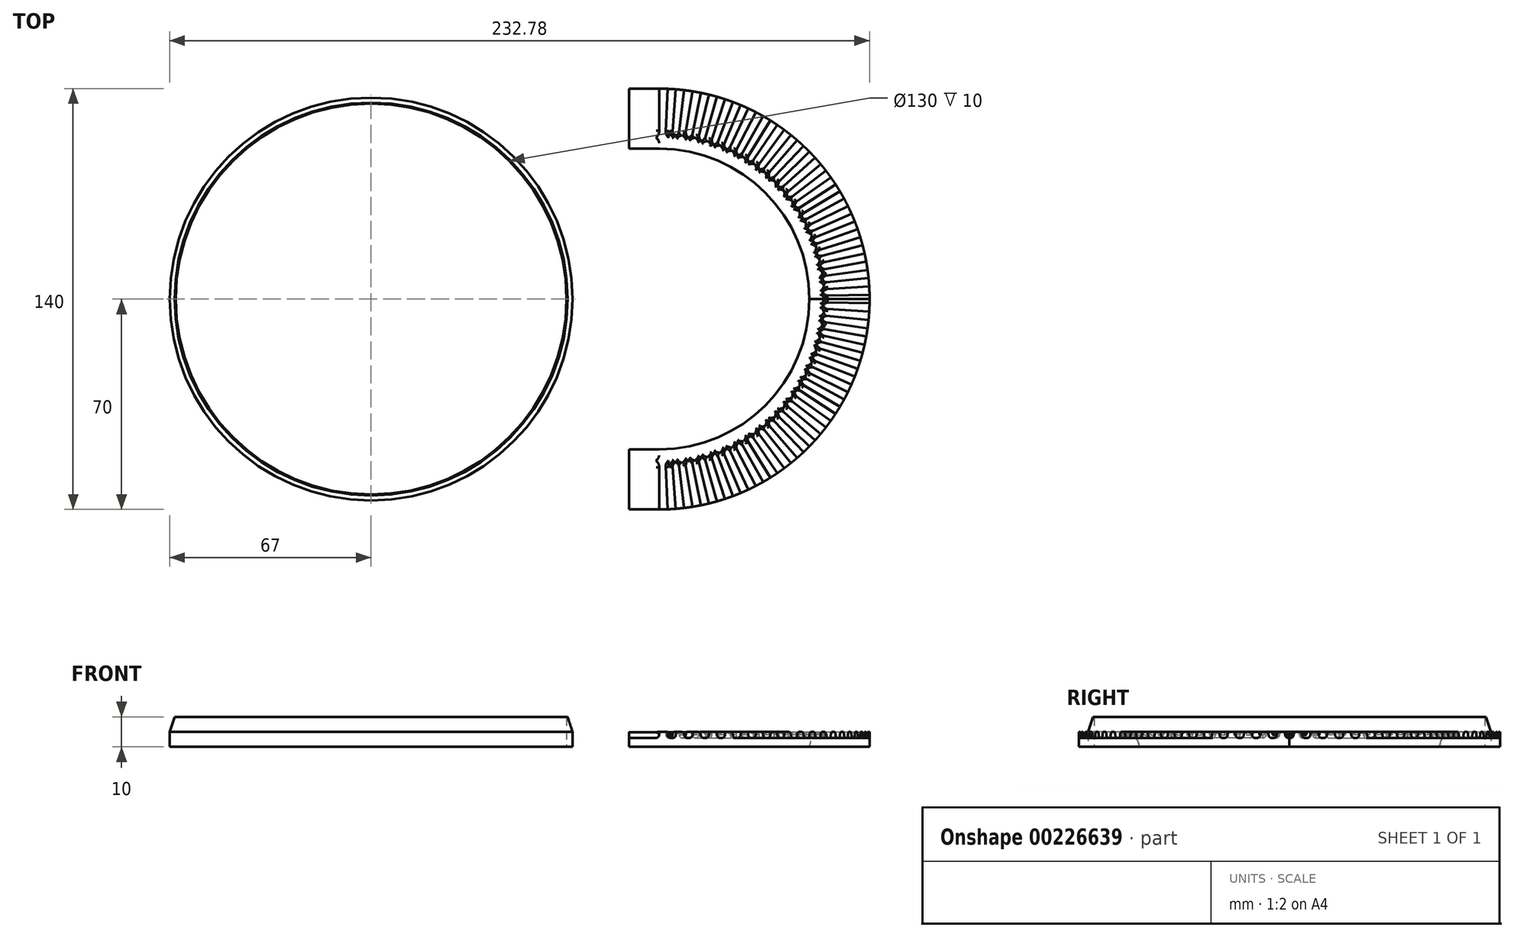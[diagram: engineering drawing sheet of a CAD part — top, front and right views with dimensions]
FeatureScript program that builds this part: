
annotation { "Feature Type Name" : "Feature", "Feature Type Description" : "" }
export const myFeature = defineFeature(function(context is Context, id is Id, definition is map)
    precondition{}
    {
        {
            var Q0;
            Q0=qCreatedBy(makeId("Top.planeOp"),FACE);
            var sketch = newSketch(context, id + "F0", { "sketchPlane" : qUnion([Q0])});
            skCircle(sketch, "E0", {"center": v(0, 0) * mm, "radius": 65 * mm});
            skCircle(sketch, "E1", {"center": v(0, 0) * mm, "radius": 67 * mm});
            skSolve(sketch);
        }
        {
            var Q0;
            Q0=makeQuery(id+"F0.imprint","IMPRINT",FACE,{"disambiguationData":[TD([[makeQuery(id+"F0.imprint","IMPRINT",EDGE,{"derivedFrom":sQuery(id+"F0.wireOp",EDGE,"E0")}),-1.0]])]});
            extrude(context, id + "F1", {"entities" : qUnion([Q0]), "depth" : 10 * mm});
        }
        {
            var Q0;
            Q0=makeQuery(id+"F1.opExtrude","CAP_EDGE",EDGE,{"disambiguationData":[OSD([sQuery(id+"F0.wireOp",EDGE,"E1")])],"isStart":false});
            chamfer(context, id + "F2", {"entities" : qUnion([Q0]), "chamferType" : ChamferType.TWO_OFFSETS, "width1" : 1.65 * mm, "oppositeDirection" : false, "width2" : 5 * mm, "tangentPropagation" : true});
        }
        {
            var Q0;
            Q0=qCreatedBy(makeId("Top.planeOp"),FACE);
            var sketch = newSketch(context, id + "F3", { "sketchPlane" : qUnion([Q0])});
            skLineSegment(sketch, "E2", {"start": v(95.78, 0) * mm, "end": v(95.78, 70) * mm, "construction": true});
            skArc(sketch, "E3", {"start": v(95.78, 70) * mm, "mid": v(165.78, 0) * mm, "end": v(95.78, -70) * mm});
            skArc(sketch, "E4", {"start": v(95.78, 50) * mm, "mid": v(145.78, 0) * mm, "end": v(95.78, -50) * mm});
            skLineSegment(sketch, "E5.bottom", {"start": v(95.78, 50) * mm, "end": v(85.78, 50) * mm});
            skLineSegment(sketch, "E5.top", {"start": v(95.78, 70) * mm, "end": v(85.78, 70) * mm});
            skLineSegment(sketch, "E5.left", {"start": v(95.78, 50) * mm, "end": v(95.78, 70) * mm});
            skLineSegment(sketch, "E5.right", {"start": v(85.78, 50) * mm, "end": v(85.78, 70) * mm});
            skLineSegment(sketch, "E6.bottom", {"start": v(95.78, -50) * mm, "end": v(85.78, -50) * mm});
            skLineSegment(sketch, "E6.top", {"start": v(95.78, -70) * mm, "end": v(85.78, -70) * mm});
            skLineSegment(sketch, "E6.left", {"start": v(95.78, -50) * mm, "end": v(95.78, -70) * mm});
            skLineSegment(sketch, "E6.right", {"start": v(85.78, -50) * mm, "end": v(85.78, -70) * mm});
            skSolve(sketch);
        }
        {
            var Q0;
            Q0 = qSketchRegion(id + "F3", true);
            extrude(context, id + "F4", {"entities" : qUnion([Q0]), "depth" : 5 * mm});
        }
        {
            var Q0;
            Q0=makeQuery(id+"F4.opExtrude","CAP_EDGE",EDGE,{"disambiguationData":[OSD([sQuery(id+"F3.wireOp",EDGE,"E4")])],"isStart":false});
            fillet(context, id + "F5", {"entities" : qUnion([Q0]), "radius" : 5 * mm, "tangentPropagation" : true, "allowEdgeOverflow" : false});
        }
        {
            var Q0;
            Q0=makeQuery(id+"F4.opExtrude","CAP_FACE",FACE,{"disambiguationData":[OSD([sQuery(id+"F3.wireOp",EDGE,"E3"),sQuery(id+"F3.wireOp",EDGE,"E4"),sQuery(id+"F3.wireOp",EDGE,"E5.bottom"),sQuery(id+"F3.wireOp",EDGE,"E5.top"),sQuery(id+"F3.wireOp",EDGE,"E5.right"),sQuery(id+"F3.wireOp",EDGE,"E6.bottom"),sQuery(id+"F3.wireOp",EDGE,"E6.top"),sQuery(id+"F3.wireOp",EDGE,"E6.right")])],"isStart":false});
            var sketch = newSketch(context, id + "F6", { "sketchPlane" : qUnion([Q0])});
            skLineSegment(sketch, "E7", {"start": v(95.78, 0) * mm, "end": v(95.78, 55) * mm, "construction": true});
            skLineSegment(sketch, "E8", {"start": v(95.78, 55) * mm, "end": v(95.78, 70) * mm});
            skLineSegment(sketch, "E9.1.0", {"start": v(97.97, 54.96) * mm, "end": v(98.57, 69.94) * mm});
            skLineSegment(sketch, "E9.2.0", {"start": v(100.15, 54.83) * mm, "end": v(101.34, 69.78) * mm});
            skLineSegment(sketch, "E9.3.0", {"start": v(102.33, 54.6) * mm, "end": v(104.11, 69.5) * mm});
            skLineSegment(sketch, "E9.4.0", {"start": v(104.5, 54.3) * mm, "end": v(106.87, 69.12) * mm});
            skLineSegment(sketch, "E9.5.0", {"start": v(106.65, 53.92) * mm, "end": v(109.61, 68.62) * mm});
            skLineSegment(sketch, "E9.6.0", {"start": v(108.78, 53.44) * mm, "end": v(112.33, 68.02) * mm});
            skLineSegment(sketch, "E9.7.0", {"start": v(110.9, 52.88) * mm, "end": v(115.02, 67.3) * mm});
            skLineSegment(sketch, "E9.8.0", {"start": v(112.99, 52.24) * mm, "end": v(117.68, 66.49) * mm});
            skLineSegment(sketch, "E9.9.0", {"start": v(115.05, 51.51) * mm, "end": v(120.3, 65.56) * mm});
            skLineSegment(sketch, "E9.10.0", {"start": v(117.08, 50.7) * mm, "end": v(122.9, 64.54) * mm});
            skLineSegment(sketch, "E9.11.0", {"start": v(119.08, 49.82) * mm, "end": v(125.44, 63.4) * mm});
            skLineSegment(sketch, "E9.12.0", {"start": v(121.04, 48.86) * mm, "end": v(127.93, 62.18) * mm});
            skLineSegment(sketch, "E9.13.0", {"start": v(122.97, 47.81) * mm, "end": v(130.38, 60.85) * mm});
            skLineSegment(sketch, "E9.14.0", {"start": v(124.85, 46.7) * mm, "end": v(132.77, 59.43) * mm});
            skLineSegment(sketch, "E9.15.0", {"start": v(126.68, 45.5) * mm, "end": v(135.1, 57.91) * mm});
            skLineSegment(sketch, "E9.16.0", {"start": v(128.46, 44.24) * mm, "end": v(137.38, 56.3) * mm});
            skLineSegment(sketch, "E9.17.0", {"start": v(130.2, 42.9) * mm, "end": v(139.58, 54.6) * mm});
            skLineSegment(sketch, "E9.18.0", {"start": v(131.88, 41.5) * mm, "end": v(141.72, 52.82) * mm});
            skLineSegment(sketch, "E9.19.0", {"start": v(133.5, 40.03) * mm, "end": v(143.78, 50.95) * mm});
            skLineSegment(sketch, "E9.20.0", {"start": v(135.06, 38.5) * mm, "end": v(145.77, 49) * mm});
            skLineSegment(sketch, "E9.21.0", {"start": v(136.56, 36.91) * mm, "end": v(147.68, 46.98) * mm});
            skLineSegment(sketch, "E9.22.0", {"start": v(138, 35.26) * mm, "end": v(149.5, 44.88) * mm});
            skLineSegment(sketch, "E9.23.0", {"start": v(139.36, 33.55) * mm, "end": v(151.25, 42.7) * mm});
            skLineSegment(sketch, "E9.24.0", {"start": v(140.66, 31.8) * mm, "end": v(152.9, 40.47) * mm});
            skLineSegment(sketch, "E9.25.0", {"start": v(141.9, 29.99) * mm, "end": v(154.47, 38.16) * mm});
            skLineSegment(sketch, "E9.26.0", {"start": v(143.05, 28.13) * mm, "end": v(155.94, 35.8) * mm});
            skLineSegment(sketch, "E9.27.0", {"start": v(144.13, 26.23) * mm, "end": v(157.31, 33.38) * mm});
            skLineSegment(sketch, "E9.28.0", {"start": v(145.13, 24.29) * mm, "end": v(158.6, 30.9) * mm});
            skLineSegment(sketch, "E9.29.0", {"start": v(146.06, 22.3) * mm, "end": v(159.77, 28.39) * mm});
            skLineSegment(sketch, "E9.30.0", {"start": v(146.9, 20.29) * mm, "end": v(160.85, 25.82) * mm});
            skLineSegment(sketch, "E9.31.0", {"start": v(147.67, 18.24) * mm, "end": v(161.82, 23.21) * mm});
            skLineSegment(sketch, "E9.32.0", {"start": v(148.36, 16.16) * mm, "end": v(162.7, 20.57) * mm});
            skLineSegment(sketch, "E9.33.0", {"start": v(148.96, 14.06) * mm, "end": v(163.46, 17.9) * mm});
            skLineSegment(sketch, "E9.34.0", {"start": v(149.47, 11.93) * mm, "end": v(164.12, 15.19) * mm});
            skLineSegment(sketch, "E9.35.0", {"start": v(149.9, 9.79) * mm, "end": v(164.67, 12.46) * mm});
            skLineSegment(sketch, "E9.36.0", {"start": v(150.25, 7.63) * mm, "end": v(165.1, 9.71) * mm});
            skLineSegment(sketch, "E9.37.0", {"start": v(150.51, 5.46) * mm, "end": v(165.44, 6.95) * mm});
            skLineSegment(sketch, "E9.38.0", {"start": v(150.69, 3.28) * mm, "end": v(165.66, 4.17) * mm});
            skLineSegment(sketch, "E9.39.0", {"start": v(150.77, 1.1) * mm, "end": v(165.77, 1.4) * mm});
            skLineSegment(sketch, "E9.40.0", {"start": v(150.77, -1.1) * mm, "end": v(165.77, -1.4) * mm});
            skLineSegment(sketch, "E9.41.0", {"start": v(150.69, -3.28) * mm, "end": v(165.66, -4.17) * mm});
            skLineSegment(sketch, "E9.42.0", {"start": v(150.51, -5.46) * mm, "end": v(165.44, -6.95) * mm});
            skLineSegment(sketch, "E9.43.0", {"start": v(150.25, -7.63) * mm, "end": v(165.1, -9.71) * mm});
            skLineSegment(sketch, "E9.44.0", {"start": v(149.9, -9.79) * mm, "end": v(164.67, -12.46) * mm});
            skLineSegment(sketch, "E9.45.0", {"start": v(149.47, -11.93) * mm, "end": v(164.12, -15.19) * mm});
            skLineSegment(sketch, "E9.46.0", {"start": v(148.96, -14.06) * mm, "end": v(163.46, -17.9) * mm});
            skLineSegment(sketch, "E9.47.0", {"start": v(148.36, -16.16) * mm, "end": v(162.7, -20.57) * mm});
            skLineSegment(sketch, "E9.48.0", {"start": v(147.67, -18.24) * mm, "end": v(161.82, -23.21) * mm});
            skLineSegment(sketch, "E9.49.0", {"start": v(146.9, -20.29) * mm, "end": v(160.85, -25.82) * mm});
            skLineSegment(sketch, "E9.50.0", {"start": v(146.06, -22.3) * mm, "end": v(159.77, -28.39) * mm});
            skLineSegment(sketch, "E9.51.0", {"start": v(145.13, -24.29) * mm, "end": v(158.6, -30.9) * mm});
            skLineSegment(sketch, "E9.52.0", {"start": v(144.13, -26.23) * mm, "end": v(157.31, -33.38) * mm});
            skLineSegment(sketch, "E9.53.0", {"start": v(143.05, -28.13) * mm, "end": v(155.94, -35.8) * mm});
            skLineSegment(sketch, "E9.54.0", {"start": v(141.9, -29.99) * mm, "end": v(154.47, -38.16) * mm});
            skLineSegment(sketch, "E9.55.0", {"start": v(140.66, -31.8) * mm, "end": v(152.9, -40.47) * mm});
            skLineSegment(sketch, "E9.56.0", {"start": v(139.36, -33.55) * mm, "end": v(151.25, -42.7) * mm});
            skLineSegment(sketch, "E9.57.0", {"start": v(138, -35.26) * mm, "end": v(149.5, -44.88) * mm});
            skLineSegment(sketch, "E9.58.0", {"start": v(136.56, -36.91) * mm, "end": v(147.68, -46.98) * mm});
            skLineSegment(sketch, "E9.59.0", {"start": v(135.06, -38.5) * mm, "end": v(145.77, -49) * mm});
            skLineSegment(sketch, "E9.60.0", {"start": v(133.5, -40.03) * mm, "end": v(143.78, -50.95) * mm});
            skLineSegment(sketch, "E9.61.0", {"start": v(131.88, -41.5) * mm, "end": v(141.72, -52.82) * mm});
            skLineSegment(sketch, "E9.62.0", {"start": v(130.2, -42.9) * mm, "end": v(139.58, -54.6) * mm});
            skLineSegment(sketch, "E9.63.0", {"start": v(128.46, -44.24) * mm, "end": v(137.38, -56.3) * mm});
            skLineSegment(sketch, "E9.64.0", {"start": v(126.68, -45.5) * mm, "end": v(135.1, -57.91) * mm});
            skLineSegment(sketch, "E9.65.0", {"start": v(124.85, -46.7) * mm, "end": v(132.77, -59.43) * mm});
            skLineSegment(sketch, "E9.66.0", {"start": v(122.97, -47.81) * mm, "end": v(130.38, -60.85) * mm});
            skLineSegment(sketch, "E9.67.0", {"start": v(121.04, -48.86) * mm, "end": v(127.93, -62.18) * mm});
            skLineSegment(sketch, "E9.68.0", {"start": v(119.08, -49.82) * mm, "end": v(125.44, -63.4) * mm});
            skLineSegment(sketch, "E9.69.0", {"start": v(117.08, -50.7) * mm, "end": v(122.9, -64.54) * mm});
            skLineSegment(sketch, "E9.70.0", {"start": v(115.05, -51.51) * mm, "end": v(120.3, -65.56) * mm});
            skLineSegment(sketch, "E9.71.0", {"start": v(112.99, -52.24) * mm, "end": v(117.68, -66.49) * mm});
            skLineSegment(sketch, "E9.72.0", {"start": v(110.9, -52.88) * mm, "end": v(115.02, -67.3) * mm});
            skLineSegment(sketch, "E9.73.0", {"start": v(108.78, -53.44) * mm, "end": v(112.33, -68.02) * mm});
            skLineSegment(sketch, "E9.74.0", {"start": v(106.65, -53.92) * mm, "end": v(109.61, -68.62) * mm});
            skLineSegment(sketch, "E9.75.0", {"start": v(104.5, -54.3) * mm, "end": v(106.87, -69.12) * mm});
            skLineSegment(sketch, "E9.76.0", {"start": v(102.33, -54.6) * mm, "end": v(104.11, -69.5) * mm});
            skLineSegment(sketch, "E9.77.0", {"start": v(100.15, -54.83) * mm, "end": v(101.34, -69.78) * mm});
            skLineSegment(sketch, "E9.78.0", {"start": v(97.97, -54.96) * mm, "end": v(98.57, -69.94) * mm});
            skLineSegment(sketch, "E9.79.0", {"start": v(95.78, -55) * mm, "end": v(95.78, -70) * mm});
            skPoint(sketch, "E9.center", {"position": v(95.78, 0) * mm});
            skLineSegment(sketch, "E9.anchor2", {"start": v(95.78, 0) * mm, "end": v(95.78, -55) * mm, "construction": true});
            skSolve(sketch);
        }
        {
            var Q0;
            Q0=makeQuery(id+"F6.imprint","IMPRINT",FACE,{"disambiguationData":[TD([[makeQuery(id+"F6.imprint","IMPRINT",EDGE,{"derivedFrom":sQuery(id+"F6.wireOp",EDGE,"E8")}),1.0]])]});
            var Q1;
            {var subQ0=sQuery(id+"F6.wireOp",EDGE,"E9.1.0");Q1=makeQuery(id+"F6.imprint","IMPRINT",FACE,{"disambiguationData":[TD([[makeQuery(id+"F6.imprint","IMPRINT",EDGE,{"derivedFrom":subQ0}),-1.0]])]});}
            var Q2;
            {var subQ0=sQuery(id+"F6.wireOp",EDGE,"E9.3.0");Q2=makeQuery(id+"F6.imprint","IMPRINT",FACE,{"disambiguationData":[TD([[makeQuery(id+"F6.imprint","IMPRINT",EDGE,{"derivedFrom":subQ0}),-1.0]])]});}
            var Q3;
            {var subQ0=sQuery(id+"F6.wireOp",EDGE,"E9.5.0");Q3=makeQuery(id+"F6.imprint","IMPRINT",FACE,{"disambiguationData":[TD([[makeQuery(id+"F6.imprint","IMPRINT",EDGE,{"derivedFrom":subQ0}),-1.0]])]});}
            var Q4;
            {var subQ0=sQuery(id+"F6.wireOp",EDGE,"E9.7.0");Q4=makeQuery(id+"F6.imprint","IMPRINT",FACE,{"disambiguationData":[TD([[makeQuery(id+"F6.imprint","IMPRINT",EDGE,{"derivedFrom":subQ0}),-1.0]])]});}
            var Q5;
            {var subQ0=sQuery(id+"F6.wireOp",EDGE,"E9.9.0");Q5=makeQuery(id+"F6.imprint","IMPRINT",FACE,{"disambiguationData":[TD([[makeQuery(id+"F6.imprint","IMPRINT",EDGE,{"derivedFrom":subQ0}),-1.0]])]});}
            var Q6;
            {var subQ0=sQuery(id+"F6.wireOp",EDGE,"E9.11.0");Q6=makeQuery(id+"F6.imprint","IMPRINT",FACE,{"disambiguationData":[TD([[makeQuery(id+"F6.imprint","IMPRINT",EDGE,{"derivedFrom":subQ0}),-1.0]])]});}
            var Q7;
            {var subQ0=sQuery(id+"F6.wireOp",EDGE,"E9.13.0");Q7=makeQuery(id+"F6.imprint","IMPRINT",FACE,{"disambiguationData":[TD([[makeQuery(id+"F6.imprint","IMPRINT",EDGE,{"derivedFrom":subQ0}),-1.0]])]});}
            var Q8;
            {var subQ0=sQuery(id+"F6.wireOp",EDGE,"E9.15.0");Q8=makeQuery(id+"F6.imprint","IMPRINT",FACE,{"disambiguationData":[TD([[makeQuery(id+"F6.imprint","IMPRINT",EDGE,{"derivedFrom":subQ0}),-1.0]])]});}
            var Q9;
            {var subQ0=sQuery(id+"F6.wireOp",EDGE,"E9.17.0");Q9=makeQuery(id+"F6.imprint","IMPRINT",FACE,{"disambiguationData":[TD([[makeQuery(id+"F6.imprint","IMPRINT",EDGE,{"derivedFrom":subQ0}),-1.0]])]});}
            var Q10;
            {var subQ0=sQuery(id+"F6.wireOp",EDGE,"E9.19.0");Q10=makeQuery(id+"F6.imprint","IMPRINT",FACE,{"disambiguationData":[TD([[makeQuery(id+"F6.imprint","IMPRINT",EDGE,{"derivedFrom":subQ0}),-1.0]])]});}
            var Q11;
            {var subQ0=sQuery(id+"F6.wireOp",EDGE,"E9.21.0");Q11=makeQuery(id+"F6.imprint","IMPRINT",FACE,{"disambiguationData":[TD([[makeQuery(id+"F6.imprint","IMPRINT",EDGE,{"derivedFrom":subQ0}),-1.0]])]});}
            var Q12;
            {var subQ0=sQuery(id+"F6.wireOp",EDGE,"E9.23.0");Q12=makeQuery(id+"F6.imprint","IMPRINT",FACE,{"disambiguationData":[TD([[makeQuery(id+"F6.imprint","IMPRINT",EDGE,{"derivedFrom":subQ0}),-1.0]])]});}
            var Q13;
            {var subQ0=sQuery(id+"F6.wireOp",EDGE,"E9.25.0");Q13=makeQuery(id+"F6.imprint","IMPRINT",FACE,{"disambiguationData":[TD([[makeQuery(id+"F6.imprint","IMPRINT",EDGE,{"derivedFrom":subQ0}),-1.0]])]});}
            var Q14;
            {var subQ0=sQuery(id+"F6.wireOp",EDGE,"E9.27.0");Q14=makeQuery(id+"F6.imprint","IMPRINT",FACE,{"disambiguationData":[TD([[makeQuery(id+"F6.imprint","IMPRINT",EDGE,{"derivedFrom":subQ0}),-1.0]])]});}
            var Q15;
            {var subQ0=sQuery(id+"F6.wireOp",EDGE,"E9.29.0");Q15=makeQuery(id+"F6.imprint","IMPRINT",FACE,{"disambiguationData":[TD([[makeQuery(id+"F6.imprint","IMPRINT",EDGE,{"derivedFrom":subQ0}),-1.0]])]});}
            var Q16;
            {var subQ0=sQuery(id+"F6.wireOp",EDGE,"E9.31.0");Q16=makeQuery(id+"F6.imprint","IMPRINT",FACE,{"disambiguationData":[TD([[makeQuery(id+"F6.imprint","IMPRINT",EDGE,{"derivedFrom":subQ0}),-1.0]])]});}
            var Q17;
            {var subQ0=sQuery(id+"F6.wireOp",EDGE,"E9.33.0");Q17=makeQuery(id+"F6.imprint","IMPRINT",FACE,{"disambiguationData":[TD([[makeQuery(id+"F6.imprint","IMPRINT",EDGE,{"derivedFrom":subQ0}),-1.0]])]});}
            var Q18;
            {var subQ0=sQuery(id+"F6.wireOp",EDGE,"E9.35.0");Q18=makeQuery(id+"F6.imprint","IMPRINT",FACE,{"disambiguationData":[TD([[makeQuery(id+"F6.imprint","IMPRINT",EDGE,{"derivedFrom":subQ0}),-1.0]])]});}
            var Q19;
            {var subQ0=sQuery(id+"F6.wireOp",EDGE,"E9.37.0");Q19=makeQuery(id+"F6.imprint","IMPRINT",FACE,{"disambiguationData":[TD([[makeQuery(id+"F6.imprint","IMPRINT",EDGE,{"derivedFrom":subQ0}),-1.0]])]});}
            var Q20;
            {var subQ0=sQuery(id+"F6.wireOp",EDGE,"E9.39.0");Q20=makeQuery(id+"F6.imprint","IMPRINT",FACE,{"disambiguationData":[TD([[makeQuery(id+"F6.imprint","IMPRINT",EDGE,{"derivedFrom":subQ0}),-1.0]])]});}
            var Q21;
            {var subQ0=sQuery(id+"F6.wireOp",EDGE,"E9.41.0");Q21=makeQuery(id+"F6.imprint","IMPRINT",FACE,{"disambiguationData":[TD([[makeQuery(id+"F6.imprint","IMPRINT",EDGE,{"derivedFrom":subQ0}),-1.0]])]});}
            var Q22;
            {var subQ0=sQuery(id+"F6.wireOp",EDGE,"E9.43.0");Q22=makeQuery(id+"F6.imprint","IMPRINT",FACE,{"disambiguationData":[TD([[makeQuery(id+"F6.imprint","IMPRINT",EDGE,{"derivedFrom":subQ0}),-1.0]])]});}
            var Q23;
            {var subQ0=sQuery(id+"F6.wireOp",EDGE,"E9.45.0");Q23=makeQuery(id+"F6.imprint","IMPRINT",FACE,{"disambiguationData":[TD([[makeQuery(id+"F6.imprint","IMPRINT",EDGE,{"derivedFrom":subQ0}),-1.0]])]});}
            var Q24;
            {var subQ0=sQuery(id+"F6.wireOp",EDGE,"E9.47.0");Q24=makeQuery(id+"F6.imprint","IMPRINT",FACE,{"disambiguationData":[TD([[makeQuery(id+"F6.imprint","IMPRINT",EDGE,{"derivedFrom":subQ0}),-1.0]])]});}
            var Q25;
            {var subQ0=sQuery(id+"F6.wireOp",EDGE,"E9.49.0");Q25=makeQuery(id+"F6.imprint","IMPRINT",FACE,{"disambiguationData":[TD([[makeQuery(id+"F6.imprint","IMPRINT",EDGE,{"derivedFrom":subQ0}),-1.0]])]});}
            var Q26;
            {var subQ0=sQuery(id+"F6.wireOp",EDGE,"E9.51.0");Q26=makeQuery(id+"F6.imprint","IMPRINT",FACE,{"disambiguationData":[TD([[makeQuery(id+"F6.imprint","IMPRINT",EDGE,{"derivedFrom":subQ0}),-1.0]])]});}
            var Q27;
            {var subQ0=sQuery(id+"F6.wireOp",EDGE,"E9.53.0");Q27=makeQuery(id+"F6.imprint","IMPRINT",FACE,{"disambiguationData":[TD([[makeQuery(id+"F6.imprint","IMPRINT",EDGE,{"derivedFrom":subQ0}),-1.0]])]});}
            var Q28;
            {var subQ0=sQuery(id+"F6.wireOp",EDGE,"E9.55.0");Q28=makeQuery(id+"F6.imprint","IMPRINT",FACE,{"disambiguationData":[TD([[makeQuery(id+"F6.imprint","IMPRINT",EDGE,{"derivedFrom":subQ0}),-1.0]])]});}
            var Q29;
            {var subQ0=sQuery(id+"F6.wireOp",EDGE,"E9.57.0");Q29=makeQuery(id+"F6.imprint","IMPRINT",FACE,{"disambiguationData":[TD([[makeQuery(id+"F6.imprint","IMPRINT",EDGE,{"derivedFrom":subQ0}),-1.0]])]});}
            var Q30;
            {var subQ0=sQuery(id+"F6.wireOp",EDGE,"E9.59.0");Q30=makeQuery(id+"F6.imprint","IMPRINT",FACE,{"disambiguationData":[TD([[makeQuery(id+"F6.imprint","IMPRINT",EDGE,{"derivedFrom":subQ0}),-1.0]])]});}
            var Q31;
            {var subQ0=sQuery(id+"F6.wireOp",EDGE,"E9.61.0");Q31=makeQuery(id+"F6.imprint","IMPRINT",FACE,{"disambiguationData":[TD([[makeQuery(id+"F6.imprint","IMPRINT",EDGE,{"derivedFrom":subQ0}),-1.0]])]});}
            var Q32;
            {var subQ0=sQuery(id+"F6.wireOp",EDGE,"E9.63.0");Q32=makeQuery(id+"F6.imprint","IMPRINT",FACE,{"disambiguationData":[TD([[makeQuery(id+"F6.imprint","IMPRINT",EDGE,{"derivedFrom":subQ0}),-1.0]])]});}
            var Q33;
            {var subQ0=sQuery(id+"F6.wireOp",EDGE,"E9.65.0");Q33=makeQuery(id+"F6.imprint","IMPRINT",FACE,{"disambiguationData":[TD([[makeQuery(id+"F6.imprint","IMPRINT",EDGE,{"derivedFrom":subQ0}),-1.0]])]});}
            var Q34;
            {var subQ0=sQuery(id+"F6.wireOp",EDGE,"E9.67.0");Q34=makeQuery(id+"F6.imprint","IMPRINT",FACE,{"disambiguationData":[TD([[makeQuery(id+"F6.imprint","IMPRINT",EDGE,{"derivedFrom":subQ0}),-1.0]])]});}
            var Q35;
            {var subQ0=sQuery(id+"F6.wireOp",EDGE,"E9.69.0");Q35=makeQuery(id+"F6.imprint","IMPRINT",FACE,{"disambiguationData":[TD([[makeQuery(id+"F6.imprint","IMPRINT",EDGE,{"derivedFrom":subQ0}),-1.0]])]});}
            var Q36;
            {var subQ0=sQuery(id+"F6.wireOp",EDGE,"E9.71.0");Q36=makeQuery(id+"F6.imprint","IMPRINT",FACE,{"disambiguationData":[TD([[makeQuery(id+"F6.imprint","IMPRINT",EDGE,{"derivedFrom":subQ0}),-1.0]])]});}
            var Q37;
            {var subQ0=sQuery(id+"F6.wireOp",EDGE,"E9.73.0");Q37=makeQuery(id+"F6.imprint","IMPRINT",FACE,{"disambiguationData":[TD([[makeQuery(id+"F6.imprint","IMPRINT",EDGE,{"derivedFrom":subQ0}),-1.0]])]});}
            var Q38;
            {var subQ0=sQuery(id+"F6.wireOp",EDGE,"E9.75.0");Q38=makeQuery(id+"F6.imprint","IMPRINT",FACE,{"disambiguationData":[TD([[makeQuery(id+"F6.imprint","IMPRINT",EDGE,{"derivedFrom":subQ0}),-1.0]])]});}
            var Q39;
            {var subQ0=sQuery(id+"F6.wireOp",EDGE,"E9.77.0");Q39=makeQuery(id+"F6.imprint","IMPRINT",FACE,{"disambiguationData":[TD([[makeQuery(id+"F6.imprint","IMPRINT",EDGE,{"derivedFrom":subQ0}),-1.0]])]});}
            var Q40;
            Q40=makeQuery(id+"F6.imprint","IMPRINT",FACE,{"disambiguationData":[TD([[makeQuery(id+"F6.imprint","IMPRINT",EDGE,{"derivedFrom":sQuery(id+"F6.wireOp",EDGE,"E9.79.0")}),-1.0]])]});
            extrude(context, id + "F7", {"entities" : qUnion([Q0, Q1, Q2, Q3, Q4, Q5, Q6, Q7, Q8, Q9, Q10, Q11, Q12, Q13, Q14, Q15, Q16, Q17, Q18, Q19, Q20, Q21, Q22, Q23, Q24, Q25, Q26, Q27, Q28, Q29, Q30, Q31, Q32, Q33, Q34, Q35, Q36, Q37, Q38, Q39, Q40]), "operationType" : NewBodyOperationType.REMOVE, "oppositeDirection" : true, "depth" : 2 * mm});
        }
        {
            var Q0;
            Q0=makeQuery(id+"F7.boolean.opBoolean","COPY",EDGE,{"derivedFrom":makeQuery(id+"F7.opExtrude","CAP_EDGE",EDGE,{"disambiguationData":[OSD([sQuery(id+"F6.wireOp",EDGE,"E8")])],"isStart":true})});
            var Q1;
            Q1=makeQuery(id+"F7.boolean.opBoolean","COPY",EDGE,{"derivedFrom":makeQuery(id+"F7.opExtrude","CAP_EDGE",EDGE,{"disambiguationData":[OSD([sQuery(id+"F6.wireOp",EDGE,"E9.1.0")])],"isStart":true})});
            var Q2;
            Q2=makeQuery(id+"F7.boolean.opBoolean","COPY",EDGE,{"derivedFrom":makeQuery(id+"F7.opExtrude","CAP_EDGE",EDGE,{"disambiguationData":[OSD([sQuery(id+"F6.wireOp",EDGE,"E9.2.0")])],"isStart":true})});
            var Q3;
            Q3=makeQuery(id+"F7.boolean.opBoolean","COPY",EDGE,{"derivedFrom":makeQuery(id+"F7.opExtrude","CAP_EDGE",EDGE,{"disambiguationData":[OSD([sQuery(id+"F6.wireOp",EDGE,"E9.3.0")])],"isStart":true})});
            var Q4;
            Q4=makeQuery(id+"F7.boolean.opBoolean","COPY",EDGE,{"derivedFrom":makeQuery(id+"F7.opExtrude","CAP_EDGE",EDGE,{"disambiguationData":[OSD([sQuery(id+"F6.wireOp",EDGE,"E9.4.0")])],"isStart":true})});
            var Q5;
            Q5=makeQuery(id+"F7.boolean.opBoolean","COPY",EDGE,{"derivedFrom":makeQuery(id+"F7.opExtrude","CAP_EDGE",EDGE,{"disambiguationData":[OSD([sQuery(id+"F6.wireOp",EDGE,"E9.5.0")])],"isStart":true})});
            var Q6;
            Q6=makeQuery(id+"F7.boolean.opBoolean","COPY",EDGE,{"derivedFrom":makeQuery(id+"F7.opExtrude","CAP_EDGE",EDGE,{"disambiguationData":[OSD([sQuery(id+"F6.wireOp",EDGE,"E9.6.0")])],"isStart":true})});
            var Q7;
            Q7=makeQuery(id+"F7.boolean.opBoolean","COPY",EDGE,{"derivedFrom":makeQuery(id+"F7.opExtrude","CAP_EDGE",EDGE,{"disambiguationData":[OSD([sQuery(id+"F6.wireOp",EDGE,"E9.7.0")])],"isStart":true})});
            var Q8;
            Q8=makeQuery(id+"F7.boolean.opBoolean","COPY",EDGE,{"derivedFrom":makeQuery(id+"F7.opExtrude","CAP_EDGE",EDGE,{"disambiguationData":[OSD([sQuery(id+"F6.wireOp",EDGE,"E9.8.0")])],"isStart":true})});
            var Q9;
            Q9=makeQuery(id+"F7.boolean.opBoolean","COPY",EDGE,{"derivedFrom":makeQuery(id+"F7.opExtrude","CAP_EDGE",EDGE,{"disambiguationData":[OSD([sQuery(id+"F6.wireOp",EDGE,"E9.9.0")])],"isStart":true})});
            var Q10;
            Q10=makeQuery(id+"F7.boolean.opBoolean","COPY",EDGE,{"derivedFrom":makeQuery(id+"F7.opExtrude","CAP_EDGE",EDGE,{"disambiguationData":[OSD([sQuery(id+"F6.wireOp",EDGE,"E9.10.0")])],"isStart":true})});
            var Q11;
            Q11=makeQuery(id+"F7.boolean.opBoolean","COPY",EDGE,{"derivedFrom":makeQuery(id+"F7.opExtrude","CAP_EDGE",EDGE,{"disambiguationData":[OSD([sQuery(id+"F6.wireOp",EDGE,"E9.11.0")])],"isStart":true})});
            var Q12;
            Q12=makeQuery(id+"F7.boolean.opBoolean","COPY",EDGE,{"derivedFrom":makeQuery(id+"F7.opExtrude","CAP_EDGE",EDGE,{"disambiguationData":[OSD([sQuery(id+"F6.wireOp",EDGE,"E9.12.0")])],"isStart":true})});
            var Q13;
            Q13=makeQuery(id+"F7.boolean.opBoolean","COPY",EDGE,{"derivedFrom":makeQuery(id+"F7.opExtrude","CAP_EDGE",EDGE,{"disambiguationData":[OSD([sQuery(id+"F6.wireOp",EDGE,"E9.13.0")])],"isStart":true})});
            var Q14;
            Q14=makeQuery(id+"F7.boolean.opBoolean","COPY",EDGE,{"derivedFrom":makeQuery(id+"F7.opExtrude","CAP_EDGE",EDGE,{"disambiguationData":[OSD([sQuery(id+"F6.wireOp",EDGE,"E9.14.0")])],"isStart":true})});
            var Q15;
            Q15=makeQuery(id+"F7.boolean.opBoolean","COPY",EDGE,{"derivedFrom":makeQuery(id+"F7.opExtrude","CAP_EDGE",EDGE,{"disambiguationData":[OSD([sQuery(id+"F6.wireOp",EDGE,"E9.15.0")])],"isStart":true})});
            var Q16;
            Q16=makeQuery(id+"F7.boolean.opBoolean","COPY",EDGE,{"derivedFrom":makeQuery(id+"F7.opExtrude","CAP_EDGE",EDGE,{"disambiguationData":[OSD([sQuery(id+"F6.wireOp",EDGE,"E9.16.0")])],"isStart":true})});
            var Q17;
            Q17=makeQuery(id+"F7.boolean.opBoolean","COPY",EDGE,{"derivedFrom":makeQuery(id+"F7.opExtrude","CAP_EDGE",EDGE,{"disambiguationData":[OSD([sQuery(id+"F6.wireOp",EDGE,"E9.17.0")])],"isStart":true})});
            var Q18;
            Q18=makeQuery(id+"F7.boolean.opBoolean","COPY",EDGE,{"derivedFrom":makeQuery(id+"F7.opExtrude","CAP_EDGE",EDGE,{"disambiguationData":[OSD([sQuery(id+"F6.wireOp",EDGE,"E9.18.0")])],"isStart":true})});
            var Q19;
            Q19=makeQuery(id+"F7.boolean.opBoolean","COPY",EDGE,{"derivedFrom":makeQuery(id+"F7.opExtrude","CAP_EDGE",EDGE,{"disambiguationData":[OSD([sQuery(id+"F6.wireOp",EDGE,"E9.19.0")])],"isStart":true})});
            var Q20;
            Q20=makeQuery(id+"F7.boolean.opBoolean","COPY",EDGE,{"derivedFrom":makeQuery(id+"F7.opExtrude","CAP_EDGE",EDGE,{"disambiguationData":[OSD([sQuery(id+"F6.wireOp",EDGE,"E9.20.0")])],"isStart":true})});
            var Q21;
            Q21=makeQuery(id+"F7.boolean.opBoolean","COPY",EDGE,{"derivedFrom":makeQuery(id+"F7.opExtrude","CAP_EDGE",EDGE,{"disambiguationData":[OSD([sQuery(id+"F6.wireOp",EDGE,"E9.21.0")])],"isStart":true})});
            var Q22;
            Q22=makeQuery(id+"F7.boolean.opBoolean","COPY",EDGE,{"derivedFrom":makeQuery(id+"F7.opExtrude","CAP_EDGE",EDGE,{"disambiguationData":[OSD([sQuery(id+"F6.wireOp",EDGE,"E9.22.0")])],"isStart":true})});
            var Q23;
            Q23=makeQuery(id+"F7.boolean.opBoolean","COPY",EDGE,{"derivedFrom":makeQuery(id+"F7.opExtrude","CAP_EDGE",EDGE,{"disambiguationData":[OSD([sQuery(id+"F6.wireOp",EDGE,"E9.23.0")])],"isStart":true})});
            var Q24;
            Q24=makeQuery(id+"F7.boolean.opBoolean","COPY",EDGE,{"derivedFrom":makeQuery(id+"F7.opExtrude","CAP_EDGE",EDGE,{"disambiguationData":[OSD([sQuery(id+"F6.wireOp",EDGE,"E9.24.0")])],"isStart":true})});
            var Q25;
            Q25=makeQuery(id+"F7.boolean.opBoolean","COPY",EDGE,{"derivedFrom":makeQuery(id+"F7.opExtrude","CAP_EDGE",EDGE,{"disambiguationData":[OSD([sQuery(id+"F6.wireOp",EDGE,"E9.25.0")])],"isStart":true})});
            var Q26;
            Q26=makeQuery(id+"F7.boolean.opBoolean","COPY",EDGE,{"derivedFrom":makeQuery(id+"F7.opExtrude","CAP_EDGE",EDGE,{"disambiguationData":[OSD([sQuery(id+"F6.wireOp",EDGE,"E9.26.0")])],"isStart":true})});
            var Q27;
            Q27=makeQuery(id+"F7.boolean.opBoolean","COPY",EDGE,{"derivedFrom":makeQuery(id+"F7.opExtrude","CAP_EDGE",EDGE,{"disambiguationData":[OSD([sQuery(id+"F6.wireOp",EDGE,"E9.27.0")])],"isStart":true})});
            var Q28;
            Q28=makeQuery(id+"F7.boolean.opBoolean","COPY",EDGE,{"derivedFrom":makeQuery(id+"F7.opExtrude","CAP_EDGE",EDGE,{"disambiguationData":[OSD([sQuery(id+"F6.wireOp",EDGE,"E9.28.0")])],"isStart":true})});
            var Q29;
            Q29=makeQuery(id+"F7.boolean.opBoolean","COPY",EDGE,{"derivedFrom":makeQuery(id+"F7.opExtrude","CAP_EDGE",EDGE,{"disambiguationData":[OSD([sQuery(id+"F6.wireOp",EDGE,"E9.29.0")])],"isStart":true})});
            var Q30;
            Q30=makeQuery(id+"F7.boolean.opBoolean","COPY",EDGE,{"derivedFrom":makeQuery(id+"F7.opExtrude","CAP_EDGE",EDGE,{"disambiguationData":[OSD([sQuery(id+"F6.wireOp",EDGE,"E9.30.0")])],"isStart":true})});
            var Q31;
            Q31=makeQuery(id+"F7.boolean.opBoolean","COPY",EDGE,{"derivedFrom":makeQuery(id+"F7.opExtrude","CAP_EDGE",EDGE,{"disambiguationData":[OSD([sQuery(id+"F6.wireOp",EDGE,"E9.31.0")])],"isStart":true})});
            var Q32;
            Q32=makeQuery(id+"F7.boolean.opBoolean","COPY",EDGE,{"derivedFrom":makeQuery(id+"F7.opExtrude","CAP_EDGE",EDGE,{"disambiguationData":[OSD([sQuery(id+"F6.wireOp",EDGE,"E9.32.0")])],"isStart":true})});
            var Q33;
            Q33=makeQuery(id+"F7.boolean.opBoolean","COPY",EDGE,{"derivedFrom":makeQuery(id+"F7.opExtrude","CAP_EDGE",EDGE,{"disambiguationData":[OSD([sQuery(id+"F6.wireOp",EDGE,"E9.34.0")])],"isStart":true})});
            var Q34;
            Q34=makeQuery(id+"F7.boolean.opBoolean","COPY",EDGE,{"derivedFrom":makeQuery(id+"F7.opExtrude","CAP_EDGE",EDGE,{"disambiguationData":[OSD([sQuery(id+"F6.wireOp",EDGE,"E9.35.0")])],"isStart":true})});
            var Q35;
            Q35=makeQuery(id+"F7.boolean.opBoolean","COPY",EDGE,{"derivedFrom":makeQuery(id+"F7.opExtrude","CAP_EDGE",EDGE,{"disambiguationData":[OSD([sQuery(id+"F6.wireOp",EDGE,"E9.33.0")])],"isStart":true})});
            var Q36;
            Q36=makeQuery(id+"F7.boolean.opBoolean","COPY",EDGE,{"derivedFrom":makeQuery(id+"F7.opExtrude","CAP_EDGE",EDGE,{"disambiguationData":[OSD([sQuery(id+"F6.wireOp",EDGE,"E9.36.0")])],"isStart":true})});
            var Q37;
            Q37=makeQuery(id+"F7.boolean.opBoolean","COPY",EDGE,{"derivedFrom":makeQuery(id+"F7.opExtrude","CAP_EDGE",EDGE,{"disambiguationData":[OSD([sQuery(id+"F6.wireOp",EDGE,"E9.37.0")])],"isStart":true})});
            var Q38;
            Q38=makeQuery(id+"F7.boolean.opBoolean","COPY",EDGE,{"derivedFrom":makeQuery(id+"F7.opExtrude","CAP_EDGE",EDGE,{"disambiguationData":[OSD([sQuery(id+"F6.wireOp",EDGE,"E9.38.0")])],"isStart":true})});
            var Q39;
            Q39=makeQuery(id+"F7.boolean.opBoolean","COPY",EDGE,{"derivedFrom":makeQuery(id+"F7.opExtrude","CAP_EDGE",EDGE,{"disambiguationData":[OSD([sQuery(id+"F6.wireOp",EDGE,"E9.39.0")])],"isStart":true})});
            var Q40;
            Q40=makeQuery(id+"F7.boolean.opBoolean","COPY",EDGE,{"derivedFrom":makeQuery(id+"F7.opExtrude","CAP_EDGE",EDGE,{"disambiguationData":[OSD([sQuery(id+"F6.wireOp",EDGE,"E9.40.0")])],"isStart":true})});
            var Q41;
            Q41=makeQuery(id+"F7.boolean.opBoolean","COPY",EDGE,{"derivedFrom":makeQuery(id+"F7.opExtrude","CAP_EDGE",EDGE,{"disambiguationData":[OSD([sQuery(id+"F6.wireOp",EDGE,"E9.41.0")])],"isStart":true})});
            var Q42;
            Q42=makeQuery(id+"F7.boolean.opBoolean","COPY",EDGE,{"derivedFrom":makeQuery(id+"F7.opExtrude","CAP_EDGE",EDGE,{"disambiguationData":[OSD([sQuery(id+"F6.wireOp",EDGE,"E9.42.0")])],"isStart":true})});
            var Q43;
            Q43=makeQuery(id+"F7.boolean.opBoolean","COPY",EDGE,{"derivedFrom":makeQuery(id+"F7.opExtrude","CAP_EDGE",EDGE,{"disambiguationData":[OSD([sQuery(id+"F6.wireOp",EDGE,"E9.43.0")])],"isStart":true})});
            var Q44;
            Q44=makeQuery(id+"F7.boolean.opBoolean","COPY",EDGE,{"derivedFrom":makeQuery(id+"F7.opExtrude","CAP_EDGE",EDGE,{"disambiguationData":[OSD([sQuery(id+"F6.wireOp",EDGE,"E9.44.0")])],"isStart":true})});
            var Q45;
            Q45=makeQuery(id+"F7.boolean.opBoolean","COPY",EDGE,{"derivedFrom":makeQuery(id+"F7.opExtrude","CAP_EDGE",EDGE,{"disambiguationData":[OSD([sQuery(id+"F6.wireOp",EDGE,"E9.45.0")])],"isStart":true})});
            var Q46;
            Q46=makeQuery(id+"F7.boolean.opBoolean","COPY",EDGE,{"derivedFrom":makeQuery(id+"F7.opExtrude","CAP_EDGE",EDGE,{"disambiguationData":[OSD([sQuery(id+"F6.wireOp",EDGE,"E9.46.0")])],"isStart":true})});
            var Q47;
            Q47=makeQuery(id+"F7.boolean.opBoolean","COPY",EDGE,{"derivedFrom":makeQuery(id+"F7.opExtrude","CAP_EDGE",EDGE,{"disambiguationData":[OSD([sQuery(id+"F6.wireOp",EDGE,"E9.47.0")])],"isStart":true})});
            var Q48;
            Q48=makeQuery(id+"F7.boolean.opBoolean","COPY",EDGE,{"derivedFrom":makeQuery(id+"F7.opExtrude","CAP_EDGE",EDGE,{"disambiguationData":[OSD([sQuery(id+"F6.wireOp",EDGE,"E9.48.0")])],"isStart":true})});
            var Q49;
            Q49=makeQuery(id+"F7.boolean.opBoolean","COPY",EDGE,{"derivedFrom":makeQuery(id+"F7.opExtrude","CAP_EDGE",EDGE,{"disambiguationData":[OSD([sQuery(id+"F6.wireOp",EDGE,"E9.49.0")])],"isStart":true})});
            var Q50;
            Q50=makeQuery(id+"F7.boolean.opBoolean","COPY",EDGE,{"derivedFrom":makeQuery(id+"F7.opExtrude","CAP_EDGE",EDGE,{"disambiguationData":[OSD([sQuery(id+"F6.wireOp",EDGE,"E9.50.0")])],"isStart":true})});
            var Q51;
            Q51=makeQuery(id+"F7.boolean.opBoolean","COPY",EDGE,{"derivedFrom":makeQuery(id+"F7.opExtrude","CAP_EDGE",EDGE,{"disambiguationData":[OSD([sQuery(id+"F6.wireOp",EDGE,"E9.51.0")])],"isStart":true})});
            var Q52;
            Q52=makeQuery(id+"F7.boolean.opBoolean","COPY",EDGE,{"derivedFrom":makeQuery(id+"F7.opExtrude","CAP_EDGE",EDGE,{"disambiguationData":[OSD([sQuery(id+"F6.wireOp",EDGE,"E9.52.0")])],"isStart":true})});
            var Q53;
            Q53=makeQuery(id+"F7.boolean.opBoolean","COPY",EDGE,{"derivedFrom":makeQuery(id+"F7.opExtrude","CAP_EDGE",EDGE,{"disambiguationData":[OSD([sQuery(id+"F6.wireOp",EDGE,"E9.53.0")])],"isStart":true})});
            var Q54;
            Q54=makeQuery(id+"F7.boolean.opBoolean","COPY",EDGE,{"derivedFrom":makeQuery(id+"F7.opExtrude","CAP_EDGE",EDGE,{"disambiguationData":[OSD([sQuery(id+"F6.wireOp",EDGE,"E9.54.0")])],"isStart":true})});
            var Q55;
            Q55=makeQuery(id+"F7.boolean.opBoolean","COPY",EDGE,{"derivedFrom":makeQuery(id+"F7.opExtrude","CAP_EDGE",EDGE,{"disambiguationData":[OSD([sQuery(id+"F6.wireOp",EDGE,"E9.55.0")])],"isStart":true})});
            var Q56;
            Q56=makeQuery(id+"F7.boolean.opBoolean","COPY",EDGE,{"derivedFrom":makeQuery(id+"F7.opExtrude","CAP_EDGE",EDGE,{"disambiguationData":[OSD([sQuery(id+"F6.wireOp",EDGE,"E9.56.0")])],"isStart":true})});
            var Q57;
            Q57=makeQuery(id+"F7.boolean.opBoolean","COPY",EDGE,{"derivedFrom":makeQuery(id+"F7.opExtrude","CAP_EDGE",EDGE,{"disambiguationData":[OSD([sQuery(id+"F6.wireOp",EDGE,"E9.57.0")])],"isStart":true})});
            var Q58;
            Q58=makeQuery(id+"F7.boolean.opBoolean","COPY",EDGE,{"derivedFrom":makeQuery(id+"F7.opExtrude","CAP_EDGE",EDGE,{"disambiguationData":[OSD([sQuery(id+"F6.wireOp",EDGE,"E9.58.0")])],"isStart":true})});
            var Q59;
            Q59=makeQuery(id+"F7.boolean.opBoolean","COPY",EDGE,{"derivedFrom":makeQuery(id+"F7.opExtrude","CAP_EDGE",EDGE,{"disambiguationData":[OSD([sQuery(id+"F6.wireOp",EDGE,"E9.59.0")])],"isStart":true})});
            var Q60;
            Q60=makeQuery(id+"F7.boolean.opBoolean","COPY",EDGE,{"derivedFrom":makeQuery(id+"F7.opExtrude","CAP_EDGE",EDGE,{"disambiguationData":[OSD([sQuery(id+"F6.wireOp",EDGE,"E9.60.0")])],"isStart":true})});
            var Q61;
            Q61=makeQuery(id+"F7.boolean.opBoolean","COPY",EDGE,{"derivedFrom":makeQuery(id+"F7.opExtrude","CAP_EDGE",EDGE,{"disambiguationData":[OSD([sQuery(id+"F6.wireOp",EDGE,"E9.61.0")])],"isStart":true})});
            var Q62;
            Q62=makeQuery(id+"F7.boolean.opBoolean","COPY",EDGE,{"derivedFrom":makeQuery(id+"F7.opExtrude","CAP_EDGE",EDGE,{"disambiguationData":[OSD([sQuery(id+"F6.wireOp",EDGE,"E9.62.0")])],"isStart":true})});
            var Q63;
            Q63=makeQuery(id+"F7.boolean.opBoolean","COPY",EDGE,{"derivedFrom":makeQuery(id+"F7.opExtrude","CAP_EDGE",EDGE,{"disambiguationData":[OSD([sQuery(id+"F6.wireOp",EDGE,"E9.63.0")])],"isStart":true})});
            var Q64;
            Q64=makeQuery(id+"F7.boolean.opBoolean","COPY",EDGE,{"derivedFrom":makeQuery(id+"F7.opExtrude","CAP_EDGE",EDGE,{"disambiguationData":[OSD([sQuery(id+"F6.wireOp",EDGE,"E9.64.0")])],"isStart":true})});
            var Q65;
            Q65=makeQuery(id+"F7.boolean.opBoolean","COPY",EDGE,{"derivedFrom":makeQuery(id+"F7.opExtrude","CAP_EDGE",EDGE,{"disambiguationData":[OSD([sQuery(id+"F6.wireOp",EDGE,"E9.65.0")])],"isStart":true})});
            var Q66;
            Q66=makeQuery(id+"F7.boolean.opBoolean","COPY",EDGE,{"derivedFrom":makeQuery(id+"F7.opExtrude","CAP_EDGE",EDGE,{"disambiguationData":[OSD([sQuery(id+"F6.wireOp",EDGE,"E9.66.0")])],"isStart":true})});
            var Q67;
            Q67=makeQuery(id+"F7.boolean.opBoolean","COPY",EDGE,{"derivedFrom":makeQuery(id+"F7.opExtrude","CAP_EDGE",EDGE,{"disambiguationData":[OSD([sQuery(id+"F6.wireOp",EDGE,"E9.67.0")])],"isStart":true})});
            var Q68;
            Q68=makeQuery(id+"F7.boolean.opBoolean","COPY",EDGE,{"derivedFrom":makeQuery(id+"F7.opExtrude","CAP_EDGE",EDGE,{"disambiguationData":[OSD([sQuery(id+"F6.wireOp",EDGE,"E9.68.0")])],"isStart":true})});
            var Q69;
            Q69=makeQuery(id+"F7.boolean.opBoolean","COPY",EDGE,{"derivedFrom":makeQuery(id+"F7.opExtrude","CAP_EDGE",EDGE,{"disambiguationData":[OSD([sQuery(id+"F6.wireOp",EDGE,"E9.69.0")])],"isStart":true})});
            var Q70;
            Q70=makeQuery(id+"F7.boolean.opBoolean","COPY",EDGE,{"derivedFrom":makeQuery(id+"F7.opExtrude","CAP_EDGE",EDGE,{"disambiguationData":[OSD([sQuery(id+"F6.wireOp",EDGE,"E9.70.0")])],"isStart":true})});
            var Q71;
            Q71=makeQuery(id+"F7.boolean.opBoolean","COPY",EDGE,{"derivedFrom":makeQuery(id+"F7.opExtrude","CAP_EDGE",EDGE,{"disambiguationData":[OSD([sQuery(id+"F6.wireOp",EDGE,"E9.71.0")])],"isStart":true})});
            var Q72;
            Q72=makeQuery(id+"F7.boolean.opBoolean","COPY",EDGE,{"derivedFrom":makeQuery(id+"F7.opExtrude","CAP_EDGE",EDGE,{"disambiguationData":[OSD([sQuery(id+"F6.wireOp",EDGE,"E9.72.0")])],"isStart":true})});
            var Q73;
            Q73=makeQuery(id+"F7.boolean.opBoolean","COPY",EDGE,{"derivedFrom":makeQuery(id+"F7.opExtrude","CAP_EDGE",EDGE,{"disambiguationData":[OSD([sQuery(id+"F6.wireOp",EDGE,"E9.73.0")])],"isStart":true})});
            var Q74;
            Q74=makeQuery(id+"F7.boolean.opBoolean","COPY",EDGE,{"derivedFrom":makeQuery(id+"F7.opExtrude","CAP_EDGE",EDGE,{"disambiguationData":[OSD([sQuery(id+"F6.wireOp",EDGE,"E9.74.0")])],"isStart":true})});
            var Q75;
            Q75=makeQuery(id+"F7.boolean.opBoolean","COPY",EDGE,{"derivedFrom":makeQuery(id+"F7.opExtrude","CAP_EDGE",EDGE,{"disambiguationData":[OSD([sQuery(id+"F6.wireOp",EDGE,"E9.75.0")])],"isStart":true})});
            var Q76;
            Q76=makeQuery(id+"F7.boolean.opBoolean","COPY",EDGE,{"derivedFrom":makeQuery(id+"F7.opExtrude","CAP_EDGE",EDGE,{"disambiguationData":[OSD([sQuery(id+"F6.wireOp",EDGE,"E9.76.0")])],"isStart":true})});
            var Q77;
            Q77=makeQuery(id+"F7.boolean.opBoolean","COPY",EDGE,{"derivedFrom":makeQuery(id+"F7.opExtrude","CAP_EDGE",EDGE,{"disambiguationData":[OSD([sQuery(id+"F6.wireOp",EDGE,"E9.77.0")])],"isStart":true})});
            var Q78;
            Q78=makeQuery(id+"F7.boolean.opBoolean","COPY",EDGE,{"derivedFrom":makeQuery(id+"F7.opExtrude","CAP_EDGE",EDGE,{"disambiguationData":[OSD([sQuery(id+"F6.wireOp",EDGE,"E9.78.0")])],"isStart":true})});
            var Q79;
            Q79=makeQuery(id+"F7.boolean.opBoolean","COPY",EDGE,{"derivedFrom":makeQuery(id+"F7.opExtrude","CAP_EDGE",EDGE,{"disambiguationData":[OSD([sQuery(id+"F6.wireOp",EDGE,"E9.79.0")])],"isStart":true})});
            fillet(context, id + "F8", {"entities" : qUnion([Q0, Q1, Q2, Q3, Q4, Q5, Q6, Q7, Q8, Q9, Q10, Q11, Q12, Q13, Q14, Q15, Q16, Q17, Q18, Q19, Q20, Q21, Q22, Q23, Q24, Q25, Q26, Q27, Q28, Q29, Q30, Q31, Q32, Q33, Q34, Q35, Q36, Q37, Q38, Q39, Q40, Q41, Q42, Q43, Q44, Q45, Q46, Q47, Q48, Q49, Q50, Q51, Q52, Q53, Q54, Q55, Q56, Q57, Q58, Q59, Q60, Q61, Q62, Q63, Q64, Q65, Q66, Q67, Q68, Q69, Q70, Q71, Q72, Q73, Q74, Q75, Q76, Q77, Q78, Q79]), "radius" : 1 * mm, "tangentPropagation" : true, "allowEdgeOverflow" : false});
        }
        {
            var Q0;
            Q0=makeQuery(id+"F7.boolean.opBoolean","COPY",EDGE,{"derivedFrom":makeQuery(id+"F7.opExtrude","CAP_EDGE",EDGE,{"disambiguationData":[OSD([sQuery(id+"F6.wireOp",EDGE,"E9.77.0")])],"isStart":false})});
            var Q1;
            Q1=makeQuery(id+"F7.boolean.opBoolean","COPY",EDGE,{"derivedFrom":makeQuery(id+"F7.opExtrude","CAP_EDGE",EDGE,{"disambiguationData":[OSD([sQuery(id+"F6.wireOp",EDGE,"E9.78.0")])],"isStart":false})});
            var Q2;
            Q2=makeQuery(id+"F7.boolean.opBoolean","COPY",EDGE,{"derivedFrom":makeQuery(id+"F7.opExtrude","CAP_EDGE",EDGE,{"disambiguationData":[OSD([sQuery(id+"F6.wireOp",EDGE,"E9.76.0")])],"isStart":false})});
            var Q3;
            Q3=makeQuery(id+"F7.boolean.opBoolean","COPY",EDGE,{"derivedFrom":makeQuery(id+"F7.opExtrude","CAP_EDGE",EDGE,{"disambiguationData":[OSD([sQuery(id+"F6.wireOp",EDGE,"E9.75.0")])],"isStart":false})});
            var Q4;
            Q4=makeQuery(id+"F7.boolean.opBoolean","COPY",EDGE,{"derivedFrom":makeQuery(id+"F7.opExtrude","CAP_EDGE",EDGE,{"disambiguationData":[OSD([sQuery(id+"F6.wireOp",EDGE,"E9.73.0")])],"isStart":false})});
            var Q5;
            Q5=makeQuery(id+"F7.boolean.opBoolean","COPY",EDGE,{"derivedFrom":makeQuery(id+"F7.opExtrude","CAP_EDGE",EDGE,{"disambiguationData":[OSD([sQuery(id+"F6.wireOp",EDGE,"E9.71.0")])],"isStart":false})});
            var Q6;
            Q6=makeQuery(id+"F7.boolean.opBoolean","COPY",EDGE,{"derivedFrom":makeQuery(id+"F7.opExtrude","CAP_EDGE",EDGE,{"disambiguationData":[OSD([sQuery(id+"F6.wireOp",EDGE,"E9.69.0")])],"isStart":false})});
            var Q7;
            Q7=makeQuery(id+"F7.boolean.opBoolean","COPY",EDGE,{"derivedFrom":makeQuery(id+"F7.opExtrude","CAP_EDGE",EDGE,{"disambiguationData":[OSD([sQuery(id+"F6.wireOp",EDGE,"E9.67.0")])],"isStart":false})});
            var Q8;
            Q8=makeQuery(id+"F7.boolean.opBoolean","COPY",EDGE,{"derivedFrom":makeQuery(id+"F7.opExtrude","CAP_EDGE",EDGE,{"disambiguationData":[OSD([sQuery(id+"F6.wireOp",EDGE,"E9.65.0")])],"isStart":false})});
            var Q9;
            Q9=makeQuery(id+"F7.boolean.opBoolean","COPY",EDGE,{"derivedFrom":makeQuery(id+"F7.opExtrude","CAP_EDGE",EDGE,{"disambiguationData":[OSD([sQuery(id+"F6.wireOp",EDGE,"E9.63.0")])],"isStart":false})});
            var Q10;
            Q10=makeQuery(id+"F7.boolean.opBoolean","COPY",EDGE,{"derivedFrom":makeQuery(id+"F7.opExtrude","CAP_EDGE",EDGE,{"disambiguationData":[OSD([sQuery(id+"F6.wireOp",EDGE,"E9.61.0")])],"isStart":false})});
            var Q11;
            Q11=makeQuery(id+"F7.boolean.opBoolean","COPY",EDGE,{"derivedFrom":makeQuery(id+"F7.opExtrude","CAP_EDGE",EDGE,{"disambiguationData":[OSD([sQuery(id+"F6.wireOp",EDGE,"E9.59.0")])],"isStart":false})});
            var Q12;
            Q12=makeQuery(id+"F7.boolean.opBoolean","COPY",EDGE,{"derivedFrom":makeQuery(id+"F7.opExtrude","CAP_EDGE",EDGE,{"disambiguationData":[OSD([sQuery(id+"F6.wireOp",EDGE,"E9.57.0")])],"isStart":false})});
            var Q13;
            Q13=makeQuery(id+"F7.boolean.opBoolean","COPY",EDGE,{"derivedFrom":makeQuery(id+"F7.opExtrude","CAP_EDGE",EDGE,{"disambiguationData":[OSD([sQuery(id+"F6.wireOp",EDGE,"E9.55.0")])],"isStart":false})});
            var Q14;
            Q14=makeQuery(id+"F7.boolean.opBoolean","COPY",EDGE,{"derivedFrom":makeQuery(id+"F7.opExtrude","CAP_EDGE",EDGE,{"disambiguationData":[OSD([sQuery(id+"F6.wireOp",EDGE,"E9.53.0")])],"isStart":false})});
            var Q15;
            Q15=makeQuery(id+"F7.boolean.opBoolean","COPY",EDGE,{"derivedFrom":makeQuery(id+"F7.opExtrude","CAP_EDGE",EDGE,{"disambiguationData":[OSD([sQuery(id+"F6.wireOp",EDGE,"E9.51.0")])],"isStart":false})});
            var Q16;
            Q16=makeQuery(id+"F7.boolean.opBoolean","COPY",EDGE,{"derivedFrom":makeQuery(id+"F7.opExtrude","CAP_EDGE",EDGE,{"disambiguationData":[OSD([sQuery(id+"F6.wireOp",EDGE,"E9.49.0")])],"isStart":false})});
            var Q17;
            Q17=makeQuery(id+"F7.boolean.opBoolean","COPY",EDGE,{"derivedFrom":makeQuery(id+"F7.opExtrude","CAP_EDGE",EDGE,{"disambiguationData":[OSD([sQuery(id+"F6.wireOp",EDGE,"E9.47.0")])],"isStart":false})});
            var Q18;
            Q18=makeQuery(id+"F7.boolean.opBoolean","COPY",EDGE,{"derivedFrom":makeQuery(id+"F7.opExtrude","CAP_EDGE",EDGE,{"disambiguationData":[OSD([sQuery(id+"F6.wireOp",EDGE,"E9.45.0")])],"isStart":false})});
            var Q19;
            Q19=makeQuery(id+"F7.boolean.opBoolean","COPY",EDGE,{"derivedFrom":makeQuery(id+"F7.opExtrude","CAP_EDGE",EDGE,{"disambiguationData":[OSD([sQuery(id+"F6.wireOp",EDGE,"E9.43.0")])],"isStart":false})});
            var Q20;
            Q20=makeQuery(id+"F7.boolean.opBoolean","COPY",EDGE,{"derivedFrom":makeQuery(id+"F7.opExtrude","CAP_EDGE",EDGE,{"disambiguationData":[OSD([sQuery(id+"F6.wireOp",EDGE,"E9.41.0")])],"isStart":false})});
            var Q21;
            Q21=makeQuery(id+"F7.boolean.opBoolean","COPY",EDGE,{"derivedFrom":makeQuery(id+"F7.opExtrude","CAP_EDGE",EDGE,{"disambiguationData":[OSD([sQuery(id+"F6.wireOp",EDGE,"E9.39.0")])],"isStart":false})});
            var Q22;
            Q22=makeQuery(id+"F7.boolean.opBoolean","COPY",EDGE,{"derivedFrom":makeQuery(id+"F7.opExtrude","CAP_EDGE",EDGE,{"disambiguationData":[OSD([sQuery(id+"F6.wireOp",EDGE,"E9.37.0")])],"isStart":false})});
            var Q23;
            Q23=makeQuery(id+"F7.boolean.opBoolean","COPY",EDGE,{"derivedFrom":makeQuery(id+"F7.opExtrude","CAP_EDGE",EDGE,{"disambiguationData":[OSD([sQuery(id+"F6.wireOp",EDGE,"E9.35.0")])],"isStart":false})});
            var Q24;
            Q24=makeQuery(id+"F7.boolean.opBoolean","COPY",EDGE,{"derivedFrom":makeQuery(id+"F7.opExtrude","CAP_EDGE",EDGE,{"disambiguationData":[OSD([sQuery(id+"F6.wireOp",EDGE,"E9.33.0")])],"isStart":false})});
            var Q25;
            Q25=makeQuery(id+"F7.boolean.opBoolean","COPY",EDGE,{"derivedFrom":makeQuery(id+"F7.opExtrude","CAP_EDGE",EDGE,{"disambiguationData":[OSD([sQuery(id+"F6.wireOp",EDGE,"E9.31.0")])],"isStart":false})});
            var Q26;
            Q26=makeQuery(id+"F7.boolean.opBoolean","COPY",EDGE,{"derivedFrom":makeQuery(id+"F7.opExtrude","CAP_EDGE",EDGE,{"disambiguationData":[OSD([sQuery(id+"F6.wireOp",EDGE,"E9.29.0")])],"isStart":false})});
            var Q27;
            Q27=makeQuery(id+"F7.boolean.opBoolean","COPY",EDGE,{"derivedFrom":makeQuery(id+"F7.opExtrude","CAP_EDGE",EDGE,{"disambiguationData":[OSD([sQuery(id+"F6.wireOp",EDGE,"E9.27.0")])],"isStart":false})});
            var Q28;
            Q28=makeQuery(id+"F7.boolean.opBoolean","COPY",EDGE,{"derivedFrom":makeQuery(id+"F7.opExtrude","CAP_EDGE",EDGE,{"disambiguationData":[OSD([sQuery(id+"F6.wireOp",EDGE,"E9.25.0")])],"isStart":false})});
            var Q29;
            Q29=makeQuery(id+"F7.boolean.opBoolean","COPY",EDGE,{"derivedFrom":makeQuery(id+"F7.opExtrude","CAP_EDGE",EDGE,{"disambiguationData":[OSD([sQuery(id+"F6.wireOp",EDGE,"E9.23.0")])],"isStart":false})});
            var Q30;
            Q30=makeQuery(id+"F7.boolean.opBoolean","COPY",EDGE,{"derivedFrom":makeQuery(id+"F7.opExtrude","CAP_EDGE",EDGE,{"disambiguationData":[OSD([sQuery(id+"F6.wireOp",EDGE,"E9.21.0")])],"isStart":false})});
            var Q31;
            Q31=makeQuery(id+"F7.boolean.opBoolean","COPY",EDGE,{"derivedFrom":makeQuery(id+"F7.opExtrude","CAP_EDGE",EDGE,{"disambiguationData":[OSD([sQuery(id+"F6.wireOp",EDGE,"E9.19.0")])],"isStart":false})});
            var Q32;
            Q32=makeQuery(id+"F7.boolean.opBoolean","COPY",EDGE,{"derivedFrom":makeQuery(id+"F7.opExtrude","CAP_EDGE",EDGE,{"disambiguationData":[OSD([sQuery(id+"F6.wireOp",EDGE,"E9.17.0")])],"isStart":false})});
            var Q33;
            Q33=makeQuery(id+"F7.boolean.opBoolean","COPY",EDGE,{"derivedFrom":makeQuery(id+"F7.opExtrude","CAP_EDGE",EDGE,{"disambiguationData":[OSD([sQuery(id+"F6.wireOp",EDGE,"E9.15.0")])],"isStart":false})});
            var Q34;
            Q34=makeQuery(id+"F7.boolean.opBoolean","COPY",EDGE,{"derivedFrom":makeQuery(id+"F7.opExtrude","CAP_EDGE",EDGE,{"disambiguationData":[OSD([sQuery(id+"F6.wireOp",EDGE,"E9.13.0")])],"isStart":false})});
            var Q35;
            Q35=makeQuery(id+"F7.boolean.opBoolean","COPY",EDGE,{"derivedFrom":makeQuery(id+"F7.opExtrude","CAP_EDGE",EDGE,{"disambiguationData":[OSD([sQuery(id+"F6.wireOp",EDGE,"E9.11.0")])],"isStart":false})});
            var Q36;
            Q36=makeQuery(id+"F7.boolean.opBoolean","COPY",EDGE,{"derivedFrom":makeQuery(id+"F7.opExtrude","CAP_EDGE",EDGE,{"disambiguationData":[OSD([sQuery(id+"F6.wireOp",EDGE,"E9.9.0")])],"isStart":false})});
            var Q37;
            Q37=makeQuery(id+"F7.boolean.opBoolean","COPY",EDGE,{"derivedFrom":makeQuery(id+"F7.opExtrude","CAP_EDGE",EDGE,{"disambiguationData":[OSD([sQuery(id+"F6.wireOp",EDGE,"E9.7.0")])],"isStart":false})});
            var Q38;
            Q38=makeQuery(id+"F7.boolean.opBoolean","COPY",EDGE,{"derivedFrom":makeQuery(id+"F7.opExtrude","CAP_EDGE",EDGE,{"disambiguationData":[OSD([sQuery(id+"F6.wireOp",EDGE,"E9.5.0")])],"isStart":false})});
            var Q39;
            Q39=makeQuery(id+"F7.boolean.opBoolean","COPY",EDGE,{"derivedFrom":makeQuery(id+"F7.opExtrude","CAP_EDGE",EDGE,{"disambiguationData":[OSD([sQuery(id+"F6.wireOp",EDGE,"E9.3.0")])],"isStart":false})});
            var Q40;
            Q40=makeQuery(id+"F7.boolean.opBoolean","COPY",EDGE,{"derivedFrom":makeQuery(id+"F7.opExtrude","CAP_EDGE",EDGE,{"disambiguationData":[OSD([sQuery(id+"F6.wireOp",EDGE,"E9.1.0")])],"isStart":false})});
            var Q41;
            Q41=makeQuery(id+"F7.boolean.opBoolean","COPY",EDGE,{"derivedFrom":makeQuery(id+"F7.opExtrude","CAP_EDGE",EDGE,{"disambiguationData":[OSD([sQuery(id+"F6.wireOp",EDGE,"E8")])],"isStart":false})});
            var Q42;
            Q42=makeQuery(id+"F7.boolean.opBoolean","COPY",EDGE,{"derivedFrom":makeQuery(id+"F7.opExtrude","CAP_EDGE",EDGE,{"disambiguationData":[OSD([sQuery(id+"F6.wireOp",EDGE,"E9.2.0")])],"isStart":false})});
            var Q43;
            Q43=makeQuery(id+"F7.boolean.opBoolean","COPY",EDGE,{"derivedFrom":makeQuery(id+"F7.opExtrude","CAP_EDGE",EDGE,{"disambiguationData":[OSD([sQuery(id+"F6.wireOp",EDGE,"E9.4.0")])],"isStart":false})});
            var Q44;
            Q44=makeQuery(id+"F7.boolean.opBoolean","COPY",EDGE,{"derivedFrom":makeQuery(id+"F7.opExtrude","CAP_EDGE",EDGE,{"disambiguationData":[OSD([sQuery(id+"F6.wireOp",EDGE,"E9.6.0")])],"isStart":false})});
            var Q45;
            Q45=makeQuery(id+"F7.boolean.opBoolean","COPY",EDGE,{"derivedFrom":makeQuery(id+"F7.opExtrude","CAP_EDGE",EDGE,{"disambiguationData":[OSD([sQuery(id+"F6.wireOp",EDGE,"E9.8.0")])],"isStart":false})});
            var Q46;
            Q46=makeQuery(id+"F7.boolean.opBoolean","COPY",EDGE,{"derivedFrom":makeQuery(id+"F7.opExtrude","CAP_EDGE",EDGE,{"disambiguationData":[OSD([sQuery(id+"F6.wireOp",EDGE,"E9.10.0")])],"isStart":false})});
            var Q47;
            Q47=makeQuery(id+"F7.boolean.opBoolean","COPY",EDGE,{"derivedFrom":makeQuery(id+"F7.opExtrude","CAP_EDGE",EDGE,{"disambiguationData":[OSD([sQuery(id+"F6.wireOp",EDGE,"E9.12.0")])],"isStart":false})});
            var Q48;
            Q48=makeQuery(id+"F7.boolean.opBoolean","COPY",EDGE,{"derivedFrom":makeQuery(id+"F7.opExtrude","CAP_EDGE",EDGE,{"disambiguationData":[OSD([sQuery(id+"F6.wireOp",EDGE,"E9.14.0")])],"isStart":false})});
            var Q49;
            Q49=makeQuery(id+"F7.boolean.opBoolean","COPY",EDGE,{"derivedFrom":makeQuery(id+"F7.opExtrude","CAP_EDGE",EDGE,{"disambiguationData":[OSD([sQuery(id+"F6.wireOp",EDGE,"E9.16.0")])],"isStart":false})});
            var Q50;
            Q50=makeQuery(id+"F7.boolean.opBoolean","COPY",EDGE,{"derivedFrom":makeQuery(id+"F7.opExtrude","CAP_EDGE",EDGE,{"disambiguationData":[OSD([sQuery(id+"F6.wireOp",EDGE,"E9.18.0")])],"isStart":false})});
            var Q51;
            Q51=makeQuery(id+"F7.boolean.opBoolean","COPY",EDGE,{"derivedFrom":makeQuery(id+"F7.opExtrude","CAP_EDGE",EDGE,{"disambiguationData":[OSD([sQuery(id+"F6.wireOp",EDGE,"E9.20.0")])],"isStart":false})});
            var Q52;
            Q52=makeQuery(id+"F7.boolean.opBoolean","COPY",EDGE,{"derivedFrom":makeQuery(id+"F7.opExtrude","CAP_EDGE",EDGE,{"disambiguationData":[OSD([sQuery(id+"F6.wireOp",EDGE,"E9.22.0")])],"isStart":false})});
            var Q53;
            Q53=makeQuery(id+"F7.boolean.opBoolean","COPY",EDGE,{"derivedFrom":makeQuery(id+"F7.opExtrude","CAP_EDGE",EDGE,{"disambiguationData":[OSD([sQuery(id+"F6.wireOp",EDGE,"E9.24.0")])],"isStart":false})});
            var Q54;
            Q54=makeQuery(id+"F7.boolean.opBoolean","COPY",EDGE,{"derivedFrom":makeQuery(id+"F7.opExtrude","CAP_EDGE",EDGE,{"disambiguationData":[OSD([sQuery(id+"F6.wireOp",EDGE,"E9.26.0")])],"isStart":false})});
            var Q55;
            Q55=makeQuery(id+"F7.boolean.opBoolean","COPY",EDGE,{"derivedFrom":makeQuery(id+"F7.opExtrude","CAP_EDGE",EDGE,{"disambiguationData":[OSD([sQuery(id+"F6.wireOp",EDGE,"E9.28.0")])],"isStart":false})});
            var Q56;
            Q56=makeQuery(id+"F7.boolean.opBoolean","COPY",EDGE,{"derivedFrom":makeQuery(id+"F7.opExtrude","CAP_EDGE",EDGE,{"disambiguationData":[OSD([sQuery(id+"F6.wireOp",EDGE,"E9.30.0")])],"isStart":false})});
            var Q57;
            Q57=makeQuery(id+"F7.boolean.opBoolean","COPY",EDGE,{"derivedFrom":makeQuery(id+"F7.opExtrude","CAP_EDGE",EDGE,{"disambiguationData":[OSD([sQuery(id+"F6.wireOp",EDGE,"E9.32.0")])],"isStart":false})});
            var Q58;
            Q58=makeQuery(id+"F7.boolean.opBoolean","COPY",EDGE,{"derivedFrom":makeQuery(id+"F7.opExtrude","CAP_EDGE",EDGE,{"disambiguationData":[OSD([sQuery(id+"F6.wireOp",EDGE,"E9.34.0")])],"isStart":false})});
            var Q59;
            Q59=makeQuery(id+"F7.boolean.opBoolean","COPY",EDGE,{"derivedFrom":makeQuery(id+"F7.opExtrude","CAP_EDGE",EDGE,{"disambiguationData":[OSD([sQuery(id+"F6.wireOp",EDGE,"E9.36.0")])],"isStart":false})});
            var Q60;
            Q60=makeQuery(id+"F7.boolean.opBoolean","COPY",EDGE,{"derivedFrom":makeQuery(id+"F7.opExtrude","CAP_EDGE",EDGE,{"disambiguationData":[OSD([sQuery(id+"F6.wireOp",EDGE,"E9.38.0")])],"isStart":false})});
            var Q61;
            Q61=makeQuery(id+"F7.boolean.opBoolean","COPY",EDGE,{"derivedFrom":makeQuery(id+"F7.opExtrude","CAP_EDGE",EDGE,{"disambiguationData":[OSD([sQuery(id+"F6.wireOp",EDGE,"E9.40.0")])],"isStart":false})});
            var Q62;
            Q62=makeQuery(id+"F7.boolean.opBoolean","COPY",EDGE,{"derivedFrom":makeQuery(id+"F7.opExtrude","CAP_EDGE",EDGE,{"disambiguationData":[OSD([sQuery(id+"F6.wireOp",EDGE,"E9.42.0")])],"isStart":false})});
            var Q63;
            Q63=makeQuery(id+"F7.boolean.opBoolean","COPY",EDGE,{"derivedFrom":makeQuery(id+"F7.opExtrude","CAP_EDGE",EDGE,{"disambiguationData":[OSD([sQuery(id+"F6.wireOp",EDGE,"E9.44.0")])],"isStart":false})});
            var Q64;
            Q64=makeQuery(id+"F7.boolean.opBoolean","COPY",EDGE,{"derivedFrom":makeQuery(id+"F7.opExtrude","CAP_EDGE",EDGE,{"disambiguationData":[OSD([sQuery(id+"F6.wireOp",EDGE,"E9.46.0")])],"isStart":false})});
            var Q65;
            Q65=makeQuery(id+"F7.boolean.opBoolean","COPY",EDGE,{"derivedFrom":makeQuery(id+"F7.opExtrude","CAP_EDGE",EDGE,{"disambiguationData":[OSD([sQuery(id+"F6.wireOp",EDGE,"E9.48.0")])],"isStart":false})});
            var Q66;
            Q66=makeQuery(id+"F7.boolean.opBoolean","COPY",EDGE,{"derivedFrom":makeQuery(id+"F7.opExtrude","CAP_EDGE",EDGE,{"disambiguationData":[OSD([sQuery(id+"F6.wireOp",EDGE,"E9.50.0")])],"isStart":false})});
            var Q67;
            Q67=makeQuery(id+"F7.boolean.opBoolean","COPY",EDGE,{"derivedFrom":makeQuery(id+"F7.opExtrude","CAP_EDGE",EDGE,{"disambiguationData":[OSD([sQuery(id+"F6.wireOp",EDGE,"E9.52.0")])],"isStart":false})});
            var Q68;
            Q68=makeQuery(id+"F7.boolean.opBoolean","COPY",EDGE,{"derivedFrom":makeQuery(id+"F7.opExtrude","CAP_EDGE",EDGE,{"disambiguationData":[OSD([sQuery(id+"F6.wireOp",EDGE,"E9.54.0")])],"isStart":false})});
            var Q69;
            Q69=makeQuery(id+"F7.boolean.opBoolean","COPY",EDGE,{"derivedFrom":makeQuery(id+"F7.opExtrude","CAP_EDGE",EDGE,{"disambiguationData":[OSD([sQuery(id+"F6.wireOp",EDGE,"E9.56.0")])],"isStart":false})});
            var Q70;
            Q70=makeQuery(id+"F7.boolean.opBoolean","COPY",EDGE,{"derivedFrom":makeQuery(id+"F7.opExtrude","CAP_EDGE",EDGE,{"disambiguationData":[OSD([sQuery(id+"F6.wireOp",EDGE,"E9.58.0")])],"isStart":false})});
            var Q71;
            Q71=makeQuery(id+"F7.boolean.opBoolean","COPY",EDGE,{"derivedFrom":makeQuery(id+"F7.opExtrude","CAP_EDGE",EDGE,{"disambiguationData":[OSD([sQuery(id+"F6.wireOp",EDGE,"E9.60.0")])],"isStart":false})});
            var Q72;
            Q72=makeQuery(id+"F7.boolean.opBoolean","COPY",EDGE,{"derivedFrom":makeQuery(id+"F7.opExtrude","CAP_EDGE",EDGE,{"disambiguationData":[OSD([sQuery(id+"F6.wireOp",EDGE,"E9.62.0")])],"isStart":false})});
            var Q73;
            Q73=makeQuery(id+"F7.boolean.opBoolean","COPY",EDGE,{"derivedFrom":makeQuery(id+"F7.opExtrude","CAP_EDGE",EDGE,{"disambiguationData":[OSD([sQuery(id+"F6.wireOp",EDGE,"E9.64.0")])],"isStart":false})});
            var Q74;
            Q74=makeQuery(id+"F7.boolean.opBoolean","COPY",EDGE,{"derivedFrom":makeQuery(id+"F7.opExtrude","CAP_EDGE",EDGE,{"disambiguationData":[OSD([sQuery(id+"F6.wireOp",EDGE,"E9.66.0")])],"isStart":false})});
            var Q75;
            Q75=makeQuery(id+"F7.boolean.opBoolean","COPY",EDGE,{"derivedFrom":makeQuery(id+"F7.opExtrude","CAP_EDGE",EDGE,{"disambiguationData":[OSD([sQuery(id+"F6.wireOp",EDGE,"E9.68.0")])],"isStart":false})});
            var Q76;
            Q76=makeQuery(id+"F7.boolean.opBoolean","COPY",EDGE,{"derivedFrom":makeQuery(id+"F7.opExtrude","CAP_EDGE",EDGE,{"disambiguationData":[OSD([sQuery(id+"F6.wireOp",EDGE,"E9.70.0")])],"isStart":false})});
            var Q77;
            Q77=makeQuery(id+"F7.boolean.opBoolean","COPY",EDGE,{"derivedFrom":makeQuery(id+"F7.opExtrude","CAP_EDGE",EDGE,{"disambiguationData":[OSD([sQuery(id+"F6.wireOp",EDGE,"E9.72.0")])],"isStart":false})});
            var Q78;
            Q78=makeQuery(id+"F7.boolean.opBoolean","COPY",EDGE,{"derivedFrom":makeQuery(id+"F7.opExtrude","CAP_EDGE",EDGE,{"disambiguationData":[OSD([sQuery(id+"F6.wireOp",EDGE,"E9.74.0")])],"isStart":false})});
            var Q79;
            Q79=makeQuery(id+"F7.boolean.opBoolean","COPY",EDGE,{"derivedFrom":makeQuery(id+"F7.opExtrude","CAP_EDGE",EDGE,{"disambiguationData":[OSD([sQuery(id+"F6.wireOp",EDGE,"E9.79.0")])],"isStart":false})});
            fillet(context, id + "F9", {"entities" : qUnion([Q0, Q1, Q2, Q3, Q4, Q5, Q6, Q7, Q8, Q9, Q10, Q11, Q12, Q13, Q14, Q15, Q16, Q17, Q18, Q19, Q20, Q21, Q22, Q23, Q24, Q25, Q26, Q27, Q28, Q29, Q30, Q31, Q32, Q33, Q34, Q35, Q36, Q37, Q38, Q39, Q40, Q41, Q42, Q43, Q44, Q45, Q46, Q47, Q48, Q49, Q50, Q51, Q52, Q53, Q54, Q55, Q56, Q57, Q58, Q59, Q60, Q61, Q62, Q63, Q64, Q65, Q66, Q67, Q68, Q69, Q70, Q71, Q72, Q73, Q74, Q75, Q76, Q77, Q78, Q79]), "radius" : 1 * mm, "tangentPropagation" : true, "allowEdgeOverflow" : false});
        }
        {
            var Q0;
            {var subQ0=sQuery(id+"F3.wireOp",EDGE,"E6.right");var subQ1=sQuery(id+"F3.wireOp",EDGE,"E6.top");var subQ2=sQuery(id+"F3.wireOp",EDGE,"E6.bottom");var subQ3=sQuery(id+"F3.wireOp",EDGE,"E5.right");var subQ4=sQuery(id+"F3.wireOp",EDGE,"E5.top");var subQ5=sQuery(id+"F3.wireOp",EDGE,"E5.bottom");var subQ6=sQuery(id+"F3.wireOp",EDGE,"E4");var subQ7=sQuery(id+"F3.wireOp",EDGE,"E3");var subQ8=makeQuery(id+"F5.opFillet","BLEND_EDGE",EDGE,{"blendedFrom":[makeQuery(id+"F4.opExtrude","CAP_EDGE",EDGE,{"disambiguationData":[OSD([subQ5])],"isStart":false}),makeQuery(id+"F4.opExtrude","CAP_FACE",FACE,{"disambiguationData":[OSD([subQ7,subQ6,subQ5,subQ4,subQ3,subQ2,subQ1,subQ0])],"isStart":false})],"blendedInto":[makeQuery(id+"F4.opExtrude","CAP_FACE",FACE,{"disambiguationData":[OSD([subQ7,subQ6,subQ5,subQ4,subQ3,subQ2,subQ1,subQ0])],"isStart":false})]});Q0=makeQuery(id+"F7.boolean.opBoolean","MERGE",EDGE,{"derivedFrom":[subQ8,makeQuery(id+"F7.opExtrude","CAP_EDGE",EDGE,{"disambiguationData":[OSD([subQ7,subQ6,subQ5,subQ4,subQ3,subQ2,subQ1,subQ0]),TDD([makeQuery(id+"F6.imprint","IMPRINT",EDGE,{"derivedFrom":subQ8})])],"isStart":true})]});}
            var Q1;
            {var subQ0=sQuery(id+"F3.wireOp",EDGE,"E6.right");var subQ1=sQuery(id+"F3.wireOp",EDGE,"E6.top");var subQ2=sQuery(id+"F3.wireOp",EDGE,"E6.bottom");var subQ3=sQuery(id+"F3.wireOp",EDGE,"E5.right");var subQ4=sQuery(id+"F3.wireOp",EDGE,"E5.top");var subQ5=sQuery(id+"F3.wireOp",EDGE,"E5.bottom");var subQ6=sQuery(id+"F3.wireOp",EDGE,"E4");var subQ7=sQuery(id+"F3.wireOp",EDGE,"E3");var subQ8=makeQuery(id+"F5.opFillet","BLEND_EDGE",EDGE,{"blendedFrom":[makeQuery(id+"F4.opExtrude","CAP_EDGE",EDGE,{"disambiguationData":[OSD([subQ6])],"isStart":false}),makeQuery(id+"F4.opExtrude","CAP_FACE",FACE,{"disambiguationData":[OSD([subQ7,subQ6,subQ5,subQ4,subQ3,subQ2,subQ1,subQ0])],"isStart":false})],"blendedInto":[makeQuery(id+"F4.opExtrude","CAP_FACE",FACE,{"disambiguationData":[OSD([subQ7,subQ6,subQ5,subQ4,subQ3,subQ2,subQ1,subQ0])],"isStart":false})]});Q1=makeQuery(id+"F7.boolean.opBoolean","MERGE",EDGE,{"derivedFrom":[subQ8,makeQuery(id+"F7.opExtrude","CAP_EDGE",EDGE,{"disambiguationData":[OSD([subQ7,subQ6,subQ5,subQ4,subQ3,subQ2,subQ1,subQ0]),TDD([makeQuery(id+"F6.imprint","IMPRINT",EDGE,{"disambiguationData":[TD([[makeQuery(id+"F6.imprint","INTERSECT",VERTEX,{"derivedFrom":[subQ8,sQuery(id+"F6.wireOp",EDGE,"E9.1.0")]}),-1.0]])],"derivedFrom":subQ8})])],"isStart":true})]});}
            var Q2;
            {var subQ0=sQuery(id+"F3.wireOp",EDGE,"E6.right");var subQ1=sQuery(id+"F3.wireOp",EDGE,"E6.top");var subQ2=sQuery(id+"F3.wireOp",EDGE,"E6.bottom");var subQ3=sQuery(id+"F3.wireOp",EDGE,"E5.right");var subQ4=sQuery(id+"F3.wireOp",EDGE,"E5.top");var subQ5=sQuery(id+"F3.wireOp",EDGE,"E5.bottom");var subQ6=sQuery(id+"F3.wireOp",EDGE,"E4");var subQ7=sQuery(id+"F3.wireOp",EDGE,"E3");var subQ8=makeQuery(id+"F5.opFillet","BLEND_EDGE",EDGE,{"blendedFrom":[makeQuery(id+"F4.opExtrude","CAP_EDGE",EDGE,{"disambiguationData":[OSD([subQ6])],"isStart":false}),makeQuery(id+"F4.opExtrude","CAP_FACE",FACE,{"disambiguationData":[OSD([subQ7,subQ6,subQ5,subQ4,subQ3,subQ2,subQ1,subQ0])],"isStart":false})],"blendedInto":[makeQuery(id+"F4.opExtrude","CAP_FACE",FACE,{"disambiguationData":[OSD([subQ7,subQ6,subQ5,subQ4,subQ3,subQ2,subQ1,subQ0])],"isStart":false})]});Q2=makeQuery(id+"F7.boolean.opBoolean","MERGE",EDGE,{"derivedFrom":[subQ8,makeQuery(id+"F7.opExtrude","CAP_EDGE",EDGE,{"disambiguationData":[OSD([subQ7,subQ6,subQ5,subQ4,subQ3,subQ2,subQ1,subQ0]),TDD([makeQuery(id+"F6.imprint","IMPRINT",EDGE,{"disambiguationData":[TD([[makeQuery(id+"F6.imprint","INTERSECT",VERTEX,{"derivedFrom":[subQ8,sQuery(id+"F6.wireOp",EDGE,"E9.3.0")]}),-1.0]])],"derivedFrom":subQ8})])],"isStart":true})]});}
            var Q3;
            {var subQ0=sQuery(id+"F3.wireOp",EDGE,"E6.right");var subQ1=sQuery(id+"F3.wireOp",EDGE,"E6.top");var subQ2=sQuery(id+"F3.wireOp",EDGE,"E6.bottom");var subQ3=sQuery(id+"F3.wireOp",EDGE,"E5.right");var subQ4=sQuery(id+"F3.wireOp",EDGE,"E5.top");var subQ5=sQuery(id+"F3.wireOp",EDGE,"E5.bottom");var subQ6=sQuery(id+"F3.wireOp",EDGE,"E4");var subQ7=sQuery(id+"F3.wireOp",EDGE,"E3");var subQ8=makeQuery(id+"F5.opFillet","BLEND_EDGE",EDGE,{"blendedFrom":[makeQuery(id+"F4.opExtrude","CAP_EDGE",EDGE,{"disambiguationData":[OSD([subQ6])],"isStart":false}),makeQuery(id+"F4.opExtrude","CAP_FACE",FACE,{"disambiguationData":[OSD([subQ7,subQ6,subQ5,subQ4,subQ3,subQ2,subQ1,subQ0])],"isStart":false})],"blendedInto":[makeQuery(id+"F4.opExtrude","CAP_FACE",FACE,{"disambiguationData":[OSD([subQ7,subQ6,subQ5,subQ4,subQ3,subQ2,subQ1,subQ0])],"isStart":false})]});Q3=makeQuery(id+"F7.boolean.opBoolean","MERGE",EDGE,{"derivedFrom":[subQ8,makeQuery(id+"F7.opExtrude","CAP_EDGE",EDGE,{"disambiguationData":[OSD([subQ7,subQ6,subQ5,subQ4,subQ3,subQ2,subQ1,subQ0]),TDD([makeQuery(id+"F6.imprint","IMPRINT",EDGE,{"disambiguationData":[TD([[makeQuery(id+"F6.imprint","INTERSECT",VERTEX,{"derivedFrom":[subQ8,sQuery(id+"F6.wireOp",EDGE,"E9.5.0")]}),-1.0]])],"derivedFrom":subQ8})])],"isStart":true})]});}
            var Q4;
            {var subQ0=sQuery(id+"F3.wireOp",EDGE,"E6.right");var subQ1=sQuery(id+"F3.wireOp",EDGE,"E6.top");var subQ2=sQuery(id+"F3.wireOp",EDGE,"E6.bottom");var subQ3=sQuery(id+"F3.wireOp",EDGE,"E5.right");var subQ4=sQuery(id+"F3.wireOp",EDGE,"E5.top");var subQ5=sQuery(id+"F3.wireOp",EDGE,"E5.bottom");var subQ6=sQuery(id+"F3.wireOp",EDGE,"E4");var subQ7=sQuery(id+"F3.wireOp",EDGE,"E3");var subQ8=makeQuery(id+"F5.opFillet","BLEND_EDGE",EDGE,{"blendedFrom":[makeQuery(id+"F4.opExtrude","CAP_EDGE",EDGE,{"disambiguationData":[OSD([subQ6])],"isStart":false}),makeQuery(id+"F4.opExtrude","CAP_FACE",FACE,{"disambiguationData":[OSD([subQ7,subQ6,subQ5,subQ4,subQ3,subQ2,subQ1,subQ0])],"isStart":false})],"blendedInto":[makeQuery(id+"F4.opExtrude","CAP_FACE",FACE,{"disambiguationData":[OSD([subQ7,subQ6,subQ5,subQ4,subQ3,subQ2,subQ1,subQ0])],"isStart":false})]});Q4=makeQuery(id+"F7.boolean.opBoolean","MERGE",EDGE,{"derivedFrom":[subQ8,makeQuery(id+"F7.opExtrude","CAP_EDGE",EDGE,{"disambiguationData":[OSD([subQ7,subQ6,subQ5,subQ4,subQ3,subQ2,subQ1,subQ0]),TDD([makeQuery(id+"F6.imprint","IMPRINT",EDGE,{"disambiguationData":[TD([[makeQuery(id+"F6.imprint","INTERSECT",VERTEX,{"derivedFrom":[subQ8,sQuery(id+"F6.wireOp",EDGE,"E9.7.0")]}),-1.0]])],"derivedFrom":subQ8})])],"isStart":true})]});}
            var Q5;
            {var subQ0=sQuery(id+"F3.wireOp",EDGE,"E6.right");var subQ1=sQuery(id+"F3.wireOp",EDGE,"E6.top");var subQ2=sQuery(id+"F3.wireOp",EDGE,"E6.bottom");var subQ3=sQuery(id+"F3.wireOp",EDGE,"E5.right");var subQ4=sQuery(id+"F3.wireOp",EDGE,"E5.top");var subQ5=sQuery(id+"F3.wireOp",EDGE,"E5.bottom");var subQ6=sQuery(id+"F3.wireOp",EDGE,"E4");var subQ7=sQuery(id+"F3.wireOp",EDGE,"E3");var subQ8=makeQuery(id+"F5.opFillet","BLEND_EDGE",EDGE,{"blendedFrom":[makeQuery(id+"F4.opExtrude","CAP_EDGE",EDGE,{"disambiguationData":[OSD([subQ6])],"isStart":false}),makeQuery(id+"F4.opExtrude","CAP_FACE",FACE,{"disambiguationData":[OSD([subQ7,subQ6,subQ5,subQ4,subQ3,subQ2,subQ1,subQ0])],"isStart":false})],"blendedInto":[makeQuery(id+"F4.opExtrude","CAP_FACE",FACE,{"disambiguationData":[OSD([subQ7,subQ6,subQ5,subQ4,subQ3,subQ2,subQ1,subQ0])],"isStart":false})]});Q5=makeQuery(id+"F7.boolean.opBoolean","MERGE",EDGE,{"derivedFrom":[subQ8,makeQuery(id+"F7.opExtrude","CAP_EDGE",EDGE,{"disambiguationData":[OSD([subQ7,subQ6,subQ5,subQ4,subQ3,subQ2,subQ1,subQ0]),TDD([makeQuery(id+"F6.imprint","IMPRINT",EDGE,{"disambiguationData":[TD([[makeQuery(id+"F6.imprint","INTERSECT",VERTEX,{"derivedFrom":[subQ8,sQuery(id+"F6.wireOp",EDGE,"E9.9.0")]}),-1.0]])],"derivedFrom":subQ8})])],"isStart":true})]});}
            var Q6;
            {var subQ0=sQuery(id+"F3.wireOp",EDGE,"E6.right");var subQ1=sQuery(id+"F3.wireOp",EDGE,"E6.top");var subQ2=sQuery(id+"F3.wireOp",EDGE,"E6.bottom");var subQ3=sQuery(id+"F3.wireOp",EDGE,"E5.right");var subQ4=sQuery(id+"F3.wireOp",EDGE,"E5.top");var subQ5=sQuery(id+"F3.wireOp",EDGE,"E5.bottom");var subQ6=sQuery(id+"F3.wireOp",EDGE,"E4");var subQ7=sQuery(id+"F3.wireOp",EDGE,"E3");var subQ8=makeQuery(id+"F5.opFillet","BLEND_EDGE",EDGE,{"blendedFrom":[makeQuery(id+"F4.opExtrude","CAP_EDGE",EDGE,{"disambiguationData":[OSD([subQ6])],"isStart":false}),makeQuery(id+"F4.opExtrude","CAP_FACE",FACE,{"disambiguationData":[OSD([subQ7,subQ6,subQ5,subQ4,subQ3,subQ2,subQ1,subQ0])],"isStart":false})],"blendedInto":[makeQuery(id+"F4.opExtrude","CAP_FACE",FACE,{"disambiguationData":[OSD([subQ7,subQ6,subQ5,subQ4,subQ3,subQ2,subQ1,subQ0])],"isStart":false})]});Q6=makeQuery(id+"F7.boolean.opBoolean","MERGE",EDGE,{"derivedFrom":[subQ8,makeQuery(id+"F7.opExtrude","CAP_EDGE",EDGE,{"disambiguationData":[OSD([subQ7,subQ6,subQ5,subQ4,subQ3,subQ2,subQ1,subQ0]),TDD([makeQuery(id+"F6.imprint","IMPRINT",EDGE,{"disambiguationData":[TD([[makeQuery(id+"F6.imprint","INTERSECT",VERTEX,{"derivedFrom":[subQ8,sQuery(id+"F6.wireOp",EDGE,"E9.11.0")]}),-1.0]])],"derivedFrom":subQ8})])],"isStart":true})]});}
            var Q7;
            {var subQ0=sQuery(id+"F3.wireOp",EDGE,"E6.right");var subQ1=sQuery(id+"F3.wireOp",EDGE,"E6.top");var subQ2=sQuery(id+"F3.wireOp",EDGE,"E6.bottom");var subQ3=sQuery(id+"F3.wireOp",EDGE,"E5.right");var subQ4=sQuery(id+"F3.wireOp",EDGE,"E5.top");var subQ5=sQuery(id+"F3.wireOp",EDGE,"E5.bottom");var subQ6=sQuery(id+"F3.wireOp",EDGE,"E4");var subQ7=sQuery(id+"F3.wireOp",EDGE,"E3");var subQ8=makeQuery(id+"F5.opFillet","BLEND_EDGE",EDGE,{"blendedFrom":[makeQuery(id+"F4.opExtrude","CAP_EDGE",EDGE,{"disambiguationData":[OSD([subQ6])],"isStart":false}),makeQuery(id+"F4.opExtrude","CAP_FACE",FACE,{"disambiguationData":[OSD([subQ7,subQ6,subQ5,subQ4,subQ3,subQ2,subQ1,subQ0])],"isStart":false})],"blendedInto":[makeQuery(id+"F4.opExtrude","CAP_FACE",FACE,{"disambiguationData":[OSD([subQ7,subQ6,subQ5,subQ4,subQ3,subQ2,subQ1,subQ0])],"isStart":false})]});Q7=makeQuery(id+"F7.boolean.opBoolean","MERGE",EDGE,{"derivedFrom":[subQ8,makeQuery(id+"F7.opExtrude","CAP_EDGE",EDGE,{"disambiguationData":[OSD([subQ7,subQ6,subQ5,subQ4,subQ3,subQ2,subQ1,subQ0]),TDD([makeQuery(id+"F6.imprint","IMPRINT",EDGE,{"disambiguationData":[TD([[makeQuery(id+"F6.imprint","INTERSECT",VERTEX,{"derivedFrom":[subQ8,sQuery(id+"F6.wireOp",EDGE,"E9.13.0")]}),-1.0]])],"derivedFrom":subQ8})])],"isStart":true})]});}
            var Q8;
            {var subQ0=sQuery(id+"F3.wireOp",EDGE,"E6.right");var subQ1=sQuery(id+"F3.wireOp",EDGE,"E6.top");var subQ2=sQuery(id+"F3.wireOp",EDGE,"E6.bottom");var subQ3=sQuery(id+"F3.wireOp",EDGE,"E5.right");var subQ4=sQuery(id+"F3.wireOp",EDGE,"E5.top");var subQ5=sQuery(id+"F3.wireOp",EDGE,"E5.bottom");var subQ6=sQuery(id+"F3.wireOp",EDGE,"E4");var subQ7=sQuery(id+"F3.wireOp",EDGE,"E3");var subQ8=makeQuery(id+"F5.opFillet","BLEND_EDGE",EDGE,{"blendedFrom":[makeQuery(id+"F4.opExtrude","CAP_EDGE",EDGE,{"disambiguationData":[OSD([subQ6])],"isStart":false}),makeQuery(id+"F4.opExtrude","CAP_FACE",FACE,{"disambiguationData":[OSD([subQ7,subQ6,subQ5,subQ4,subQ3,subQ2,subQ1,subQ0])],"isStart":false})],"blendedInto":[makeQuery(id+"F4.opExtrude","CAP_FACE",FACE,{"disambiguationData":[OSD([subQ7,subQ6,subQ5,subQ4,subQ3,subQ2,subQ1,subQ0])],"isStart":false})]});Q8=makeQuery(id+"F7.boolean.opBoolean","MERGE",EDGE,{"derivedFrom":[subQ8,makeQuery(id+"F7.opExtrude","CAP_EDGE",EDGE,{"disambiguationData":[OSD([subQ7,subQ6,subQ5,subQ4,subQ3,subQ2,subQ1,subQ0]),TDD([makeQuery(id+"F6.imprint","IMPRINT",EDGE,{"disambiguationData":[TD([[makeQuery(id+"F6.imprint","INTERSECT",VERTEX,{"derivedFrom":[subQ8,sQuery(id+"F6.wireOp",EDGE,"E9.15.0")]}),-1.0]])],"derivedFrom":subQ8})])],"isStart":true})]});}
            var Q9;
            {var subQ0=sQuery(id+"F3.wireOp",EDGE,"E6.right");var subQ1=sQuery(id+"F3.wireOp",EDGE,"E6.top");var subQ2=sQuery(id+"F3.wireOp",EDGE,"E6.bottom");var subQ3=sQuery(id+"F3.wireOp",EDGE,"E5.right");var subQ4=sQuery(id+"F3.wireOp",EDGE,"E5.top");var subQ5=sQuery(id+"F3.wireOp",EDGE,"E5.bottom");var subQ6=sQuery(id+"F3.wireOp",EDGE,"E4");var subQ7=sQuery(id+"F3.wireOp",EDGE,"E3");var subQ8=makeQuery(id+"F5.opFillet","BLEND_EDGE",EDGE,{"blendedFrom":[makeQuery(id+"F4.opExtrude","CAP_EDGE",EDGE,{"disambiguationData":[OSD([subQ6])],"isStart":false}),makeQuery(id+"F4.opExtrude","CAP_FACE",FACE,{"disambiguationData":[OSD([subQ7,subQ6,subQ5,subQ4,subQ3,subQ2,subQ1,subQ0])],"isStart":false})],"blendedInto":[makeQuery(id+"F4.opExtrude","CAP_FACE",FACE,{"disambiguationData":[OSD([subQ7,subQ6,subQ5,subQ4,subQ3,subQ2,subQ1,subQ0])],"isStart":false})]});Q9=makeQuery(id+"F7.boolean.opBoolean","MERGE",EDGE,{"derivedFrom":[subQ8,makeQuery(id+"F7.opExtrude","CAP_EDGE",EDGE,{"disambiguationData":[OSD([subQ7,subQ6,subQ5,subQ4,subQ3,subQ2,subQ1,subQ0]),TDD([makeQuery(id+"F6.imprint","IMPRINT",EDGE,{"disambiguationData":[TD([[makeQuery(id+"F6.imprint","INTERSECT",VERTEX,{"derivedFrom":[subQ8,sQuery(id+"F6.wireOp",EDGE,"E9.17.0")]}),-1.0]])],"derivedFrom":subQ8})])],"isStart":true})]});}
            var Q10;
            {var subQ0=sQuery(id+"F3.wireOp",EDGE,"E6.right");var subQ1=sQuery(id+"F3.wireOp",EDGE,"E6.top");var subQ2=sQuery(id+"F3.wireOp",EDGE,"E6.bottom");var subQ3=sQuery(id+"F3.wireOp",EDGE,"E5.right");var subQ4=sQuery(id+"F3.wireOp",EDGE,"E5.top");var subQ5=sQuery(id+"F3.wireOp",EDGE,"E5.bottom");var subQ6=sQuery(id+"F3.wireOp",EDGE,"E4");var subQ7=sQuery(id+"F3.wireOp",EDGE,"E3");var subQ8=makeQuery(id+"F5.opFillet","BLEND_EDGE",EDGE,{"blendedFrom":[makeQuery(id+"F4.opExtrude","CAP_EDGE",EDGE,{"disambiguationData":[OSD([subQ6])],"isStart":false}),makeQuery(id+"F4.opExtrude","CAP_FACE",FACE,{"disambiguationData":[OSD([subQ7,subQ6,subQ5,subQ4,subQ3,subQ2,subQ1,subQ0])],"isStart":false})],"blendedInto":[makeQuery(id+"F4.opExtrude","CAP_FACE",FACE,{"disambiguationData":[OSD([subQ7,subQ6,subQ5,subQ4,subQ3,subQ2,subQ1,subQ0])],"isStart":false})]});Q10=makeQuery(id+"F7.boolean.opBoolean","MERGE",EDGE,{"derivedFrom":[subQ8,makeQuery(id+"F7.opExtrude","CAP_EDGE",EDGE,{"disambiguationData":[OSD([subQ7,subQ6,subQ5,subQ4,subQ3,subQ2,subQ1,subQ0]),TDD([makeQuery(id+"F6.imprint","IMPRINT",EDGE,{"disambiguationData":[TD([[makeQuery(id+"F6.imprint","INTERSECT",VERTEX,{"derivedFrom":[subQ8,sQuery(id+"F6.wireOp",EDGE,"E9.19.0")]}),-1.0]])],"derivedFrom":subQ8})])],"isStart":true})]});}
            var Q11;
            {var subQ0=sQuery(id+"F3.wireOp",EDGE,"E6.right");var subQ1=sQuery(id+"F3.wireOp",EDGE,"E6.top");var subQ2=sQuery(id+"F3.wireOp",EDGE,"E6.bottom");var subQ3=sQuery(id+"F3.wireOp",EDGE,"E5.right");var subQ4=sQuery(id+"F3.wireOp",EDGE,"E5.top");var subQ5=sQuery(id+"F3.wireOp",EDGE,"E5.bottom");var subQ6=sQuery(id+"F3.wireOp",EDGE,"E4");var subQ7=sQuery(id+"F3.wireOp",EDGE,"E3");var subQ8=makeQuery(id+"F5.opFillet","BLEND_EDGE",EDGE,{"blendedFrom":[makeQuery(id+"F4.opExtrude","CAP_EDGE",EDGE,{"disambiguationData":[OSD([subQ6])],"isStart":false}),makeQuery(id+"F4.opExtrude","CAP_FACE",FACE,{"disambiguationData":[OSD([subQ7,subQ6,subQ5,subQ4,subQ3,subQ2,subQ1,subQ0])],"isStart":false})],"blendedInto":[makeQuery(id+"F4.opExtrude","CAP_FACE",FACE,{"disambiguationData":[OSD([subQ7,subQ6,subQ5,subQ4,subQ3,subQ2,subQ1,subQ0])],"isStart":false})]});Q11=makeQuery(id+"F7.boolean.opBoolean","MERGE",EDGE,{"derivedFrom":[subQ8,makeQuery(id+"F7.opExtrude","CAP_EDGE",EDGE,{"disambiguationData":[OSD([subQ7,subQ6,subQ5,subQ4,subQ3,subQ2,subQ1,subQ0]),TDD([makeQuery(id+"F6.imprint","IMPRINT",EDGE,{"disambiguationData":[TD([[makeQuery(id+"F6.imprint","INTERSECT",VERTEX,{"derivedFrom":[subQ8,sQuery(id+"F6.wireOp",EDGE,"E9.21.0")]}),-1.0]])],"derivedFrom":subQ8})])],"isStart":true})]});}
            var Q12;
            {var subQ0=sQuery(id+"F3.wireOp",EDGE,"E6.right");var subQ1=sQuery(id+"F3.wireOp",EDGE,"E6.top");var subQ2=sQuery(id+"F3.wireOp",EDGE,"E6.bottom");var subQ3=sQuery(id+"F3.wireOp",EDGE,"E5.right");var subQ4=sQuery(id+"F3.wireOp",EDGE,"E5.top");var subQ5=sQuery(id+"F3.wireOp",EDGE,"E5.bottom");var subQ6=sQuery(id+"F3.wireOp",EDGE,"E4");var subQ7=sQuery(id+"F3.wireOp",EDGE,"E3");var subQ8=makeQuery(id+"F5.opFillet","BLEND_EDGE",EDGE,{"blendedFrom":[makeQuery(id+"F4.opExtrude","CAP_EDGE",EDGE,{"disambiguationData":[OSD([subQ6])],"isStart":false}),makeQuery(id+"F4.opExtrude","CAP_FACE",FACE,{"disambiguationData":[OSD([subQ7,subQ6,subQ5,subQ4,subQ3,subQ2,subQ1,subQ0])],"isStart":false})],"blendedInto":[makeQuery(id+"F4.opExtrude","CAP_FACE",FACE,{"disambiguationData":[OSD([subQ7,subQ6,subQ5,subQ4,subQ3,subQ2,subQ1,subQ0])],"isStart":false})]});Q12=makeQuery(id+"F7.boolean.opBoolean","MERGE",EDGE,{"derivedFrom":[subQ8,makeQuery(id+"F7.opExtrude","CAP_EDGE",EDGE,{"disambiguationData":[OSD([subQ7,subQ6,subQ5,subQ4,subQ3,subQ2,subQ1,subQ0]),TDD([makeQuery(id+"F6.imprint","IMPRINT",EDGE,{"disambiguationData":[TD([[makeQuery(id+"F6.imprint","INTERSECT",VERTEX,{"derivedFrom":[subQ8,sQuery(id+"F6.wireOp",EDGE,"E9.23.0")]}),-1.0]])],"derivedFrom":subQ8})])],"isStart":true})]});}
            var Q13;
            {var subQ0=sQuery(id+"F3.wireOp",EDGE,"E6.right");var subQ1=sQuery(id+"F3.wireOp",EDGE,"E6.top");var subQ2=sQuery(id+"F3.wireOp",EDGE,"E6.bottom");var subQ3=sQuery(id+"F3.wireOp",EDGE,"E5.right");var subQ4=sQuery(id+"F3.wireOp",EDGE,"E5.top");var subQ5=sQuery(id+"F3.wireOp",EDGE,"E5.bottom");var subQ6=sQuery(id+"F3.wireOp",EDGE,"E4");var subQ7=sQuery(id+"F3.wireOp",EDGE,"E3");var subQ8=makeQuery(id+"F5.opFillet","BLEND_EDGE",EDGE,{"blendedFrom":[makeQuery(id+"F4.opExtrude","CAP_EDGE",EDGE,{"disambiguationData":[OSD([subQ6])],"isStart":false}),makeQuery(id+"F4.opExtrude","CAP_FACE",FACE,{"disambiguationData":[OSD([subQ7,subQ6,subQ5,subQ4,subQ3,subQ2,subQ1,subQ0])],"isStart":false})],"blendedInto":[makeQuery(id+"F4.opExtrude","CAP_FACE",FACE,{"disambiguationData":[OSD([subQ7,subQ6,subQ5,subQ4,subQ3,subQ2,subQ1,subQ0])],"isStart":false})]});Q13=makeQuery(id+"F7.boolean.opBoolean","MERGE",EDGE,{"derivedFrom":[subQ8,makeQuery(id+"F7.opExtrude","CAP_EDGE",EDGE,{"disambiguationData":[OSD([subQ7,subQ6,subQ5,subQ4,subQ3,subQ2,subQ1,subQ0]),TDD([makeQuery(id+"F6.imprint","IMPRINT",EDGE,{"disambiguationData":[TD([[makeQuery(id+"F6.imprint","INTERSECT",VERTEX,{"derivedFrom":[subQ8,sQuery(id+"F6.wireOp",EDGE,"E9.25.0")]}),-1.0]])],"derivedFrom":subQ8})])],"isStart":true})]});}
            var Q14;
            {var subQ0=sQuery(id+"F3.wireOp",EDGE,"E6.right");var subQ1=sQuery(id+"F3.wireOp",EDGE,"E6.top");var subQ2=sQuery(id+"F3.wireOp",EDGE,"E6.bottom");var subQ3=sQuery(id+"F3.wireOp",EDGE,"E5.right");var subQ4=sQuery(id+"F3.wireOp",EDGE,"E5.top");var subQ5=sQuery(id+"F3.wireOp",EDGE,"E5.bottom");var subQ6=sQuery(id+"F3.wireOp",EDGE,"E4");var subQ7=sQuery(id+"F3.wireOp",EDGE,"E3");var subQ8=makeQuery(id+"F5.opFillet","BLEND_EDGE",EDGE,{"blendedFrom":[makeQuery(id+"F4.opExtrude","CAP_EDGE",EDGE,{"disambiguationData":[OSD([subQ6])],"isStart":false}),makeQuery(id+"F4.opExtrude","CAP_FACE",FACE,{"disambiguationData":[OSD([subQ7,subQ6,subQ5,subQ4,subQ3,subQ2,subQ1,subQ0])],"isStart":false})],"blendedInto":[makeQuery(id+"F4.opExtrude","CAP_FACE",FACE,{"disambiguationData":[OSD([subQ7,subQ6,subQ5,subQ4,subQ3,subQ2,subQ1,subQ0])],"isStart":false})]});Q14=makeQuery(id+"F7.boolean.opBoolean","MERGE",EDGE,{"derivedFrom":[subQ8,makeQuery(id+"F7.opExtrude","CAP_EDGE",EDGE,{"disambiguationData":[OSD([subQ7,subQ6,subQ5,subQ4,subQ3,subQ2,subQ1,subQ0]),TDD([makeQuery(id+"F6.imprint","IMPRINT",EDGE,{"disambiguationData":[TD([[makeQuery(id+"F6.imprint","INTERSECT",VERTEX,{"derivedFrom":[subQ8,sQuery(id+"F6.wireOp",EDGE,"E9.27.0")]}),-1.0]])],"derivedFrom":subQ8})])],"isStart":true})]});}
            var Q15;
            {var subQ0=sQuery(id+"F3.wireOp",EDGE,"E6.right");var subQ1=sQuery(id+"F3.wireOp",EDGE,"E6.top");var subQ2=sQuery(id+"F3.wireOp",EDGE,"E6.bottom");var subQ3=sQuery(id+"F3.wireOp",EDGE,"E5.right");var subQ4=sQuery(id+"F3.wireOp",EDGE,"E5.top");var subQ5=sQuery(id+"F3.wireOp",EDGE,"E5.bottom");var subQ6=sQuery(id+"F3.wireOp",EDGE,"E4");var subQ7=sQuery(id+"F3.wireOp",EDGE,"E3");var subQ8=makeQuery(id+"F5.opFillet","BLEND_EDGE",EDGE,{"blendedFrom":[makeQuery(id+"F4.opExtrude","CAP_EDGE",EDGE,{"disambiguationData":[OSD([subQ6])],"isStart":false}),makeQuery(id+"F4.opExtrude","CAP_FACE",FACE,{"disambiguationData":[OSD([subQ7,subQ6,subQ5,subQ4,subQ3,subQ2,subQ1,subQ0])],"isStart":false})],"blendedInto":[makeQuery(id+"F4.opExtrude","CAP_FACE",FACE,{"disambiguationData":[OSD([subQ7,subQ6,subQ5,subQ4,subQ3,subQ2,subQ1,subQ0])],"isStart":false})]});Q15=makeQuery(id+"F7.boolean.opBoolean","MERGE",EDGE,{"derivedFrom":[subQ8,makeQuery(id+"F7.opExtrude","CAP_EDGE",EDGE,{"disambiguationData":[OSD([subQ7,subQ6,subQ5,subQ4,subQ3,subQ2,subQ1,subQ0]),TDD([makeQuery(id+"F6.imprint","IMPRINT",EDGE,{"disambiguationData":[TD([[makeQuery(id+"F6.imprint","INTERSECT",VERTEX,{"derivedFrom":[subQ8,sQuery(id+"F6.wireOp",EDGE,"E9.29.0")]}),-1.0]])],"derivedFrom":subQ8})])],"isStart":true})]});}
            var Q16;
            {var subQ0=sQuery(id+"F3.wireOp",EDGE,"E6.right");var subQ1=sQuery(id+"F3.wireOp",EDGE,"E6.top");var subQ2=sQuery(id+"F3.wireOp",EDGE,"E6.bottom");var subQ3=sQuery(id+"F3.wireOp",EDGE,"E5.right");var subQ4=sQuery(id+"F3.wireOp",EDGE,"E5.top");var subQ5=sQuery(id+"F3.wireOp",EDGE,"E5.bottom");var subQ6=sQuery(id+"F3.wireOp",EDGE,"E4");var subQ7=sQuery(id+"F3.wireOp",EDGE,"E3");var subQ8=makeQuery(id+"F5.opFillet","BLEND_EDGE",EDGE,{"blendedFrom":[makeQuery(id+"F4.opExtrude","CAP_EDGE",EDGE,{"disambiguationData":[OSD([subQ6])],"isStart":false}),makeQuery(id+"F4.opExtrude","CAP_FACE",FACE,{"disambiguationData":[OSD([subQ7,subQ6,subQ5,subQ4,subQ3,subQ2,subQ1,subQ0])],"isStart":false})],"blendedInto":[makeQuery(id+"F4.opExtrude","CAP_FACE",FACE,{"disambiguationData":[OSD([subQ7,subQ6,subQ5,subQ4,subQ3,subQ2,subQ1,subQ0])],"isStart":false})]});Q16=makeQuery(id+"F7.boolean.opBoolean","MERGE",EDGE,{"derivedFrom":[subQ8,makeQuery(id+"F7.opExtrude","CAP_EDGE",EDGE,{"disambiguationData":[OSD([subQ7,subQ6,subQ5,subQ4,subQ3,subQ2,subQ1,subQ0]),TDD([makeQuery(id+"F6.imprint","IMPRINT",EDGE,{"disambiguationData":[TD([[makeQuery(id+"F6.imprint","INTERSECT",VERTEX,{"derivedFrom":[subQ8,sQuery(id+"F6.wireOp",EDGE,"E9.31.0")]}),-1.0]])],"derivedFrom":subQ8})])],"isStart":true})]});}
            var Q17;
            {var subQ0=sQuery(id+"F3.wireOp",EDGE,"E6.right");var subQ1=sQuery(id+"F3.wireOp",EDGE,"E6.top");var subQ2=sQuery(id+"F3.wireOp",EDGE,"E6.bottom");var subQ3=sQuery(id+"F3.wireOp",EDGE,"E5.right");var subQ4=sQuery(id+"F3.wireOp",EDGE,"E5.top");var subQ5=sQuery(id+"F3.wireOp",EDGE,"E5.bottom");var subQ6=sQuery(id+"F3.wireOp",EDGE,"E4");var subQ7=sQuery(id+"F3.wireOp",EDGE,"E3");var subQ8=makeQuery(id+"F5.opFillet","BLEND_EDGE",EDGE,{"blendedFrom":[makeQuery(id+"F4.opExtrude","CAP_EDGE",EDGE,{"disambiguationData":[OSD([subQ6])],"isStart":false}),makeQuery(id+"F4.opExtrude","CAP_FACE",FACE,{"disambiguationData":[OSD([subQ7,subQ6,subQ5,subQ4,subQ3,subQ2,subQ1,subQ0])],"isStart":false})],"blendedInto":[makeQuery(id+"F4.opExtrude","CAP_FACE",FACE,{"disambiguationData":[OSD([subQ7,subQ6,subQ5,subQ4,subQ3,subQ2,subQ1,subQ0])],"isStart":false})]});Q17=makeQuery(id+"F7.boolean.opBoolean","MERGE",EDGE,{"derivedFrom":[subQ8,makeQuery(id+"F7.opExtrude","CAP_EDGE",EDGE,{"disambiguationData":[OSD([subQ7,subQ6,subQ5,subQ4,subQ3,subQ2,subQ1,subQ0]),TDD([makeQuery(id+"F6.imprint","IMPRINT",EDGE,{"disambiguationData":[TD([[makeQuery(id+"F6.imprint","INTERSECT",VERTEX,{"derivedFrom":[subQ8,sQuery(id+"F6.wireOp",EDGE,"E9.33.0")]}),-1.0]])],"derivedFrom":subQ8})])],"isStart":true})]});}
            var Q18;
            {var subQ0=sQuery(id+"F3.wireOp",EDGE,"E6.right");var subQ1=sQuery(id+"F3.wireOp",EDGE,"E6.top");var subQ2=sQuery(id+"F3.wireOp",EDGE,"E6.bottom");var subQ3=sQuery(id+"F3.wireOp",EDGE,"E5.right");var subQ4=sQuery(id+"F3.wireOp",EDGE,"E5.top");var subQ5=sQuery(id+"F3.wireOp",EDGE,"E5.bottom");var subQ6=sQuery(id+"F3.wireOp",EDGE,"E4");var subQ7=sQuery(id+"F3.wireOp",EDGE,"E3");var subQ8=makeQuery(id+"F5.opFillet","BLEND_EDGE",EDGE,{"blendedFrom":[makeQuery(id+"F4.opExtrude","CAP_EDGE",EDGE,{"disambiguationData":[OSD([subQ6])],"isStart":false}),makeQuery(id+"F4.opExtrude","CAP_FACE",FACE,{"disambiguationData":[OSD([subQ7,subQ6,subQ5,subQ4,subQ3,subQ2,subQ1,subQ0])],"isStart":false})],"blendedInto":[makeQuery(id+"F4.opExtrude","CAP_FACE",FACE,{"disambiguationData":[OSD([subQ7,subQ6,subQ5,subQ4,subQ3,subQ2,subQ1,subQ0])],"isStart":false})]});Q18=makeQuery(id+"F7.boolean.opBoolean","MERGE",EDGE,{"derivedFrom":[subQ8,makeQuery(id+"F7.opExtrude","CAP_EDGE",EDGE,{"disambiguationData":[OSD([subQ7,subQ6,subQ5,subQ4,subQ3,subQ2,subQ1,subQ0]),TDD([makeQuery(id+"F6.imprint","IMPRINT",EDGE,{"disambiguationData":[TD([[makeQuery(id+"F6.imprint","INTERSECT",VERTEX,{"derivedFrom":[subQ8,sQuery(id+"F6.wireOp",EDGE,"E9.35.0")]}),-1.0]])],"derivedFrom":subQ8})])],"isStart":true})]});}
            var Q19;
            {var subQ0=sQuery(id+"F3.wireOp",EDGE,"E6.right");var subQ1=sQuery(id+"F3.wireOp",EDGE,"E6.top");var subQ2=sQuery(id+"F3.wireOp",EDGE,"E6.bottom");var subQ3=sQuery(id+"F3.wireOp",EDGE,"E5.right");var subQ4=sQuery(id+"F3.wireOp",EDGE,"E5.top");var subQ5=sQuery(id+"F3.wireOp",EDGE,"E5.bottom");var subQ6=sQuery(id+"F3.wireOp",EDGE,"E4");var subQ7=sQuery(id+"F3.wireOp",EDGE,"E3");var subQ8=makeQuery(id+"F5.opFillet","BLEND_EDGE",EDGE,{"blendedFrom":[makeQuery(id+"F4.opExtrude","CAP_EDGE",EDGE,{"disambiguationData":[OSD([subQ6])],"isStart":false}),makeQuery(id+"F4.opExtrude","CAP_FACE",FACE,{"disambiguationData":[OSD([subQ7,subQ6,subQ5,subQ4,subQ3,subQ2,subQ1,subQ0])],"isStart":false})],"blendedInto":[makeQuery(id+"F4.opExtrude","CAP_FACE",FACE,{"disambiguationData":[OSD([subQ7,subQ6,subQ5,subQ4,subQ3,subQ2,subQ1,subQ0])],"isStart":false})]});Q19=makeQuery(id+"F7.boolean.opBoolean","MERGE",EDGE,{"derivedFrom":[subQ8,makeQuery(id+"F7.opExtrude","CAP_EDGE",EDGE,{"disambiguationData":[OSD([subQ7,subQ6,subQ5,subQ4,subQ3,subQ2,subQ1,subQ0]),TDD([makeQuery(id+"F6.imprint","IMPRINT",EDGE,{"disambiguationData":[TD([[makeQuery(id+"F6.imprint","INTERSECT",VERTEX,{"derivedFrom":[subQ8,sQuery(id+"F6.wireOp",EDGE,"E9.37.0")]}),-1.0]])],"derivedFrom":subQ8})])],"isStart":true})]});}
            var Q20;
            {var subQ0=sQuery(id+"F3.wireOp",EDGE,"E6.right");var subQ1=sQuery(id+"F3.wireOp",EDGE,"E6.top");var subQ2=sQuery(id+"F3.wireOp",EDGE,"E6.bottom");var subQ3=sQuery(id+"F3.wireOp",EDGE,"E5.right");var subQ4=sQuery(id+"F3.wireOp",EDGE,"E5.top");var subQ5=sQuery(id+"F3.wireOp",EDGE,"E5.bottom");var subQ6=sQuery(id+"F3.wireOp",EDGE,"E4");var subQ7=sQuery(id+"F3.wireOp",EDGE,"E3");var subQ8=makeQuery(id+"F5.opFillet","BLEND_EDGE",EDGE,{"blendedFrom":[makeQuery(id+"F4.opExtrude","CAP_EDGE",EDGE,{"disambiguationData":[OSD([subQ6])],"isStart":false}),makeQuery(id+"F4.opExtrude","CAP_FACE",FACE,{"disambiguationData":[OSD([subQ7,subQ6,subQ5,subQ4,subQ3,subQ2,subQ1,subQ0])],"isStart":false})],"blendedInto":[makeQuery(id+"F4.opExtrude","CAP_FACE",FACE,{"disambiguationData":[OSD([subQ7,subQ6,subQ5,subQ4,subQ3,subQ2,subQ1,subQ0])],"isStart":false})]});Q20=makeQuery(id+"F7.boolean.opBoolean","MERGE",EDGE,{"derivedFrom":[subQ8,makeQuery(id+"F7.opExtrude","CAP_EDGE",EDGE,{"disambiguationData":[OSD([subQ7,subQ6,subQ5,subQ4,subQ3,subQ2,subQ1,subQ0]),TDD([makeQuery(id+"F6.imprint","IMPRINT",EDGE,{"disambiguationData":[TD([[makeQuery(id+"F6.imprint","INTERSECT",VERTEX,{"derivedFrom":[subQ8,sQuery(id+"F6.wireOp",EDGE,"E9.39.0")]}),-1.0]])],"derivedFrom":subQ8})])],"isStart":true})]});}
            var Q21;
            {var subQ0=sQuery(id+"F3.wireOp",EDGE,"E6.right");var subQ1=sQuery(id+"F3.wireOp",EDGE,"E6.top");var subQ2=sQuery(id+"F3.wireOp",EDGE,"E6.bottom");var subQ3=sQuery(id+"F3.wireOp",EDGE,"E5.right");var subQ4=sQuery(id+"F3.wireOp",EDGE,"E5.top");var subQ5=sQuery(id+"F3.wireOp",EDGE,"E5.bottom");var subQ6=sQuery(id+"F3.wireOp",EDGE,"E4");var subQ7=sQuery(id+"F3.wireOp",EDGE,"E3");var subQ8=makeQuery(id+"F5.opFillet","BLEND_EDGE",EDGE,{"blendedFrom":[makeQuery(id+"F4.opExtrude","CAP_EDGE",EDGE,{"disambiguationData":[OSD([subQ6])],"isStart":false}),makeQuery(id+"F4.opExtrude","CAP_FACE",FACE,{"disambiguationData":[OSD([subQ7,subQ6,subQ5,subQ4,subQ3,subQ2,subQ1,subQ0])],"isStart":false})],"blendedInto":[makeQuery(id+"F4.opExtrude","CAP_FACE",FACE,{"disambiguationData":[OSD([subQ7,subQ6,subQ5,subQ4,subQ3,subQ2,subQ1,subQ0])],"isStart":false})]});Q21=makeQuery(id+"F7.boolean.opBoolean","MERGE",EDGE,{"derivedFrom":[subQ8,makeQuery(id+"F7.opExtrude","CAP_EDGE",EDGE,{"disambiguationData":[OSD([subQ7,subQ6,subQ5,subQ4,subQ3,subQ2,subQ1,subQ0]),TDD([makeQuery(id+"F6.imprint","IMPRINT",EDGE,{"disambiguationData":[TD([[makeQuery(id+"F6.imprint","INTERSECT",VERTEX,{"derivedFrom":[subQ8,sQuery(id+"F6.wireOp",EDGE,"E9.41.0")]}),-1.0]])],"derivedFrom":subQ8})])],"isStart":true})]});}
            var Q22;
            {var subQ0=sQuery(id+"F3.wireOp",EDGE,"E6.right");var subQ1=sQuery(id+"F3.wireOp",EDGE,"E6.top");var subQ2=sQuery(id+"F3.wireOp",EDGE,"E6.bottom");var subQ3=sQuery(id+"F3.wireOp",EDGE,"E5.right");var subQ4=sQuery(id+"F3.wireOp",EDGE,"E5.top");var subQ5=sQuery(id+"F3.wireOp",EDGE,"E5.bottom");var subQ6=sQuery(id+"F3.wireOp",EDGE,"E4");var subQ7=sQuery(id+"F3.wireOp",EDGE,"E3");var subQ8=makeQuery(id+"F5.opFillet","BLEND_EDGE",EDGE,{"blendedFrom":[makeQuery(id+"F4.opExtrude","CAP_EDGE",EDGE,{"disambiguationData":[OSD([subQ6])],"isStart":false}),makeQuery(id+"F4.opExtrude","CAP_FACE",FACE,{"disambiguationData":[OSD([subQ7,subQ6,subQ5,subQ4,subQ3,subQ2,subQ1,subQ0])],"isStart":false})],"blendedInto":[makeQuery(id+"F4.opExtrude","CAP_FACE",FACE,{"disambiguationData":[OSD([subQ7,subQ6,subQ5,subQ4,subQ3,subQ2,subQ1,subQ0])],"isStart":false})]});Q22=makeQuery(id+"F7.boolean.opBoolean","MERGE",EDGE,{"derivedFrom":[subQ8,makeQuery(id+"F7.opExtrude","CAP_EDGE",EDGE,{"disambiguationData":[OSD([subQ7,subQ6,subQ5,subQ4,subQ3,subQ2,subQ1,subQ0]),TDD([makeQuery(id+"F6.imprint","IMPRINT",EDGE,{"disambiguationData":[TD([[makeQuery(id+"F6.imprint","INTERSECT",VERTEX,{"derivedFrom":[subQ8,sQuery(id+"F6.wireOp",EDGE,"E9.43.0")]}),-1.0]])],"derivedFrom":subQ8})])],"isStart":true})]});}
            var Q23;
            {var subQ0=sQuery(id+"F3.wireOp",EDGE,"E6.right");var subQ1=sQuery(id+"F3.wireOp",EDGE,"E6.top");var subQ2=sQuery(id+"F3.wireOp",EDGE,"E6.bottom");var subQ3=sQuery(id+"F3.wireOp",EDGE,"E5.right");var subQ4=sQuery(id+"F3.wireOp",EDGE,"E5.top");var subQ5=sQuery(id+"F3.wireOp",EDGE,"E5.bottom");var subQ6=sQuery(id+"F3.wireOp",EDGE,"E4");var subQ7=sQuery(id+"F3.wireOp",EDGE,"E3");var subQ8=makeQuery(id+"F5.opFillet","BLEND_EDGE",EDGE,{"blendedFrom":[makeQuery(id+"F4.opExtrude","CAP_EDGE",EDGE,{"disambiguationData":[OSD([subQ6])],"isStart":false}),makeQuery(id+"F4.opExtrude","CAP_FACE",FACE,{"disambiguationData":[OSD([subQ7,subQ6,subQ5,subQ4,subQ3,subQ2,subQ1,subQ0])],"isStart":false})],"blendedInto":[makeQuery(id+"F4.opExtrude","CAP_FACE",FACE,{"disambiguationData":[OSD([subQ7,subQ6,subQ5,subQ4,subQ3,subQ2,subQ1,subQ0])],"isStart":false})]});Q23=makeQuery(id+"F7.boolean.opBoolean","MERGE",EDGE,{"derivedFrom":[subQ8,makeQuery(id+"F7.opExtrude","CAP_EDGE",EDGE,{"disambiguationData":[OSD([subQ7,subQ6,subQ5,subQ4,subQ3,subQ2,subQ1,subQ0]),TDD([makeQuery(id+"F6.imprint","IMPRINT",EDGE,{"disambiguationData":[TD([[makeQuery(id+"F6.imprint","INTERSECT",VERTEX,{"derivedFrom":[subQ8,sQuery(id+"F6.wireOp",EDGE,"E9.45.0")]}),-1.0]])],"derivedFrom":subQ8})])],"isStart":true})]});}
            var Q24;
            {var subQ0=sQuery(id+"F3.wireOp",EDGE,"E6.right");var subQ1=sQuery(id+"F3.wireOp",EDGE,"E6.top");var subQ2=sQuery(id+"F3.wireOp",EDGE,"E6.bottom");var subQ3=sQuery(id+"F3.wireOp",EDGE,"E5.right");var subQ4=sQuery(id+"F3.wireOp",EDGE,"E5.top");var subQ5=sQuery(id+"F3.wireOp",EDGE,"E5.bottom");var subQ6=sQuery(id+"F3.wireOp",EDGE,"E4");var subQ7=sQuery(id+"F3.wireOp",EDGE,"E3");var subQ8=makeQuery(id+"F5.opFillet","BLEND_EDGE",EDGE,{"blendedFrom":[makeQuery(id+"F4.opExtrude","CAP_EDGE",EDGE,{"disambiguationData":[OSD([subQ6])],"isStart":false}),makeQuery(id+"F4.opExtrude","CAP_FACE",FACE,{"disambiguationData":[OSD([subQ7,subQ6,subQ5,subQ4,subQ3,subQ2,subQ1,subQ0])],"isStart":false})],"blendedInto":[makeQuery(id+"F4.opExtrude","CAP_FACE",FACE,{"disambiguationData":[OSD([subQ7,subQ6,subQ5,subQ4,subQ3,subQ2,subQ1,subQ0])],"isStart":false})]});Q24=makeQuery(id+"F7.boolean.opBoolean","MERGE",EDGE,{"derivedFrom":[subQ8,makeQuery(id+"F7.opExtrude","CAP_EDGE",EDGE,{"disambiguationData":[OSD([subQ7,subQ6,subQ5,subQ4,subQ3,subQ2,subQ1,subQ0]),TDD([makeQuery(id+"F6.imprint","IMPRINT",EDGE,{"disambiguationData":[TD([[makeQuery(id+"F6.imprint","INTERSECT",VERTEX,{"derivedFrom":[subQ8,sQuery(id+"F6.wireOp",EDGE,"E9.47.0")]}),-1.0]])],"derivedFrom":subQ8})])],"isStart":true})]});}
            var Q25;
            {var subQ0=sQuery(id+"F3.wireOp",EDGE,"E6.right");var subQ1=sQuery(id+"F3.wireOp",EDGE,"E6.top");var subQ2=sQuery(id+"F3.wireOp",EDGE,"E6.bottom");var subQ3=sQuery(id+"F3.wireOp",EDGE,"E5.right");var subQ4=sQuery(id+"F3.wireOp",EDGE,"E5.top");var subQ5=sQuery(id+"F3.wireOp",EDGE,"E5.bottom");var subQ6=sQuery(id+"F3.wireOp",EDGE,"E4");var subQ7=sQuery(id+"F3.wireOp",EDGE,"E3");var subQ8=makeQuery(id+"F5.opFillet","BLEND_EDGE",EDGE,{"blendedFrom":[makeQuery(id+"F4.opExtrude","CAP_EDGE",EDGE,{"disambiguationData":[OSD([subQ6])],"isStart":false}),makeQuery(id+"F4.opExtrude","CAP_FACE",FACE,{"disambiguationData":[OSD([subQ7,subQ6,subQ5,subQ4,subQ3,subQ2,subQ1,subQ0])],"isStart":false})],"blendedInto":[makeQuery(id+"F4.opExtrude","CAP_FACE",FACE,{"disambiguationData":[OSD([subQ7,subQ6,subQ5,subQ4,subQ3,subQ2,subQ1,subQ0])],"isStart":false})]});Q25=makeQuery(id+"F7.boolean.opBoolean","MERGE",EDGE,{"derivedFrom":[subQ8,makeQuery(id+"F7.opExtrude","CAP_EDGE",EDGE,{"disambiguationData":[OSD([subQ7,subQ6,subQ5,subQ4,subQ3,subQ2,subQ1,subQ0]),TDD([makeQuery(id+"F6.imprint","IMPRINT",EDGE,{"disambiguationData":[TD([[makeQuery(id+"F6.imprint","INTERSECT",VERTEX,{"derivedFrom":[subQ8,sQuery(id+"F6.wireOp",EDGE,"E9.49.0")]}),-1.0]])],"derivedFrom":subQ8})])],"isStart":true})]});}
            var Q26;
            {var subQ0=sQuery(id+"F3.wireOp",EDGE,"E6.right");var subQ1=sQuery(id+"F3.wireOp",EDGE,"E6.top");var subQ2=sQuery(id+"F3.wireOp",EDGE,"E6.bottom");var subQ3=sQuery(id+"F3.wireOp",EDGE,"E5.right");var subQ4=sQuery(id+"F3.wireOp",EDGE,"E5.top");var subQ5=sQuery(id+"F3.wireOp",EDGE,"E5.bottom");var subQ6=sQuery(id+"F3.wireOp",EDGE,"E4");var subQ7=sQuery(id+"F3.wireOp",EDGE,"E3");var subQ8=makeQuery(id+"F5.opFillet","BLEND_EDGE",EDGE,{"blendedFrom":[makeQuery(id+"F4.opExtrude","CAP_EDGE",EDGE,{"disambiguationData":[OSD([subQ6])],"isStart":false}),makeQuery(id+"F4.opExtrude","CAP_FACE",FACE,{"disambiguationData":[OSD([subQ7,subQ6,subQ5,subQ4,subQ3,subQ2,subQ1,subQ0])],"isStart":false})],"blendedInto":[makeQuery(id+"F4.opExtrude","CAP_FACE",FACE,{"disambiguationData":[OSD([subQ7,subQ6,subQ5,subQ4,subQ3,subQ2,subQ1,subQ0])],"isStart":false})]});Q26=makeQuery(id+"F7.boolean.opBoolean","MERGE",EDGE,{"derivedFrom":[subQ8,makeQuery(id+"F7.opExtrude","CAP_EDGE",EDGE,{"disambiguationData":[OSD([subQ7,subQ6,subQ5,subQ4,subQ3,subQ2,subQ1,subQ0]),TDD([makeQuery(id+"F6.imprint","IMPRINT",EDGE,{"disambiguationData":[TD([[makeQuery(id+"F6.imprint","INTERSECT",VERTEX,{"derivedFrom":[subQ8,sQuery(id+"F6.wireOp",EDGE,"E9.51.0")]}),-1.0]])],"derivedFrom":subQ8})])],"isStart":true})]});}
            var Q27;
            {var subQ0=sQuery(id+"F3.wireOp",EDGE,"E6.right");var subQ1=sQuery(id+"F3.wireOp",EDGE,"E6.top");var subQ2=sQuery(id+"F3.wireOp",EDGE,"E6.bottom");var subQ3=sQuery(id+"F3.wireOp",EDGE,"E5.right");var subQ4=sQuery(id+"F3.wireOp",EDGE,"E5.top");var subQ5=sQuery(id+"F3.wireOp",EDGE,"E5.bottom");var subQ6=sQuery(id+"F3.wireOp",EDGE,"E4");var subQ7=sQuery(id+"F3.wireOp",EDGE,"E3");var subQ8=makeQuery(id+"F5.opFillet","BLEND_EDGE",EDGE,{"blendedFrom":[makeQuery(id+"F4.opExtrude","CAP_EDGE",EDGE,{"disambiguationData":[OSD([subQ6])],"isStart":false}),makeQuery(id+"F4.opExtrude","CAP_FACE",FACE,{"disambiguationData":[OSD([subQ7,subQ6,subQ5,subQ4,subQ3,subQ2,subQ1,subQ0])],"isStart":false})],"blendedInto":[makeQuery(id+"F4.opExtrude","CAP_FACE",FACE,{"disambiguationData":[OSD([subQ7,subQ6,subQ5,subQ4,subQ3,subQ2,subQ1,subQ0])],"isStart":false})]});Q27=makeQuery(id+"F7.boolean.opBoolean","MERGE",EDGE,{"derivedFrom":[subQ8,makeQuery(id+"F7.opExtrude","CAP_EDGE",EDGE,{"disambiguationData":[OSD([subQ7,subQ6,subQ5,subQ4,subQ3,subQ2,subQ1,subQ0]),TDD([makeQuery(id+"F6.imprint","IMPRINT",EDGE,{"disambiguationData":[TD([[makeQuery(id+"F6.imprint","INTERSECT",VERTEX,{"derivedFrom":[subQ8,sQuery(id+"F6.wireOp",EDGE,"E9.53.0")]}),-1.0]])],"derivedFrom":subQ8})])],"isStart":true})]});}
            var Q28;
            {var subQ0=sQuery(id+"F3.wireOp",EDGE,"E6.right");var subQ1=sQuery(id+"F3.wireOp",EDGE,"E6.top");var subQ2=sQuery(id+"F3.wireOp",EDGE,"E6.bottom");var subQ3=sQuery(id+"F3.wireOp",EDGE,"E5.right");var subQ4=sQuery(id+"F3.wireOp",EDGE,"E5.top");var subQ5=sQuery(id+"F3.wireOp",EDGE,"E5.bottom");var subQ6=sQuery(id+"F3.wireOp",EDGE,"E4");var subQ7=sQuery(id+"F3.wireOp",EDGE,"E3");var subQ8=makeQuery(id+"F5.opFillet","BLEND_EDGE",EDGE,{"blendedFrom":[makeQuery(id+"F4.opExtrude","CAP_EDGE",EDGE,{"disambiguationData":[OSD([subQ6])],"isStart":false}),makeQuery(id+"F4.opExtrude","CAP_FACE",FACE,{"disambiguationData":[OSD([subQ7,subQ6,subQ5,subQ4,subQ3,subQ2,subQ1,subQ0])],"isStart":false})],"blendedInto":[makeQuery(id+"F4.opExtrude","CAP_FACE",FACE,{"disambiguationData":[OSD([subQ7,subQ6,subQ5,subQ4,subQ3,subQ2,subQ1,subQ0])],"isStart":false})]});Q28=makeQuery(id+"F7.boolean.opBoolean","MERGE",EDGE,{"derivedFrom":[subQ8,makeQuery(id+"F7.opExtrude","CAP_EDGE",EDGE,{"disambiguationData":[OSD([subQ7,subQ6,subQ5,subQ4,subQ3,subQ2,subQ1,subQ0]),TDD([makeQuery(id+"F6.imprint","IMPRINT",EDGE,{"disambiguationData":[TD([[makeQuery(id+"F6.imprint","INTERSECT",VERTEX,{"derivedFrom":[subQ8,sQuery(id+"F6.wireOp",EDGE,"E9.55.0")]}),-1.0]])],"derivedFrom":subQ8})])],"isStart":true})]});}
            var Q29;
            {var subQ0=sQuery(id+"F3.wireOp",EDGE,"E6.right");var subQ1=sQuery(id+"F3.wireOp",EDGE,"E6.top");var subQ2=sQuery(id+"F3.wireOp",EDGE,"E6.bottom");var subQ3=sQuery(id+"F3.wireOp",EDGE,"E5.right");var subQ4=sQuery(id+"F3.wireOp",EDGE,"E5.top");var subQ5=sQuery(id+"F3.wireOp",EDGE,"E5.bottom");var subQ6=sQuery(id+"F3.wireOp",EDGE,"E4");var subQ7=sQuery(id+"F3.wireOp",EDGE,"E3");var subQ8=makeQuery(id+"F5.opFillet","BLEND_EDGE",EDGE,{"blendedFrom":[makeQuery(id+"F4.opExtrude","CAP_EDGE",EDGE,{"disambiguationData":[OSD([subQ6])],"isStart":false}),makeQuery(id+"F4.opExtrude","CAP_FACE",FACE,{"disambiguationData":[OSD([subQ7,subQ6,subQ5,subQ4,subQ3,subQ2,subQ1,subQ0])],"isStart":false})],"blendedInto":[makeQuery(id+"F4.opExtrude","CAP_FACE",FACE,{"disambiguationData":[OSD([subQ7,subQ6,subQ5,subQ4,subQ3,subQ2,subQ1,subQ0])],"isStart":false})]});Q29=makeQuery(id+"F7.boolean.opBoolean","MERGE",EDGE,{"derivedFrom":[subQ8,makeQuery(id+"F7.opExtrude","CAP_EDGE",EDGE,{"disambiguationData":[OSD([subQ7,subQ6,subQ5,subQ4,subQ3,subQ2,subQ1,subQ0]),TDD([makeQuery(id+"F6.imprint","IMPRINT",EDGE,{"disambiguationData":[TD([[makeQuery(id+"F6.imprint","INTERSECT",VERTEX,{"derivedFrom":[subQ8,sQuery(id+"F6.wireOp",EDGE,"E9.57.0")]}),-1.0]])],"derivedFrom":subQ8})])],"isStart":true})]});}
            var Q30;
            {var subQ0=sQuery(id+"F3.wireOp",EDGE,"E6.right");var subQ1=sQuery(id+"F3.wireOp",EDGE,"E6.top");var subQ2=sQuery(id+"F3.wireOp",EDGE,"E6.bottom");var subQ3=sQuery(id+"F3.wireOp",EDGE,"E5.right");var subQ4=sQuery(id+"F3.wireOp",EDGE,"E5.top");var subQ5=sQuery(id+"F3.wireOp",EDGE,"E5.bottom");var subQ6=sQuery(id+"F3.wireOp",EDGE,"E4");var subQ7=sQuery(id+"F3.wireOp",EDGE,"E3");var subQ8=makeQuery(id+"F5.opFillet","BLEND_EDGE",EDGE,{"blendedFrom":[makeQuery(id+"F4.opExtrude","CAP_EDGE",EDGE,{"disambiguationData":[OSD([subQ6])],"isStart":false}),makeQuery(id+"F4.opExtrude","CAP_FACE",FACE,{"disambiguationData":[OSD([subQ7,subQ6,subQ5,subQ4,subQ3,subQ2,subQ1,subQ0])],"isStart":false})],"blendedInto":[makeQuery(id+"F4.opExtrude","CAP_FACE",FACE,{"disambiguationData":[OSD([subQ7,subQ6,subQ5,subQ4,subQ3,subQ2,subQ1,subQ0])],"isStart":false})]});Q30=makeQuery(id+"F7.boolean.opBoolean","MERGE",EDGE,{"derivedFrom":[subQ8,makeQuery(id+"F7.opExtrude","CAP_EDGE",EDGE,{"disambiguationData":[OSD([subQ7,subQ6,subQ5,subQ4,subQ3,subQ2,subQ1,subQ0]),TDD([makeQuery(id+"F6.imprint","IMPRINT",EDGE,{"disambiguationData":[TD([[makeQuery(id+"F6.imprint","INTERSECT",VERTEX,{"derivedFrom":[subQ8,sQuery(id+"F6.wireOp",EDGE,"E9.61.0")]}),-1.0]])],"derivedFrom":subQ8})])],"isStart":true})]});}
            var Q31;
            {var subQ0=sQuery(id+"F3.wireOp",EDGE,"E6.right");var subQ1=sQuery(id+"F3.wireOp",EDGE,"E6.top");var subQ2=sQuery(id+"F3.wireOp",EDGE,"E6.bottom");var subQ3=sQuery(id+"F3.wireOp",EDGE,"E5.right");var subQ4=sQuery(id+"F3.wireOp",EDGE,"E5.top");var subQ5=sQuery(id+"F3.wireOp",EDGE,"E5.bottom");var subQ6=sQuery(id+"F3.wireOp",EDGE,"E4");var subQ7=sQuery(id+"F3.wireOp",EDGE,"E3");var subQ8=makeQuery(id+"F5.opFillet","BLEND_EDGE",EDGE,{"blendedFrom":[makeQuery(id+"F4.opExtrude","CAP_EDGE",EDGE,{"disambiguationData":[OSD([subQ6])],"isStart":false}),makeQuery(id+"F4.opExtrude","CAP_FACE",FACE,{"disambiguationData":[OSD([subQ7,subQ6,subQ5,subQ4,subQ3,subQ2,subQ1,subQ0])],"isStart":false})],"blendedInto":[makeQuery(id+"F4.opExtrude","CAP_FACE",FACE,{"disambiguationData":[OSD([subQ7,subQ6,subQ5,subQ4,subQ3,subQ2,subQ1,subQ0])],"isStart":false})]});Q31=makeQuery(id+"F7.boolean.opBoolean","MERGE",EDGE,{"derivedFrom":[subQ8,makeQuery(id+"F7.opExtrude","CAP_EDGE",EDGE,{"disambiguationData":[OSD([subQ7,subQ6,subQ5,subQ4,subQ3,subQ2,subQ1,subQ0]),TDD([makeQuery(id+"F6.imprint","IMPRINT",EDGE,{"disambiguationData":[TD([[makeQuery(id+"F6.imprint","INTERSECT",VERTEX,{"derivedFrom":[subQ8,sQuery(id+"F6.wireOp",EDGE,"E9.63.0")]}),-1.0]])],"derivedFrom":subQ8})])],"isStart":true})]});}
            var Q32;
            {var subQ0=sQuery(id+"F3.wireOp",EDGE,"E6.right");var subQ1=sQuery(id+"F3.wireOp",EDGE,"E6.top");var subQ2=sQuery(id+"F3.wireOp",EDGE,"E6.bottom");var subQ3=sQuery(id+"F3.wireOp",EDGE,"E5.right");var subQ4=sQuery(id+"F3.wireOp",EDGE,"E5.top");var subQ5=sQuery(id+"F3.wireOp",EDGE,"E5.bottom");var subQ6=sQuery(id+"F3.wireOp",EDGE,"E4");var subQ7=sQuery(id+"F3.wireOp",EDGE,"E3");var subQ8=makeQuery(id+"F5.opFillet","BLEND_EDGE",EDGE,{"blendedFrom":[makeQuery(id+"F4.opExtrude","CAP_EDGE",EDGE,{"disambiguationData":[OSD([subQ6])],"isStart":false}),makeQuery(id+"F4.opExtrude","CAP_FACE",FACE,{"disambiguationData":[OSD([subQ7,subQ6,subQ5,subQ4,subQ3,subQ2,subQ1,subQ0])],"isStart":false})],"blendedInto":[makeQuery(id+"F4.opExtrude","CAP_FACE",FACE,{"disambiguationData":[OSD([subQ7,subQ6,subQ5,subQ4,subQ3,subQ2,subQ1,subQ0])],"isStart":false})]});Q32=makeQuery(id+"F7.boolean.opBoolean","MERGE",EDGE,{"derivedFrom":[subQ8,makeQuery(id+"F7.opExtrude","CAP_EDGE",EDGE,{"disambiguationData":[OSD([subQ7,subQ6,subQ5,subQ4,subQ3,subQ2,subQ1,subQ0]),TDD([makeQuery(id+"F6.imprint","IMPRINT",EDGE,{"disambiguationData":[TD([[makeQuery(id+"F6.imprint","INTERSECT",VERTEX,{"derivedFrom":[subQ8,sQuery(id+"F6.wireOp",EDGE,"E9.65.0")]}),-1.0]])],"derivedFrom":subQ8})])],"isStart":true})]});}
            var Q33;
            {var subQ0=sQuery(id+"F3.wireOp",EDGE,"E6.right");var subQ1=sQuery(id+"F3.wireOp",EDGE,"E6.top");var subQ2=sQuery(id+"F3.wireOp",EDGE,"E6.bottom");var subQ3=sQuery(id+"F3.wireOp",EDGE,"E5.right");var subQ4=sQuery(id+"F3.wireOp",EDGE,"E5.top");var subQ5=sQuery(id+"F3.wireOp",EDGE,"E5.bottom");var subQ6=sQuery(id+"F3.wireOp",EDGE,"E4");var subQ7=sQuery(id+"F3.wireOp",EDGE,"E3");var subQ8=makeQuery(id+"F5.opFillet","BLEND_EDGE",EDGE,{"blendedFrom":[makeQuery(id+"F4.opExtrude","CAP_EDGE",EDGE,{"disambiguationData":[OSD([subQ6])],"isStart":false}),makeQuery(id+"F4.opExtrude","CAP_FACE",FACE,{"disambiguationData":[OSD([subQ7,subQ6,subQ5,subQ4,subQ3,subQ2,subQ1,subQ0])],"isStart":false})],"blendedInto":[makeQuery(id+"F4.opExtrude","CAP_FACE",FACE,{"disambiguationData":[OSD([subQ7,subQ6,subQ5,subQ4,subQ3,subQ2,subQ1,subQ0])],"isStart":false})]});Q33=makeQuery(id+"F7.boolean.opBoolean","MERGE",EDGE,{"derivedFrom":[subQ8,makeQuery(id+"F7.opExtrude","CAP_EDGE",EDGE,{"disambiguationData":[OSD([subQ7,subQ6,subQ5,subQ4,subQ3,subQ2,subQ1,subQ0]),TDD([makeQuery(id+"F6.imprint","IMPRINT",EDGE,{"disambiguationData":[TD([[makeQuery(id+"F6.imprint","INTERSECT",VERTEX,{"derivedFrom":[subQ8,sQuery(id+"F6.wireOp",EDGE,"E9.67.0")]}),-1.0]])],"derivedFrom":subQ8})])],"isStart":true})]});}
            var Q34;
            {var subQ0=sQuery(id+"F3.wireOp",EDGE,"E6.right");var subQ1=sQuery(id+"F3.wireOp",EDGE,"E6.top");var subQ2=sQuery(id+"F3.wireOp",EDGE,"E6.bottom");var subQ3=sQuery(id+"F3.wireOp",EDGE,"E5.right");var subQ4=sQuery(id+"F3.wireOp",EDGE,"E5.top");var subQ5=sQuery(id+"F3.wireOp",EDGE,"E5.bottom");var subQ6=sQuery(id+"F3.wireOp",EDGE,"E4");var subQ7=sQuery(id+"F3.wireOp",EDGE,"E3");var subQ8=makeQuery(id+"F5.opFillet","BLEND_EDGE",EDGE,{"blendedFrom":[makeQuery(id+"F4.opExtrude","CAP_EDGE",EDGE,{"disambiguationData":[OSD([subQ6])],"isStart":false}),makeQuery(id+"F4.opExtrude","CAP_FACE",FACE,{"disambiguationData":[OSD([subQ7,subQ6,subQ5,subQ4,subQ3,subQ2,subQ1,subQ0])],"isStart":false})],"blendedInto":[makeQuery(id+"F4.opExtrude","CAP_FACE",FACE,{"disambiguationData":[OSD([subQ7,subQ6,subQ5,subQ4,subQ3,subQ2,subQ1,subQ0])],"isStart":false})]});Q34=makeQuery(id+"F7.boolean.opBoolean","MERGE",EDGE,{"derivedFrom":[subQ8,makeQuery(id+"F7.opExtrude","CAP_EDGE",EDGE,{"disambiguationData":[OSD([subQ7,subQ6,subQ5,subQ4,subQ3,subQ2,subQ1,subQ0]),TDD([makeQuery(id+"F6.imprint","IMPRINT",EDGE,{"disambiguationData":[TD([[makeQuery(id+"F6.imprint","INTERSECT",VERTEX,{"derivedFrom":[subQ8,sQuery(id+"F6.wireOp",EDGE,"E9.69.0")]}),-1.0]])],"derivedFrom":subQ8})])],"isStart":true})]});}
            var Q35;
            {var subQ0=sQuery(id+"F3.wireOp",EDGE,"E6.right");var subQ1=sQuery(id+"F3.wireOp",EDGE,"E6.top");var subQ2=sQuery(id+"F3.wireOp",EDGE,"E6.bottom");var subQ3=sQuery(id+"F3.wireOp",EDGE,"E5.right");var subQ4=sQuery(id+"F3.wireOp",EDGE,"E5.top");var subQ5=sQuery(id+"F3.wireOp",EDGE,"E5.bottom");var subQ6=sQuery(id+"F3.wireOp",EDGE,"E4");var subQ7=sQuery(id+"F3.wireOp",EDGE,"E3");var subQ8=makeQuery(id+"F5.opFillet","BLEND_EDGE",EDGE,{"blendedFrom":[makeQuery(id+"F4.opExtrude","CAP_EDGE",EDGE,{"disambiguationData":[OSD([subQ6])],"isStart":false}),makeQuery(id+"F4.opExtrude","CAP_FACE",FACE,{"disambiguationData":[OSD([subQ7,subQ6,subQ5,subQ4,subQ3,subQ2,subQ1,subQ0])],"isStart":false})],"blendedInto":[makeQuery(id+"F4.opExtrude","CAP_FACE",FACE,{"disambiguationData":[OSD([subQ7,subQ6,subQ5,subQ4,subQ3,subQ2,subQ1,subQ0])],"isStart":false})]});Q35=makeQuery(id+"F7.boolean.opBoolean","MERGE",EDGE,{"derivedFrom":[subQ8,makeQuery(id+"F7.opExtrude","CAP_EDGE",EDGE,{"disambiguationData":[OSD([subQ7,subQ6,subQ5,subQ4,subQ3,subQ2,subQ1,subQ0]),TDD([makeQuery(id+"F6.imprint","IMPRINT",EDGE,{"disambiguationData":[TD([[makeQuery(id+"F6.imprint","INTERSECT",VERTEX,{"derivedFrom":[subQ8,sQuery(id+"F6.wireOp",EDGE,"E9.71.0")]}),-1.0]])],"derivedFrom":subQ8})])],"isStart":true})]});}
            var Q36;
            {var subQ0=sQuery(id+"F3.wireOp",EDGE,"E6.right");var subQ1=sQuery(id+"F3.wireOp",EDGE,"E6.top");var subQ2=sQuery(id+"F3.wireOp",EDGE,"E6.bottom");var subQ3=sQuery(id+"F3.wireOp",EDGE,"E5.right");var subQ4=sQuery(id+"F3.wireOp",EDGE,"E5.top");var subQ5=sQuery(id+"F3.wireOp",EDGE,"E5.bottom");var subQ6=sQuery(id+"F3.wireOp",EDGE,"E4");var subQ7=sQuery(id+"F3.wireOp",EDGE,"E3");var subQ8=makeQuery(id+"F5.opFillet","BLEND_EDGE",EDGE,{"blendedFrom":[makeQuery(id+"F4.opExtrude","CAP_EDGE",EDGE,{"disambiguationData":[OSD([subQ6])],"isStart":false}),makeQuery(id+"F4.opExtrude","CAP_FACE",FACE,{"disambiguationData":[OSD([subQ7,subQ6,subQ5,subQ4,subQ3,subQ2,subQ1,subQ0])],"isStart":false})],"blendedInto":[makeQuery(id+"F4.opExtrude","CAP_FACE",FACE,{"disambiguationData":[OSD([subQ7,subQ6,subQ5,subQ4,subQ3,subQ2,subQ1,subQ0])],"isStart":false})]});Q36=makeQuery(id+"F7.boolean.opBoolean","MERGE",EDGE,{"derivedFrom":[subQ8,makeQuery(id+"F7.opExtrude","CAP_EDGE",EDGE,{"disambiguationData":[OSD([subQ7,subQ6,subQ5,subQ4,subQ3,subQ2,subQ1,subQ0]),TDD([makeQuery(id+"F6.imprint","IMPRINT",EDGE,{"disambiguationData":[TD([[makeQuery(id+"F6.imprint","INTERSECT",VERTEX,{"derivedFrom":[subQ8,sQuery(id+"F6.wireOp",EDGE,"E9.73.0")]}),-1.0]])],"derivedFrom":subQ8})])],"isStart":true})]});}
            var Q37;
            {var subQ0=sQuery(id+"F3.wireOp",EDGE,"E6.right");var subQ1=sQuery(id+"F3.wireOp",EDGE,"E6.top");var subQ2=sQuery(id+"F3.wireOp",EDGE,"E6.bottom");var subQ3=sQuery(id+"F3.wireOp",EDGE,"E5.right");var subQ4=sQuery(id+"F3.wireOp",EDGE,"E5.top");var subQ5=sQuery(id+"F3.wireOp",EDGE,"E5.bottom");var subQ6=sQuery(id+"F3.wireOp",EDGE,"E4");var subQ7=sQuery(id+"F3.wireOp",EDGE,"E3");var subQ8=makeQuery(id+"F5.opFillet","BLEND_EDGE",EDGE,{"blendedFrom":[makeQuery(id+"F4.opExtrude","CAP_EDGE",EDGE,{"disambiguationData":[OSD([subQ6])],"isStart":false}),makeQuery(id+"F4.opExtrude","CAP_FACE",FACE,{"disambiguationData":[OSD([subQ7,subQ6,subQ5,subQ4,subQ3,subQ2,subQ1,subQ0])],"isStart":false})],"blendedInto":[makeQuery(id+"F4.opExtrude","CAP_FACE",FACE,{"disambiguationData":[OSD([subQ7,subQ6,subQ5,subQ4,subQ3,subQ2,subQ1,subQ0])],"isStart":false})]});Q37=makeQuery(id+"F7.boolean.opBoolean","MERGE",EDGE,{"derivedFrom":[subQ8,makeQuery(id+"F7.opExtrude","CAP_EDGE",EDGE,{"disambiguationData":[OSD([subQ7,subQ6,subQ5,subQ4,subQ3,subQ2,subQ1,subQ0]),TDD([makeQuery(id+"F6.imprint","IMPRINT",EDGE,{"disambiguationData":[TD([[makeQuery(id+"F6.imprint","INTERSECT",VERTEX,{"derivedFrom":[subQ8,sQuery(id+"F6.wireOp",EDGE,"E9.75.0")]}),-1.0]])],"derivedFrom":subQ8})])],"isStart":true})]});}
            var Q38;
            {var subQ0=sQuery(id+"F3.wireOp",EDGE,"E6.right");var subQ1=sQuery(id+"F3.wireOp",EDGE,"E6.top");var subQ2=sQuery(id+"F3.wireOp",EDGE,"E6.bottom");var subQ3=sQuery(id+"F3.wireOp",EDGE,"E5.right");var subQ4=sQuery(id+"F3.wireOp",EDGE,"E5.top");var subQ5=sQuery(id+"F3.wireOp",EDGE,"E5.bottom");var subQ6=sQuery(id+"F3.wireOp",EDGE,"E4");var subQ7=sQuery(id+"F3.wireOp",EDGE,"E3");var subQ8=makeQuery(id+"F5.opFillet","BLEND_EDGE",EDGE,{"blendedFrom":[makeQuery(id+"F4.opExtrude","CAP_EDGE",EDGE,{"disambiguationData":[OSD([subQ6])],"isStart":false}),makeQuery(id+"F4.opExtrude","CAP_FACE",FACE,{"disambiguationData":[OSD([subQ7,subQ6,subQ5,subQ4,subQ3,subQ2,subQ1,subQ0])],"isStart":false})],"blendedInto":[makeQuery(id+"F4.opExtrude","CAP_FACE",FACE,{"disambiguationData":[OSD([subQ7,subQ6,subQ5,subQ4,subQ3,subQ2,subQ1,subQ0])],"isStart":false})]});Q38=makeQuery(id+"F7.boolean.opBoolean","MERGE",EDGE,{"derivedFrom":[subQ8,makeQuery(id+"F7.opExtrude","CAP_EDGE",EDGE,{"disambiguationData":[OSD([subQ7,subQ6,subQ5,subQ4,subQ3,subQ2,subQ1,subQ0]),TDD([makeQuery(id+"F6.imprint","IMPRINT",EDGE,{"disambiguationData":[TD([[makeQuery(id+"F6.imprint","INTERSECT",VERTEX,{"derivedFrom":[subQ8,sQuery(id+"F6.wireOp",EDGE,"E9.77.0")]}),-1.0]])],"derivedFrom":subQ8})])],"isStart":true})]});}
            var Q39;
            {var subQ0=sQuery(id+"F3.wireOp",EDGE,"E6.right");var subQ1=sQuery(id+"F3.wireOp",EDGE,"E6.top");var subQ2=sQuery(id+"F3.wireOp",EDGE,"E6.bottom");var subQ3=sQuery(id+"F3.wireOp",EDGE,"E5.right");var subQ4=sQuery(id+"F3.wireOp",EDGE,"E5.top");var subQ5=sQuery(id+"F3.wireOp",EDGE,"E5.bottom");var subQ6=sQuery(id+"F3.wireOp",EDGE,"E4");var subQ7=sQuery(id+"F3.wireOp",EDGE,"E3");var subQ8=makeQuery(id+"F5.opFillet","BLEND_EDGE",EDGE,{"blendedFrom":[makeQuery(id+"F4.opExtrude","CAP_EDGE",EDGE,{"disambiguationData":[OSD([subQ2])],"isStart":false}),makeQuery(id+"F4.opExtrude","CAP_FACE",FACE,{"disambiguationData":[OSD([subQ7,subQ6,subQ5,subQ4,subQ3,subQ2,subQ1,subQ0])],"isStart":false})],"blendedInto":[makeQuery(id+"F4.opExtrude","CAP_FACE",FACE,{"disambiguationData":[OSD([subQ7,subQ6,subQ5,subQ4,subQ3,subQ2,subQ1,subQ0])],"isStart":false})]});Q39=makeQuery(id+"F7.boolean.opBoolean","MERGE",EDGE,{"derivedFrom":[subQ8,makeQuery(id+"F7.opExtrude","CAP_EDGE",EDGE,{"disambiguationData":[OSD([subQ7,subQ6,subQ5,subQ4,subQ3,subQ2,subQ1,subQ0]),TDD([makeQuery(id+"F6.imprint","IMPRINT",EDGE,{"derivedFrom":subQ8})])],"isStart":true})]});}
            fillet(context, id + "F10", {"entities" : qUnion([Q0, Q1, Q2, Q3, Q4, Q5, Q6, Q7, Q8, Q9, Q10, Q11, Q12, Q13, Q14, Q15, Q16, Q17, Q18, Q19, Q20, Q21, Q22, Q23, Q24, Q25, Q26, Q27, Q28, Q29, Q30, Q31, Q32, Q33, Q34, Q35, Q36, Q37, Q38, Q39]), "radius" : 1 * mm, "tangentPropagation" : true, "allowEdgeOverflow" : false});
        }
        {
            var Q0;
            {var subQ0=sQuery(id+"F3.wireOp",EDGE,"E6.right");var subQ1=sQuery(id+"F3.wireOp",EDGE,"E6.top");var subQ2=sQuery(id+"F3.wireOp",EDGE,"E6.bottom");var subQ3=sQuery(id+"F3.wireOp",EDGE,"E5.right");var subQ4=sQuery(id+"F3.wireOp",EDGE,"E5.top");var subQ5=sQuery(id+"F3.wireOp",EDGE,"E5.bottom");var subQ6=sQuery(id+"F3.wireOp",EDGE,"E4");var subQ7=sQuery(id+"F3.wireOp",EDGE,"E3");Q0=makeQuery(id+"F7.boolean.opBoolean","COPY",EDGE,{"derivedFrom":makeQuery(id+"F7.opExtrude","CAP_EDGE",EDGE,{"disambiguationData":[OSD([subQ7,subQ6,subQ5,subQ4,subQ3,subQ2,subQ1,subQ0]),TDD([makeQuery(id+"F6.imprint","IMPRINT",EDGE,{"derivedFrom":makeQuery(id+"F5.opFillet","BLEND_EDGE",EDGE,{"blendedFrom":[makeQuery(id+"F4.opExtrude","CAP_EDGE",EDGE,{"disambiguationData":[OSD([subQ5])],"isStart":false}),makeQuery(id+"F4.opExtrude","CAP_FACE",FACE,{"disambiguationData":[OSD([subQ7,subQ6,subQ5,subQ4,subQ3,subQ2,subQ1,subQ0])],"isStart":false})],"blendedInto":[makeQuery(id+"F4.opExtrude","CAP_FACE",FACE,{"disambiguationData":[OSD([subQ7,subQ6,subQ5,subQ4,subQ3,subQ2,subQ1,subQ0])],"isStart":false})]})})])],"isStart":false})});}
            var Q1;
            {var subQ0=sQuery(id+"F3.wireOp",EDGE,"E6.right");var subQ1=sQuery(id+"F3.wireOp",EDGE,"E6.top");var subQ2=sQuery(id+"F3.wireOp",EDGE,"E6.bottom");var subQ3=sQuery(id+"F3.wireOp",EDGE,"E5.right");var subQ4=sQuery(id+"F3.wireOp",EDGE,"E5.top");var subQ5=sQuery(id+"F3.wireOp",EDGE,"E5.bottom");var subQ6=sQuery(id+"F3.wireOp",EDGE,"E4");var subQ7=sQuery(id+"F3.wireOp",EDGE,"E3");var subQ8=makeQuery(id+"F5.opFillet","BLEND_EDGE",EDGE,{"blendedFrom":[makeQuery(id+"F4.opExtrude","CAP_EDGE",EDGE,{"disambiguationData":[OSD([subQ6])],"isStart":false}),makeQuery(id+"F4.opExtrude","CAP_FACE",FACE,{"disambiguationData":[OSD([subQ7,subQ6,subQ5,subQ4,subQ3,subQ2,subQ1,subQ0])],"isStart":false})],"blendedInto":[makeQuery(id+"F4.opExtrude","CAP_FACE",FACE,{"disambiguationData":[OSD([subQ7,subQ6,subQ5,subQ4,subQ3,subQ2,subQ1,subQ0])],"isStart":false})]});var subQ9=sQuery(id+"F6.wireOp",EDGE,"E9.2.0");Q1=makeQuery(id+"F9.opFillet","BLEND_EDGE",EDGE,{"blendedFrom":[makeQuery(id+"F7.boolean.opBoolean","COPY",EDGE,{"derivedFrom":makeQuery(id+"F7.opExtrude","CAP_EDGE",EDGE,{"disambiguationData":[OSD([subQ9])],"isStart":false})}),makeQuery(id+"F7.boolean.opBoolean","COPY",FACE,{"derivedFrom":makeQuery(id+"F7.opExtrude","SWEPT_FACE",FACE,{"disambiguationData":[OSD([subQ7,subQ6,subQ5,subQ4,subQ3,subQ2,subQ1,subQ0]),TDD([makeQuery(id+"F6.imprint","IMPRINT",EDGE,{"disambiguationData":[TD([[makeQuery(id+"F6.imprint","INTERSECT",VERTEX,{"derivedFrom":[subQ8,sQuery(id+"F6.wireOp",EDGE,"E9.1.0")]}),-1.0]])],"derivedFrom":subQ8})])]})})],"blendedInto":[makeQuery(id+"F7.boolean.opBoolean","COPY",FACE,{"derivedFrom":makeQuery(id+"F7.opExtrude","SWEPT_FACE",FACE,{"disambiguationData":[OSD([subQ7,subQ6,subQ5,subQ4,subQ3,subQ2,subQ1,subQ0]),TDD([makeQuery(id+"F6.imprint","IMPRINT",EDGE,{"disambiguationData":[TD([[makeQuery(id+"F6.imprint","INTERSECT",VERTEX,{"derivedFrom":[subQ8,sQuery(id+"F6.wireOp",EDGE,"E9.1.0")]}),-1.0]])],"derivedFrom":subQ8})])]})})]});}
            var Q2;
            {var subQ0=sQuery(id+"F3.wireOp",EDGE,"E6.right");var subQ1=sQuery(id+"F3.wireOp",EDGE,"E6.top");var subQ2=sQuery(id+"F3.wireOp",EDGE,"E6.bottom");var subQ3=sQuery(id+"F3.wireOp",EDGE,"E5.right");var subQ4=sQuery(id+"F3.wireOp",EDGE,"E5.top");var subQ5=sQuery(id+"F3.wireOp",EDGE,"E5.bottom");var subQ6=sQuery(id+"F3.wireOp",EDGE,"E4");var subQ7=sQuery(id+"F3.wireOp",EDGE,"E3");var subQ8=makeQuery(id+"F5.opFillet","BLEND_EDGE",EDGE,{"blendedFrom":[makeQuery(id+"F4.opExtrude","CAP_EDGE",EDGE,{"disambiguationData":[OSD([subQ6])],"isStart":false}),makeQuery(id+"F4.opExtrude","CAP_FACE",FACE,{"disambiguationData":[OSD([subQ7,subQ6,subQ5,subQ4,subQ3,subQ2,subQ1,subQ0])],"isStart":false})],"blendedInto":[makeQuery(id+"F4.opExtrude","CAP_FACE",FACE,{"disambiguationData":[OSD([subQ7,subQ6,subQ5,subQ4,subQ3,subQ2,subQ1,subQ0])],"isStart":false})]});var subQ9=sQuery(id+"F6.wireOp",EDGE,"E9.4.0");Q2=makeQuery(id+"F9.opFillet","BLEND_EDGE",EDGE,{"blendedFrom":[makeQuery(id+"F7.boolean.opBoolean","COPY",EDGE,{"derivedFrom":makeQuery(id+"F7.opExtrude","CAP_EDGE",EDGE,{"disambiguationData":[OSD([subQ9])],"isStart":false})}),makeQuery(id+"F7.boolean.opBoolean","COPY",FACE,{"derivedFrom":makeQuery(id+"F7.opExtrude","SWEPT_FACE",FACE,{"disambiguationData":[OSD([subQ7,subQ6,subQ5,subQ4,subQ3,subQ2,subQ1,subQ0]),TDD([makeQuery(id+"F6.imprint","IMPRINT",EDGE,{"disambiguationData":[TD([[makeQuery(id+"F6.imprint","INTERSECT",VERTEX,{"derivedFrom":[subQ8,sQuery(id+"F6.wireOp",EDGE,"E9.3.0")]}),-1.0]])],"derivedFrom":subQ8})])]})})],"blendedInto":[makeQuery(id+"F7.boolean.opBoolean","COPY",FACE,{"derivedFrom":makeQuery(id+"F7.opExtrude","SWEPT_FACE",FACE,{"disambiguationData":[OSD([subQ7,subQ6,subQ5,subQ4,subQ3,subQ2,subQ1,subQ0]),TDD([makeQuery(id+"F6.imprint","IMPRINT",EDGE,{"disambiguationData":[TD([[makeQuery(id+"F6.imprint","INTERSECT",VERTEX,{"derivedFrom":[subQ8,sQuery(id+"F6.wireOp",EDGE,"E9.3.0")]}),-1.0]])],"derivedFrom":subQ8})])]})})]});}
            var Q3;
            {var subQ0=sQuery(id+"F3.wireOp",EDGE,"E6.right");var subQ1=sQuery(id+"F3.wireOp",EDGE,"E6.top");var subQ2=sQuery(id+"F3.wireOp",EDGE,"E6.bottom");var subQ3=sQuery(id+"F3.wireOp",EDGE,"E5.right");var subQ4=sQuery(id+"F3.wireOp",EDGE,"E5.top");var subQ5=sQuery(id+"F3.wireOp",EDGE,"E5.bottom");var subQ6=sQuery(id+"F3.wireOp",EDGE,"E4");var subQ7=sQuery(id+"F3.wireOp",EDGE,"E3");var subQ8=makeQuery(id+"F5.opFillet","BLEND_EDGE",EDGE,{"blendedFrom":[makeQuery(id+"F4.opExtrude","CAP_EDGE",EDGE,{"disambiguationData":[OSD([subQ6])],"isStart":false}),makeQuery(id+"F4.opExtrude","CAP_FACE",FACE,{"disambiguationData":[OSD([subQ7,subQ6,subQ5,subQ4,subQ3,subQ2,subQ1,subQ0])],"isStart":false})],"blendedInto":[makeQuery(id+"F4.opExtrude","CAP_FACE",FACE,{"disambiguationData":[OSD([subQ7,subQ6,subQ5,subQ4,subQ3,subQ2,subQ1,subQ0])],"isStart":false})]});var subQ9=sQuery(id+"F6.wireOp",EDGE,"E9.6.0");Q3=makeQuery(id+"F9.opFillet","BLEND_EDGE",EDGE,{"blendedFrom":[makeQuery(id+"F7.boolean.opBoolean","COPY",EDGE,{"derivedFrom":makeQuery(id+"F7.opExtrude","CAP_EDGE",EDGE,{"disambiguationData":[OSD([subQ9])],"isStart":false})}),makeQuery(id+"F7.boolean.opBoolean","COPY",FACE,{"derivedFrom":makeQuery(id+"F7.opExtrude","SWEPT_FACE",FACE,{"disambiguationData":[OSD([subQ7,subQ6,subQ5,subQ4,subQ3,subQ2,subQ1,subQ0]),TDD([makeQuery(id+"F6.imprint","IMPRINT",EDGE,{"disambiguationData":[TD([[makeQuery(id+"F6.imprint","INTERSECT",VERTEX,{"derivedFrom":[subQ8,sQuery(id+"F6.wireOp",EDGE,"E9.5.0")]}),-1.0]])],"derivedFrom":subQ8})])]})})],"blendedInto":[makeQuery(id+"F7.boolean.opBoolean","COPY",FACE,{"derivedFrom":makeQuery(id+"F7.opExtrude","SWEPT_FACE",FACE,{"disambiguationData":[OSD([subQ7,subQ6,subQ5,subQ4,subQ3,subQ2,subQ1,subQ0]),TDD([makeQuery(id+"F6.imprint","IMPRINT",EDGE,{"disambiguationData":[TD([[makeQuery(id+"F6.imprint","INTERSECT",VERTEX,{"derivedFrom":[subQ8,sQuery(id+"F6.wireOp",EDGE,"E9.5.0")]}),-1.0]])],"derivedFrom":subQ8})])]})})]});}
            var Q4;
            {var subQ0=sQuery(id+"F3.wireOp",EDGE,"E6.right");var subQ1=sQuery(id+"F3.wireOp",EDGE,"E6.top");var subQ2=sQuery(id+"F3.wireOp",EDGE,"E6.bottom");var subQ3=sQuery(id+"F3.wireOp",EDGE,"E5.right");var subQ4=sQuery(id+"F3.wireOp",EDGE,"E5.top");var subQ5=sQuery(id+"F3.wireOp",EDGE,"E5.bottom");var subQ6=sQuery(id+"F3.wireOp",EDGE,"E4");var subQ7=sQuery(id+"F3.wireOp",EDGE,"E3");var subQ8=makeQuery(id+"F5.opFillet","BLEND_EDGE",EDGE,{"blendedFrom":[makeQuery(id+"F4.opExtrude","CAP_EDGE",EDGE,{"disambiguationData":[OSD([subQ6])],"isStart":false}),makeQuery(id+"F4.opExtrude","CAP_FACE",FACE,{"disambiguationData":[OSD([subQ7,subQ6,subQ5,subQ4,subQ3,subQ2,subQ1,subQ0])],"isStart":false})],"blendedInto":[makeQuery(id+"F4.opExtrude","CAP_FACE",FACE,{"disambiguationData":[OSD([subQ7,subQ6,subQ5,subQ4,subQ3,subQ2,subQ1,subQ0])],"isStart":false})]});var subQ9=sQuery(id+"F6.wireOp",EDGE,"E9.8.0");Q4=makeQuery(id+"F9.opFillet","BLEND_EDGE",EDGE,{"blendedFrom":[makeQuery(id+"F7.boolean.opBoolean","COPY",EDGE,{"derivedFrom":makeQuery(id+"F7.opExtrude","CAP_EDGE",EDGE,{"disambiguationData":[OSD([subQ9])],"isStart":false})}),makeQuery(id+"F7.boolean.opBoolean","COPY",FACE,{"derivedFrom":makeQuery(id+"F7.opExtrude","SWEPT_FACE",FACE,{"disambiguationData":[OSD([subQ7,subQ6,subQ5,subQ4,subQ3,subQ2,subQ1,subQ0]),TDD([makeQuery(id+"F6.imprint","IMPRINT",EDGE,{"disambiguationData":[TD([[makeQuery(id+"F6.imprint","INTERSECT",VERTEX,{"derivedFrom":[subQ8,sQuery(id+"F6.wireOp",EDGE,"E9.7.0")]}),-1.0]])],"derivedFrom":subQ8})])]})})],"blendedInto":[makeQuery(id+"F7.boolean.opBoolean","COPY",FACE,{"derivedFrom":makeQuery(id+"F7.opExtrude","SWEPT_FACE",FACE,{"disambiguationData":[OSD([subQ7,subQ6,subQ5,subQ4,subQ3,subQ2,subQ1,subQ0]),TDD([makeQuery(id+"F6.imprint","IMPRINT",EDGE,{"disambiguationData":[TD([[makeQuery(id+"F6.imprint","INTERSECT",VERTEX,{"derivedFrom":[subQ8,sQuery(id+"F6.wireOp",EDGE,"E9.7.0")]}),-1.0]])],"derivedFrom":subQ8})])]})})]});}
            var Q5;
            {var subQ0=sQuery(id+"F3.wireOp",EDGE,"E6.right");var subQ1=sQuery(id+"F3.wireOp",EDGE,"E6.top");var subQ2=sQuery(id+"F3.wireOp",EDGE,"E6.bottom");var subQ3=sQuery(id+"F3.wireOp",EDGE,"E5.right");var subQ4=sQuery(id+"F3.wireOp",EDGE,"E5.top");var subQ5=sQuery(id+"F3.wireOp",EDGE,"E5.bottom");var subQ6=sQuery(id+"F3.wireOp",EDGE,"E4");var subQ7=sQuery(id+"F3.wireOp",EDGE,"E3");var subQ8=makeQuery(id+"F5.opFillet","BLEND_EDGE",EDGE,{"blendedFrom":[makeQuery(id+"F4.opExtrude","CAP_EDGE",EDGE,{"disambiguationData":[OSD([subQ6])],"isStart":false}),makeQuery(id+"F4.opExtrude","CAP_FACE",FACE,{"disambiguationData":[OSD([subQ7,subQ6,subQ5,subQ4,subQ3,subQ2,subQ1,subQ0])],"isStart":false})],"blendedInto":[makeQuery(id+"F4.opExtrude","CAP_FACE",FACE,{"disambiguationData":[OSD([subQ7,subQ6,subQ5,subQ4,subQ3,subQ2,subQ1,subQ0])],"isStart":false})]});var subQ9=sQuery(id+"F6.wireOp",EDGE,"E9.10.0");Q5=makeQuery(id+"F9.opFillet","BLEND_EDGE",EDGE,{"blendedFrom":[makeQuery(id+"F7.boolean.opBoolean","COPY",EDGE,{"derivedFrom":makeQuery(id+"F7.opExtrude","CAP_EDGE",EDGE,{"disambiguationData":[OSD([subQ9])],"isStart":false})}),makeQuery(id+"F7.boolean.opBoolean","COPY",FACE,{"derivedFrom":makeQuery(id+"F7.opExtrude","SWEPT_FACE",FACE,{"disambiguationData":[OSD([subQ7,subQ6,subQ5,subQ4,subQ3,subQ2,subQ1,subQ0]),TDD([makeQuery(id+"F6.imprint","IMPRINT",EDGE,{"disambiguationData":[TD([[makeQuery(id+"F6.imprint","INTERSECT",VERTEX,{"derivedFrom":[subQ8,sQuery(id+"F6.wireOp",EDGE,"E9.9.0")]}),-1.0]])],"derivedFrom":subQ8})])]})})],"blendedInto":[makeQuery(id+"F7.boolean.opBoolean","COPY",FACE,{"derivedFrom":makeQuery(id+"F7.opExtrude","SWEPT_FACE",FACE,{"disambiguationData":[OSD([subQ7,subQ6,subQ5,subQ4,subQ3,subQ2,subQ1,subQ0]),TDD([makeQuery(id+"F6.imprint","IMPRINT",EDGE,{"disambiguationData":[TD([[makeQuery(id+"F6.imprint","INTERSECT",VERTEX,{"derivedFrom":[subQ8,sQuery(id+"F6.wireOp",EDGE,"E9.9.0")]}),-1.0]])],"derivedFrom":subQ8})])]})})]});}
            var Q6;
            {var subQ0=sQuery(id+"F3.wireOp",EDGE,"E6.right");var subQ1=sQuery(id+"F3.wireOp",EDGE,"E6.top");var subQ2=sQuery(id+"F3.wireOp",EDGE,"E6.bottom");var subQ3=sQuery(id+"F3.wireOp",EDGE,"E5.right");var subQ4=sQuery(id+"F3.wireOp",EDGE,"E5.top");var subQ5=sQuery(id+"F3.wireOp",EDGE,"E5.bottom");var subQ6=sQuery(id+"F3.wireOp",EDGE,"E4");var subQ7=sQuery(id+"F3.wireOp",EDGE,"E3");var subQ8=makeQuery(id+"F5.opFillet","BLEND_EDGE",EDGE,{"blendedFrom":[makeQuery(id+"F4.opExtrude","CAP_EDGE",EDGE,{"disambiguationData":[OSD([subQ6])],"isStart":false}),makeQuery(id+"F4.opExtrude","CAP_FACE",FACE,{"disambiguationData":[OSD([subQ7,subQ6,subQ5,subQ4,subQ3,subQ2,subQ1,subQ0])],"isStart":false})],"blendedInto":[makeQuery(id+"F4.opExtrude","CAP_FACE",FACE,{"disambiguationData":[OSD([subQ7,subQ6,subQ5,subQ4,subQ3,subQ2,subQ1,subQ0])],"isStart":false})]});var subQ9=sQuery(id+"F6.wireOp",EDGE,"E9.12.0");Q6=makeQuery(id+"F9.opFillet","BLEND_EDGE",EDGE,{"blendedFrom":[makeQuery(id+"F7.boolean.opBoolean","COPY",EDGE,{"derivedFrom":makeQuery(id+"F7.opExtrude","CAP_EDGE",EDGE,{"disambiguationData":[OSD([subQ9])],"isStart":false})}),makeQuery(id+"F7.boolean.opBoolean","COPY",FACE,{"derivedFrom":makeQuery(id+"F7.opExtrude","SWEPT_FACE",FACE,{"disambiguationData":[OSD([subQ7,subQ6,subQ5,subQ4,subQ3,subQ2,subQ1,subQ0]),TDD([makeQuery(id+"F6.imprint","IMPRINT",EDGE,{"disambiguationData":[TD([[makeQuery(id+"F6.imprint","INTERSECT",VERTEX,{"derivedFrom":[subQ8,sQuery(id+"F6.wireOp",EDGE,"E9.11.0")]}),-1.0]])],"derivedFrom":subQ8})])]})})],"blendedInto":[makeQuery(id+"F7.boolean.opBoolean","COPY",FACE,{"derivedFrom":makeQuery(id+"F7.opExtrude","SWEPT_FACE",FACE,{"disambiguationData":[OSD([subQ7,subQ6,subQ5,subQ4,subQ3,subQ2,subQ1,subQ0]),TDD([makeQuery(id+"F6.imprint","IMPRINT",EDGE,{"disambiguationData":[TD([[makeQuery(id+"F6.imprint","INTERSECT",VERTEX,{"derivedFrom":[subQ8,sQuery(id+"F6.wireOp",EDGE,"E9.11.0")]}),-1.0]])],"derivedFrom":subQ8})])]})})]});}
            var Q7;
            {var subQ0=sQuery(id+"F3.wireOp",EDGE,"E6.right");var subQ1=sQuery(id+"F3.wireOp",EDGE,"E6.top");var subQ2=sQuery(id+"F3.wireOp",EDGE,"E6.bottom");var subQ3=sQuery(id+"F3.wireOp",EDGE,"E5.right");var subQ4=sQuery(id+"F3.wireOp",EDGE,"E5.top");var subQ5=sQuery(id+"F3.wireOp",EDGE,"E5.bottom");var subQ6=sQuery(id+"F3.wireOp",EDGE,"E4");var subQ7=sQuery(id+"F3.wireOp",EDGE,"E3");var subQ8=makeQuery(id+"F5.opFillet","BLEND_EDGE",EDGE,{"blendedFrom":[makeQuery(id+"F4.opExtrude","CAP_EDGE",EDGE,{"disambiguationData":[OSD([subQ6])],"isStart":false}),makeQuery(id+"F4.opExtrude","CAP_FACE",FACE,{"disambiguationData":[OSD([subQ7,subQ6,subQ5,subQ4,subQ3,subQ2,subQ1,subQ0])],"isStart":false})],"blendedInto":[makeQuery(id+"F4.opExtrude","CAP_FACE",FACE,{"disambiguationData":[OSD([subQ7,subQ6,subQ5,subQ4,subQ3,subQ2,subQ1,subQ0])],"isStart":false})]});var subQ9=sQuery(id+"F6.wireOp",EDGE,"E9.14.0");Q7=makeQuery(id+"F9.opFillet","BLEND_EDGE",EDGE,{"blendedFrom":[makeQuery(id+"F7.boolean.opBoolean","COPY",EDGE,{"derivedFrom":makeQuery(id+"F7.opExtrude","CAP_EDGE",EDGE,{"disambiguationData":[OSD([subQ9])],"isStart":false})}),makeQuery(id+"F7.boolean.opBoolean","COPY",FACE,{"derivedFrom":makeQuery(id+"F7.opExtrude","SWEPT_FACE",FACE,{"disambiguationData":[OSD([subQ7,subQ6,subQ5,subQ4,subQ3,subQ2,subQ1,subQ0]),TDD([makeQuery(id+"F6.imprint","IMPRINT",EDGE,{"disambiguationData":[TD([[makeQuery(id+"F6.imprint","INTERSECT",VERTEX,{"derivedFrom":[subQ8,sQuery(id+"F6.wireOp",EDGE,"E9.13.0")]}),-1.0]])],"derivedFrom":subQ8})])]})})],"blendedInto":[makeQuery(id+"F7.boolean.opBoolean","COPY",FACE,{"derivedFrom":makeQuery(id+"F7.opExtrude","SWEPT_FACE",FACE,{"disambiguationData":[OSD([subQ7,subQ6,subQ5,subQ4,subQ3,subQ2,subQ1,subQ0]),TDD([makeQuery(id+"F6.imprint","IMPRINT",EDGE,{"disambiguationData":[TD([[makeQuery(id+"F6.imprint","INTERSECT",VERTEX,{"derivedFrom":[subQ8,sQuery(id+"F6.wireOp",EDGE,"E9.13.0")]}),-1.0]])],"derivedFrom":subQ8})])]})})]});}
            var Q8;
            {var subQ0=sQuery(id+"F3.wireOp",EDGE,"E6.right");var subQ1=sQuery(id+"F3.wireOp",EDGE,"E6.top");var subQ2=sQuery(id+"F3.wireOp",EDGE,"E6.bottom");var subQ3=sQuery(id+"F3.wireOp",EDGE,"E5.right");var subQ4=sQuery(id+"F3.wireOp",EDGE,"E5.top");var subQ5=sQuery(id+"F3.wireOp",EDGE,"E5.bottom");var subQ6=sQuery(id+"F3.wireOp",EDGE,"E4");var subQ7=sQuery(id+"F3.wireOp",EDGE,"E3");var subQ8=makeQuery(id+"F5.opFillet","BLEND_EDGE",EDGE,{"blendedFrom":[makeQuery(id+"F4.opExtrude","CAP_EDGE",EDGE,{"disambiguationData":[OSD([subQ6])],"isStart":false}),makeQuery(id+"F4.opExtrude","CAP_FACE",FACE,{"disambiguationData":[OSD([subQ7,subQ6,subQ5,subQ4,subQ3,subQ2,subQ1,subQ0])],"isStart":false})],"blendedInto":[makeQuery(id+"F4.opExtrude","CAP_FACE",FACE,{"disambiguationData":[OSD([subQ7,subQ6,subQ5,subQ4,subQ3,subQ2,subQ1,subQ0])],"isStart":false})]});var subQ9=sQuery(id+"F6.wireOp",EDGE,"E9.16.0");Q8=makeQuery(id+"F9.opFillet","BLEND_EDGE",EDGE,{"blendedFrom":[makeQuery(id+"F7.boolean.opBoolean","COPY",EDGE,{"derivedFrom":makeQuery(id+"F7.opExtrude","CAP_EDGE",EDGE,{"disambiguationData":[OSD([subQ9])],"isStart":false})}),makeQuery(id+"F7.boolean.opBoolean","COPY",FACE,{"derivedFrom":makeQuery(id+"F7.opExtrude","SWEPT_FACE",FACE,{"disambiguationData":[OSD([subQ7,subQ6,subQ5,subQ4,subQ3,subQ2,subQ1,subQ0]),TDD([makeQuery(id+"F6.imprint","IMPRINT",EDGE,{"disambiguationData":[TD([[makeQuery(id+"F6.imprint","INTERSECT",VERTEX,{"derivedFrom":[subQ8,sQuery(id+"F6.wireOp",EDGE,"E9.15.0")]}),-1.0]])],"derivedFrom":subQ8})])]})})],"blendedInto":[makeQuery(id+"F7.boolean.opBoolean","COPY",FACE,{"derivedFrom":makeQuery(id+"F7.opExtrude","SWEPT_FACE",FACE,{"disambiguationData":[OSD([subQ7,subQ6,subQ5,subQ4,subQ3,subQ2,subQ1,subQ0]),TDD([makeQuery(id+"F6.imprint","IMPRINT",EDGE,{"disambiguationData":[TD([[makeQuery(id+"F6.imprint","INTERSECT",VERTEX,{"derivedFrom":[subQ8,sQuery(id+"F6.wireOp",EDGE,"E9.15.0")]}),-1.0]])],"derivedFrom":subQ8})])]})})]});}
            var Q9;
            {var subQ0=sQuery(id+"F3.wireOp",EDGE,"E6.right");var subQ1=sQuery(id+"F3.wireOp",EDGE,"E6.top");var subQ2=sQuery(id+"F3.wireOp",EDGE,"E6.bottom");var subQ3=sQuery(id+"F3.wireOp",EDGE,"E5.right");var subQ4=sQuery(id+"F3.wireOp",EDGE,"E5.top");var subQ5=sQuery(id+"F3.wireOp",EDGE,"E5.bottom");var subQ6=sQuery(id+"F3.wireOp",EDGE,"E4");var subQ7=sQuery(id+"F3.wireOp",EDGE,"E3");var subQ8=makeQuery(id+"F5.opFillet","BLEND_EDGE",EDGE,{"blendedFrom":[makeQuery(id+"F4.opExtrude","CAP_EDGE",EDGE,{"disambiguationData":[OSD([subQ6])],"isStart":false}),makeQuery(id+"F4.opExtrude","CAP_FACE",FACE,{"disambiguationData":[OSD([subQ7,subQ6,subQ5,subQ4,subQ3,subQ2,subQ1,subQ0])],"isStart":false})],"blendedInto":[makeQuery(id+"F4.opExtrude","CAP_FACE",FACE,{"disambiguationData":[OSD([subQ7,subQ6,subQ5,subQ4,subQ3,subQ2,subQ1,subQ0])],"isStart":false})]});var subQ9=sQuery(id+"F6.wireOp",EDGE,"E9.18.0");Q9=makeQuery(id+"F9.opFillet","BLEND_EDGE",EDGE,{"blendedFrom":[makeQuery(id+"F7.boolean.opBoolean","COPY",EDGE,{"derivedFrom":makeQuery(id+"F7.opExtrude","CAP_EDGE",EDGE,{"disambiguationData":[OSD([subQ9])],"isStart":false})}),makeQuery(id+"F7.boolean.opBoolean","COPY",FACE,{"derivedFrom":makeQuery(id+"F7.opExtrude","SWEPT_FACE",FACE,{"disambiguationData":[OSD([subQ7,subQ6,subQ5,subQ4,subQ3,subQ2,subQ1,subQ0]),TDD([makeQuery(id+"F6.imprint","IMPRINT",EDGE,{"disambiguationData":[TD([[makeQuery(id+"F6.imprint","INTERSECT",VERTEX,{"derivedFrom":[subQ8,sQuery(id+"F6.wireOp",EDGE,"E9.17.0")]}),-1.0]])],"derivedFrom":subQ8})])]})})],"blendedInto":[makeQuery(id+"F7.boolean.opBoolean","COPY",FACE,{"derivedFrom":makeQuery(id+"F7.opExtrude","SWEPT_FACE",FACE,{"disambiguationData":[OSD([subQ7,subQ6,subQ5,subQ4,subQ3,subQ2,subQ1,subQ0]),TDD([makeQuery(id+"F6.imprint","IMPRINT",EDGE,{"disambiguationData":[TD([[makeQuery(id+"F6.imprint","INTERSECT",VERTEX,{"derivedFrom":[subQ8,sQuery(id+"F6.wireOp",EDGE,"E9.17.0")]}),-1.0]])],"derivedFrom":subQ8})])]})})]});}
            var Q10;
            {var subQ0=sQuery(id+"F3.wireOp",EDGE,"E6.right");var subQ1=sQuery(id+"F3.wireOp",EDGE,"E6.top");var subQ2=sQuery(id+"F3.wireOp",EDGE,"E6.bottom");var subQ3=sQuery(id+"F3.wireOp",EDGE,"E5.right");var subQ4=sQuery(id+"F3.wireOp",EDGE,"E5.top");var subQ5=sQuery(id+"F3.wireOp",EDGE,"E5.bottom");var subQ6=sQuery(id+"F3.wireOp",EDGE,"E4");var subQ7=sQuery(id+"F3.wireOp",EDGE,"E3");var subQ8=makeQuery(id+"F5.opFillet","BLEND_EDGE",EDGE,{"blendedFrom":[makeQuery(id+"F4.opExtrude","CAP_EDGE",EDGE,{"disambiguationData":[OSD([subQ6])],"isStart":false}),makeQuery(id+"F4.opExtrude","CAP_FACE",FACE,{"disambiguationData":[OSD([subQ7,subQ6,subQ5,subQ4,subQ3,subQ2,subQ1,subQ0])],"isStart":false})],"blendedInto":[makeQuery(id+"F4.opExtrude","CAP_FACE",FACE,{"disambiguationData":[OSD([subQ7,subQ6,subQ5,subQ4,subQ3,subQ2,subQ1,subQ0])],"isStart":false})]});var subQ9=sQuery(id+"F6.wireOp",EDGE,"E9.20.0");Q10=makeQuery(id+"F9.opFillet","BLEND_EDGE",EDGE,{"blendedFrom":[makeQuery(id+"F7.boolean.opBoolean","COPY",EDGE,{"derivedFrom":makeQuery(id+"F7.opExtrude","CAP_EDGE",EDGE,{"disambiguationData":[OSD([subQ9])],"isStart":false})}),makeQuery(id+"F7.boolean.opBoolean","COPY",FACE,{"derivedFrom":makeQuery(id+"F7.opExtrude","SWEPT_FACE",FACE,{"disambiguationData":[OSD([subQ7,subQ6,subQ5,subQ4,subQ3,subQ2,subQ1,subQ0]),TDD([makeQuery(id+"F6.imprint","IMPRINT",EDGE,{"disambiguationData":[TD([[makeQuery(id+"F6.imprint","INTERSECT",VERTEX,{"derivedFrom":[subQ8,sQuery(id+"F6.wireOp",EDGE,"E9.19.0")]}),-1.0]])],"derivedFrom":subQ8})])]})})],"blendedInto":[makeQuery(id+"F7.boolean.opBoolean","COPY",FACE,{"derivedFrom":makeQuery(id+"F7.opExtrude","SWEPT_FACE",FACE,{"disambiguationData":[OSD([subQ7,subQ6,subQ5,subQ4,subQ3,subQ2,subQ1,subQ0]),TDD([makeQuery(id+"F6.imprint","IMPRINT",EDGE,{"disambiguationData":[TD([[makeQuery(id+"F6.imprint","INTERSECT",VERTEX,{"derivedFrom":[subQ8,sQuery(id+"F6.wireOp",EDGE,"E9.19.0")]}),-1.0]])],"derivedFrom":subQ8})])]})})]});}
            var Q11;
            {var subQ0=sQuery(id+"F3.wireOp",EDGE,"E6.right");var subQ1=sQuery(id+"F3.wireOp",EDGE,"E6.top");var subQ2=sQuery(id+"F3.wireOp",EDGE,"E6.bottom");var subQ3=sQuery(id+"F3.wireOp",EDGE,"E5.right");var subQ4=sQuery(id+"F3.wireOp",EDGE,"E5.top");var subQ5=sQuery(id+"F3.wireOp",EDGE,"E5.bottom");var subQ6=sQuery(id+"F3.wireOp",EDGE,"E4");var subQ7=sQuery(id+"F3.wireOp",EDGE,"E3");var subQ8=makeQuery(id+"F5.opFillet","BLEND_EDGE",EDGE,{"blendedFrom":[makeQuery(id+"F4.opExtrude","CAP_EDGE",EDGE,{"disambiguationData":[OSD([subQ6])],"isStart":false}),makeQuery(id+"F4.opExtrude","CAP_FACE",FACE,{"disambiguationData":[OSD([subQ7,subQ6,subQ5,subQ4,subQ3,subQ2,subQ1,subQ0])],"isStart":false})],"blendedInto":[makeQuery(id+"F4.opExtrude","CAP_FACE",FACE,{"disambiguationData":[OSD([subQ7,subQ6,subQ5,subQ4,subQ3,subQ2,subQ1,subQ0])],"isStart":false})]});var subQ9=sQuery(id+"F6.wireOp",EDGE,"E9.22.0");Q11=makeQuery(id+"F9.opFillet","BLEND_EDGE",EDGE,{"blendedFrom":[makeQuery(id+"F7.boolean.opBoolean","COPY",EDGE,{"derivedFrom":makeQuery(id+"F7.opExtrude","CAP_EDGE",EDGE,{"disambiguationData":[OSD([subQ9])],"isStart":false})}),makeQuery(id+"F7.boolean.opBoolean","COPY",FACE,{"derivedFrom":makeQuery(id+"F7.opExtrude","SWEPT_FACE",FACE,{"disambiguationData":[OSD([subQ7,subQ6,subQ5,subQ4,subQ3,subQ2,subQ1,subQ0]),TDD([makeQuery(id+"F6.imprint","IMPRINT",EDGE,{"disambiguationData":[TD([[makeQuery(id+"F6.imprint","INTERSECT",VERTEX,{"derivedFrom":[subQ8,sQuery(id+"F6.wireOp",EDGE,"E9.21.0")]}),-1.0]])],"derivedFrom":subQ8})])]})})],"blendedInto":[makeQuery(id+"F7.boolean.opBoolean","COPY",FACE,{"derivedFrom":makeQuery(id+"F7.opExtrude","SWEPT_FACE",FACE,{"disambiguationData":[OSD([subQ7,subQ6,subQ5,subQ4,subQ3,subQ2,subQ1,subQ0]),TDD([makeQuery(id+"F6.imprint","IMPRINT",EDGE,{"disambiguationData":[TD([[makeQuery(id+"F6.imprint","INTERSECT",VERTEX,{"derivedFrom":[subQ8,sQuery(id+"F6.wireOp",EDGE,"E9.21.0")]}),-1.0]])],"derivedFrom":subQ8})])]})})]});}
            var Q12;
            {var subQ0=sQuery(id+"F3.wireOp",EDGE,"E6.right");var subQ1=sQuery(id+"F3.wireOp",EDGE,"E6.top");var subQ2=sQuery(id+"F3.wireOp",EDGE,"E6.bottom");var subQ3=sQuery(id+"F3.wireOp",EDGE,"E5.right");var subQ4=sQuery(id+"F3.wireOp",EDGE,"E5.top");var subQ5=sQuery(id+"F3.wireOp",EDGE,"E5.bottom");var subQ6=sQuery(id+"F3.wireOp",EDGE,"E4");var subQ7=sQuery(id+"F3.wireOp",EDGE,"E3");var subQ8=makeQuery(id+"F5.opFillet","BLEND_EDGE",EDGE,{"blendedFrom":[makeQuery(id+"F4.opExtrude","CAP_EDGE",EDGE,{"disambiguationData":[OSD([subQ6])],"isStart":false}),makeQuery(id+"F4.opExtrude","CAP_FACE",FACE,{"disambiguationData":[OSD([subQ7,subQ6,subQ5,subQ4,subQ3,subQ2,subQ1,subQ0])],"isStart":false})],"blendedInto":[makeQuery(id+"F4.opExtrude","CAP_FACE",FACE,{"disambiguationData":[OSD([subQ7,subQ6,subQ5,subQ4,subQ3,subQ2,subQ1,subQ0])],"isStart":false})]});var subQ9=sQuery(id+"F6.wireOp",EDGE,"E9.24.0");Q12=makeQuery(id+"F9.opFillet","BLEND_EDGE",EDGE,{"blendedFrom":[makeQuery(id+"F7.boolean.opBoolean","COPY",EDGE,{"derivedFrom":makeQuery(id+"F7.opExtrude","CAP_EDGE",EDGE,{"disambiguationData":[OSD([subQ9])],"isStart":false})}),makeQuery(id+"F7.boolean.opBoolean","COPY",FACE,{"derivedFrom":makeQuery(id+"F7.opExtrude","SWEPT_FACE",FACE,{"disambiguationData":[OSD([subQ7,subQ6,subQ5,subQ4,subQ3,subQ2,subQ1,subQ0]),TDD([makeQuery(id+"F6.imprint","IMPRINT",EDGE,{"disambiguationData":[TD([[makeQuery(id+"F6.imprint","INTERSECT",VERTEX,{"derivedFrom":[subQ8,sQuery(id+"F6.wireOp",EDGE,"E9.23.0")]}),-1.0]])],"derivedFrom":subQ8})])]})})],"blendedInto":[makeQuery(id+"F7.boolean.opBoolean","COPY",FACE,{"derivedFrom":makeQuery(id+"F7.opExtrude","SWEPT_FACE",FACE,{"disambiguationData":[OSD([subQ7,subQ6,subQ5,subQ4,subQ3,subQ2,subQ1,subQ0]),TDD([makeQuery(id+"F6.imprint","IMPRINT",EDGE,{"disambiguationData":[TD([[makeQuery(id+"F6.imprint","INTERSECT",VERTEX,{"derivedFrom":[subQ8,sQuery(id+"F6.wireOp",EDGE,"E9.23.0")]}),-1.0]])],"derivedFrom":subQ8})])]})})]});}
            var Q13;
            {var subQ0=sQuery(id+"F3.wireOp",EDGE,"E6.right");var subQ1=sQuery(id+"F3.wireOp",EDGE,"E6.top");var subQ2=sQuery(id+"F3.wireOp",EDGE,"E6.bottom");var subQ3=sQuery(id+"F3.wireOp",EDGE,"E5.right");var subQ4=sQuery(id+"F3.wireOp",EDGE,"E5.top");var subQ5=sQuery(id+"F3.wireOp",EDGE,"E5.bottom");var subQ6=sQuery(id+"F3.wireOp",EDGE,"E4");var subQ7=sQuery(id+"F3.wireOp",EDGE,"E3");var subQ8=makeQuery(id+"F5.opFillet","BLEND_EDGE",EDGE,{"blendedFrom":[makeQuery(id+"F4.opExtrude","CAP_EDGE",EDGE,{"disambiguationData":[OSD([subQ6])],"isStart":false}),makeQuery(id+"F4.opExtrude","CAP_FACE",FACE,{"disambiguationData":[OSD([subQ7,subQ6,subQ5,subQ4,subQ3,subQ2,subQ1,subQ0])],"isStart":false})],"blendedInto":[makeQuery(id+"F4.opExtrude","CAP_FACE",FACE,{"disambiguationData":[OSD([subQ7,subQ6,subQ5,subQ4,subQ3,subQ2,subQ1,subQ0])],"isStart":false})]});var subQ9=sQuery(id+"F6.wireOp",EDGE,"E9.26.0");Q13=makeQuery(id+"F9.opFillet","BLEND_EDGE",EDGE,{"blendedFrom":[makeQuery(id+"F7.boolean.opBoolean","COPY",EDGE,{"derivedFrom":makeQuery(id+"F7.opExtrude","CAP_EDGE",EDGE,{"disambiguationData":[OSD([subQ9])],"isStart":false})}),makeQuery(id+"F7.boolean.opBoolean","COPY",FACE,{"derivedFrom":makeQuery(id+"F7.opExtrude","SWEPT_FACE",FACE,{"disambiguationData":[OSD([subQ7,subQ6,subQ5,subQ4,subQ3,subQ2,subQ1,subQ0]),TDD([makeQuery(id+"F6.imprint","IMPRINT",EDGE,{"disambiguationData":[TD([[makeQuery(id+"F6.imprint","INTERSECT",VERTEX,{"derivedFrom":[subQ8,sQuery(id+"F6.wireOp",EDGE,"E9.25.0")]}),-1.0]])],"derivedFrom":subQ8})])]})})],"blendedInto":[makeQuery(id+"F7.boolean.opBoolean","COPY",FACE,{"derivedFrom":makeQuery(id+"F7.opExtrude","SWEPT_FACE",FACE,{"disambiguationData":[OSD([subQ7,subQ6,subQ5,subQ4,subQ3,subQ2,subQ1,subQ0]),TDD([makeQuery(id+"F6.imprint","IMPRINT",EDGE,{"disambiguationData":[TD([[makeQuery(id+"F6.imprint","INTERSECT",VERTEX,{"derivedFrom":[subQ8,sQuery(id+"F6.wireOp",EDGE,"E9.25.0")]}),-1.0]])],"derivedFrom":subQ8})])]})})]});}
            var Q14;
            {var subQ0=sQuery(id+"F3.wireOp",EDGE,"E6.right");var subQ1=sQuery(id+"F3.wireOp",EDGE,"E6.top");var subQ2=sQuery(id+"F3.wireOp",EDGE,"E6.bottom");var subQ3=sQuery(id+"F3.wireOp",EDGE,"E5.right");var subQ4=sQuery(id+"F3.wireOp",EDGE,"E5.top");var subQ5=sQuery(id+"F3.wireOp",EDGE,"E5.bottom");var subQ6=sQuery(id+"F3.wireOp",EDGE,"E4");var subQ7=sQuery(id+"F3.wireOp",EDGE,"E3");var subQ8=makeQuery(id+"F5.opFillet","BLEND_EDGE",EDGE,{"blendedFrom":[makeQuery(id+"F4.opExtrude","CAP_EDGE",EDGE,{"disambiguationData":[OSD([subQ6])],"isStart":false}),makeQuery(id+"F4.opExtrude","CAP_FACE",FACE,{"disambiguationData":[OSD([subQ7,subQ6,subQ5,subQ4,subQ3,subQ2,subQ1,subQ0])],"isStart":false})],"blendedInto":[makeQuery(id+"F4.opExtrude","CAP_FACE",FACE,{"disambiguationData":[OSD([subQ7,subQ6,subQ5,subQ4,subQ3,subQ2,subQ1,subQ0])],"isStart":false})]});var subQ9=sQuery(id+"F6.wireOp",EDGE,"E9.28.0");Q14=makeQuery(id+"F9.opFillet","BLEND_EDGE",EDGE,{"blendedFrom":[makeQuery(id+"F7.boolean.opBoolean","COPY",EDGE,{"derivedFrom":makeQuery(id+"F7.opExtrude","CAP_EDGE",EDGE,{"disambiguationData":[OSD([subQ9])],"isStart":false})}),makeQuery(id+"F7.boolean.opBoolean","COPY",FACE,{"derivedFrom":makeQuery(id+"F7.opExtrude","SWEPT_FACE",FACE,{"disambiguationData":[OSD([subQ7,subQ6,subQ5,subQ4,subQ3,subQ2,subQ1,subQ0]),TDD([makeQuery(id+"F6.imprint","IMPRINT",EDGE,{"disambiguationData":[TD([[makeQuery(id+"F6.imprint","INTERSECT",VERTEX,{"derivedFrom":[subQ8,sQuery(id+"F6.wireOp",EDGE,"E9.27.0")]}),-1.0]])],"derivedFrom":subQ8})])]})})],"blendedInto":[makeQuery(id+"F7.boolean.opBoolean","COPY",FACE,{"derivedFrom":makeQuery(id+"F7.opExtrude","SWEPT_FACE",FACE,{"disambiguationData":[OSD([subQ7,subQ6,subQ5,subQ4,subQ3,subQ2,subQ1,subQ0]),TDD([makeQuery(id+"F6.imprint","IMPRINT",EDGE,{"disambiguationData":[TD([[makeQuery(id+"F6.imprint","INTERSECT",VERTEX,{"derivedFrom":[subQ8,sQuery(id+"F6.wireOp",EDGE,"E9.27.0")]}),-1.0]])],"derivedFrom":subQ8})])]})})]});}
            var Q15;
            {var subQ0=sQuery(id+"F3.wireOp",EDGE,"E6.right");var subQ1=sQuery(id+"F3.wireOp",EDGE,"E6.top");var subQ2=sQuery(id+"F3.wireOp",EDGE,"E6.bottom");var subQ3=sQuery(id+"F3.wireOp",EDGE,"E5.right");var subQ4=sQuery(id+"F3.wireOp",EDGE,"E5.top");var subQ5=sQuery(id+"F3.wireOp",EDGE,"E5.bottom");var subQ6=sQuery(id+"F3.wireOp",EDGE,"E4");var subQ7=sQuery(id+"F3.wireOp",EDGE,"E3");var subQ8=makeQuery(id+"F5.opFillet","BLEND_EDGE",EDGE,{"blendedFrom":[makeQuery(id+"F4.opExtrude","CAP_EDGE",EDGE,{"disambiguationData":[OSD([subQ6])],"isStart":false}),makeQuery(id+"F4.opExtrude","CAP_FACE",FACE,{"disambiguationData":[OSD([subQ7,subQ6,subQ5,subQ4,subQ3,subQ2,subQ1,subQ0])],"isStart":false})],"blendedInto":[makeQuery(id+"F4.opExtrude","CAP_FACE",FACE,{"disambiguationData":[OSD([subQ7,subQ6,subQ5,subQ4,subQ3,subQ2,subQ1,subQ0])],"isStart":false})]});var subQ9=sQuery(id+"F6.wireOp",EDGE,"E9.30.0");Q15=makeQuery(id+"F9.opFillet","BLEND_EDGE",EDGE,{"blendedFrom":[makeQuery(id+"F7.boolean.opBoolean","COPY",EDGE,{"derivedFrom":makeQuery(id+"F7.opExtrude","CAP_EDGE",EDGE,{"disambiguationData":[OSD([subQ9])],"isStart":false})}),makeQuery(id+"F7.boolean.opBoolean","COPY",FACE,{"derivedFrom":makeQuery(id+"F7.opExtrude","SWEPT_FACE",FACE,{"disambiguationData":[OSD([subQ7,subQ6,subQ5,subQ4,subQ3,subQ2,subQ1,subQ0]),TDD([makeQuery(id+"F6.imprint","IMPRINT",EDGE,{"disambiguationData":[TD([[makeQuery(id+"F6.imprint","INTERSECT",VERTEX,{"derivedFrom":[subQ8,sQuery(id+"F6.wireOp",EDGE,"E9.29.0")]}),-1.0]])],"derivedFrom":subQ8})])]})})],"blendedInto":[makeQuery(id+"F7.boolean.opBoolean","COPY",FACE,{"derivedFrom":makeQuery(id+"F7.opExtrude","SWEPT_FACE",FACE,{"disambiguationData":[OSD([subQ7,subQ6,subQ5,subQ4,subQ3,subQ2,subQ1,subQ0]),TDD([makeQuery(id+"F6.imprint","IMPRINT",EDGE,{"disambiguationData":[TD([[makeQuery(id+"F6.imprint","INTERSECT",VERTEX,{"derivedFrom":[subQ8,sQuery(id+"F6.wireOp",EDGE,"E9.29.0")]}),-1.0]])],"derivedFrom":subQ8})])]})})]});}
            var Q16;
            {var subQ0=sQuery(id+"F3.wireOp",EDGE,"E6.right");var subQ1=sQuery(id+"F3.wireOp",EDGE,"E6.top");var subQ2=sQuery(id+"F3.wireOp",EDGE,"E6.bottom");var subQ3=sQuery(id+"F3.wireOp",EDGE,"E5.right");var subQ4=sQuery(id+"F3.wireOp",EDGE,"E5.top");var subQ5=sQuery(id+"F3.wireOp",EDGE,"E5.bottom");var subQ6=sQuery(id+"F3.wireOp",EDGE,"E4");var subQ7=sQuery(id+"F3.wireOp",EDGE,"E3");var subQ8=makeQuery(id+"F5.opFillet","BLEND_EDGE",EDGE,{"blendedFrom":[makeQuery(id+"F4.opExtrude","CAP_EDGE",EDGE,{"disambiguationData":[OSD([subQ6])],"isStart":false}),makeQuery(id+"F4.opExtrude","CAP_FACE",FACE,{"disambiguationData":[OSD([subQ7,subQ6,subQ5,subQ4,subQ3,subQ2,subQ1,subQ0])],"isStart":false})],"blendedInto":[makeQuery(id+"F4.opExtrude","CAP_FACE",FACE,{"disambiguationData":[OSD([subQ7,subQ6,subQ5,subQ4,subQ3,subQ2,subQ1,subQ0])],"isStart":false})]});var subQ9=sQuery(id+"F6.wireOp",EDGE,"E9.32.0");Q16=makeQuery(id+"F9.opFillet","BLEND_EDGE",EDGE,{"blendedFrom":[makeQuery(id+"F7.boolean.opBoolean","COPY",EDGE,{"derivedFrom":makeQuery(id+"F7.opExtrude","CAP_EDGE",EDGE,{"disambiguationData":[OSD([subQ9])],"isStart":false})}),makeQuery(id+"F7.boolean.opBoolean","COPY",FACE,{"derivedFrom":makeQuery(id+"F7.opExtrude","SWEPT_FACE",FACE,{"disambiguationData":[OSD([subQ7,subQ6,subQ5,subQ4,subQ3,subQ2,subQ1,subQ0]),TDD([makeQuery(id+"F6.imprint","IMPRINT",EDGE,{"disambiguationData":[TD([[makeQuery(id+"F6.imprint","INTERSECT",VERTEX,{"derivedFrom":[subQ8,sQuery(id+"F6.wireOp",EDGE,"E9.31.0")]}),-1.0]])],"derivedFrom":subQ8})])]})})],"blendedInto":[makeQuery(id+"F7.boolean.opBoolean","COPY",FACE,{"derivedFrom":makeQuery(id+"F7.opExtrude","SWEPT_FACE",FACE,{"disambiguationData":[OSD([subQ7,subQ6,subQ5,subQ4,subQ3,subQ2,subQ1,subQ0]),TDD([makeQuery(id+"F6.imprint","IMPRINT",EDGE,{"disambiguationData":[TD([[makeQuery(id+"F6.imprint","INTERSECT",VERTEX,{"derivedFrom":[subQ8,sQuery(id+"F6.wireOp",EDGE,"E9.31.0")]}),-1.0]])],"derivedFrom":subQ8})])]})})]});}
            var Q17;
            {var subQ0=sQuery(id+"F3.wireOp",EDGE,"E6.right");var subQ1=sQuery(id+"F3.wireOp",EDGE,"E6.top");var subQ2=sQuery(id+"F3.wireOp",EDGE,"E6.bottom");var subQ3=sQuery(id+"F3.wireOp",EDGE,"E5.right");var subQ4=sQuery(id+"F3.wireOp",EDGE,"E5.top");var subQ5=sQuery(id+"F3.wireOp",EDGE,"E5.bottom");var subQ6=sQuery(id+"F3.wireOp",EDGE,"E4");var subQ7=sQuery(id+"F3.wireOp",EDGE,"E3");var subQ8=makeQuery(id+"F5.opFillet","BLEND_EDGE",EDGE,{"blendedFrom":[makeQuery(id+"F4.opExtrude","CAP_EDGE",EDGE,{"disambiguationData":[OSD([subQ6])],"isStart":false}),makeQuery(id+"F4.opExtrude","CAP_FACE",FACE,{"disambiguationData":[OSD([subQ7,subQ6,subQ5,subQ4,subQ3,subQ2,subQ1,subQ0])],"isStart":false})],"blendedInto":[makeQuery(id+"F4.opExtrude","CAP_FACE",FACE,{"disambiguationData":[OSD([subQ7,subQ6,subQ5,subQ4,subQ3,subQ2,subQ1,subQ0])],"isStart":false})]});var subQ9=sQuery(id+"F6.wireOp",EDGE,"E9.34.0");Q17=makeQuery(id+"F9.opFillet","BLEND_EDGE",EDGE,{"blendedFrom":[makeQuery(id+"F7.boolean.opBoolean","COPY",EDGE,{"derivedFrom":makeQuery(id+"F7.opExtrude","CAP_EDGE",EDGE,{"disambiguationData":[OSD([subQ9])],"isStart":false})}),makeQuery(id+"F7.boolean.opBoolean","COPY",FACE,{"derivedFrom":makeQuery(id+"F7.opExtrude","SWEPT_FACE",FACE,{"disambiguationData":[OSD([subQ7,subQ6,subQ5,subQ4,subQ3,subQ2,subQ1,subQ0]),TDD([makeQuery(id+"F6.imprint","IMPRINT",EDGE,{"disambiguationData":[TD([[makeQuery(id+"F6.imprint","INTERSECT",VERTEX,{"derivedFrom":[subQ8,sQuery(id+"F6.wireOp",EDGE,"E9.33.0")]}),-1.0]])],"derivedFrom":subQ8})])]})})],"blendedInto":[makeQuery(id+"F7.boolean.opBoolean","COPY",FACE,{"derivedFrom":makeQuery(id+"F7.opExtrude","SWEPT_FACE",FACE,{"disambiguationData":[OSD([subQ7,subQ6,subQ5,subQ4,subQ3,subQ2,subQ1,subQ0]),TDD([makeQuery(id+"F6.imprint","IMPRINT",EDGE,{"disambiguationData":[TD([[makeQuery(id+"F6.imprint","INTERSECT",VERTEX,{"derivedFrom":[subQ8,sQuery(id+"F6.wireOp",EDGE,"E9.33.0")]}),-1.0]])],"derivedFrom":subQ8})])]})})]});}
            var Q18;
            {var subQ0=sQuery(id+"F3.wireOp",EDGE,"E6.right");var subQ1=sQuery(id+"F3.wireOp",EDGE,"E6.top");var subQ2=sQuery(id+"F3.wireOp",EDGE,"E6.bottom");var subQ3=sQuery(id+"F3.wireOp",EDGE,"E5.right");var subQ4=sQuery(id+"F3.wireOp",EDGE,"E5.top");var subQ5=sQuery(id+"F3.wireOp",EDGE,"E5.bottom");var subQ6=sQuery(id+"F3.wireOp",EDGE,"E4");var subQ7=sQuery(id+"F3.wireOp",EDGE,"E3");var subQ8=makeQuery(id+"F5.opFillet","BLEND_EDGE",EDGE,{"blendedFrom":[makeQuery(id+"F4.opExtrude","CAP_EDGE",EDGE,{"disambiguationData":[OSD([subQ6])],"isStart":false}),makeQuery(id+"F4.opExtrude","CAP_FACE",FACE,{"disambiguationData":[OSD([subQ7,subQ6,subQ5,subQ4,subQ3,subQ2,subQ1,subQ0])],"isStart":false})],"blendedInto":[makeQuery(id+"F4.opExtrude","CAP_FACE",FACE,{"disambiguationData":[OSD([subQ7,subQ6,subQ5,subQ4,subQ3,subQ2,subQ1,subQ0])],"isStart":false})]});var subQ9=sQuery(id+"F6.wireOp",EDGE,"E9.36.0");Q18=makeQuery(id+"F9.opFillet","BLEND_EDGE",EDGE,{"blendedFrom":[makeQuery(id+"F7.boolean.opBoolean","COPY",EDGE,{"derivedFrom":makeQuery(id+"F7.opExtrude","CAP_EDGE",EDGE,{"disambiguationData":[OSD([subQ9])],"isStart":false})}),makeQuery(id+"F7.boolean.opBoolean","COPY",FACE,{"derivedFrom":makeQuery(id+"F7.opExtrude","SWEPT_FACE",FACE,{"disambiguationData":[OSD([subQ7,subQ6,subQ5,subQ4,subQ3,subQ2,subQ1,subQ0]),TDD([makeQuery(id+"F6.imprint","IMPRINT",EDGE,{"disambiguationData":[TD([[makeQuery(id+"F6.imprint","INTERSECT",VERTEX,{"derivedFrom":[subQ8,sQuery(id+"F6.wireOp",EDGE,"E9.35.0")]}),-1.0]])],"derivedFrom":subQ8})])]})})],"blendedInto":[makeQuery(id+"F7.boolean.opBoolean","COPY",FACE,{"derivedFrom":makeQuery(id+"F7.opExtrude","SWEPT_FACE",FACE,{"disambiguationData":[OSD([subQ7,subQ6,subQ5,subQ4,subQ3,subQ2,subQ1,subQ0]),TDD([makeQuery(id+"F6.imprint","IMPRINT",EDGE,{"disambiguationData":[TD([[makeQuery(id+"F6.imprint","INTERSECT",VERTEX,{"derivedFrom":[subQ8,sQuery(id+"F6.wireOp",EDGE,"E9.35.0")]}),-1.0]])],"derivedFrom":subQ8})])]})})]});}
            var Q19;
            {var subQ0=sQuery(id+"F3.wireOp",EDGE,"E6.right");var subQ1=sQuery(id+"F3.wireOp",EDGE,"E6.top");var subQ2=sQuery(id+"F3.wireOp",EDGE,"E6.bottom");var subQ3=sQuery(id+"F3.wireOp",EDGE,"E5.right");var subQ4=sQuery(id+"F3.wireOp",EDGE,"E5.top");var subQ5=sQuery(id+"F3.wireOp",EDGE,"E5.bottom");var subQ6=sQuery(id+"F3.wireOp",EDGE,"E4");var subQ7=sQuery(id+"F3.wireOp",EDGE,"E3");var subQ8=makeQuery(id+"F5.opFillet","BLEND_EDGE",EDGE,{"blendedFrom":[makeQuery(id+"F4.opExtrude","CAP_EDGE",EDGE,{"disambiguationData":[OSD([subQ6])],"isStart":false}),makeQuery(id+"F4.opExtrude","CAP_FACE",FACE,{"disambiguationData":[OSD([subQ7,subQ6,subQ5,subQ4,subQ3,subQ2,subQ1,subQ0])],"isStart":false})],"blendedInto":[makeQuery(id+"F4.opExtrude","CAP_FACE",FACE,{"disambiguationData":[OSD([subQ7,subQ6,subQ5,subQ4,subQ3,subQ2,subQ1,subQ0])],"isStart":false})]});var subQ9=sQuery(id+"F6.wireOp",EDGE,"E9.38.0");Q19=makeQuery(id+"F9.opFillet","BLEND_EDGE",EDGE,{"blendedFrom":[makeQuery(id+"F7.boolean.opBoolean","COPY",EDGE,{"derivedFrom":makeQuery(id+"F7.opExtrude","CAP_EDGE",EDGE,{"disambiguationData":[OSD([subQ9])],"isStart":false})}),makeQuery(id+"F7.boolean.opBoolean","COPY",FACE,{"derivedFrom":makeQuery(id+"F7.opExtrude","SWEPT_FACE",FACE,{"disambiguationData":[OSD([subQ7,subQ6,subQ5,subQ4,subQ3,subQ2,subQ1,subQ0]),TDD([makeQuery(id+"F6.imprint","IMPRINT",EDGE,{"disambiguationData":[TD([[makeQuery(id+"F6.imprint","INTERSECT",VERTEX,{"derivedFrom":[subQ8,sQuery(id+"F6.wireOp",EDGE,"E9.37.0")]}),-1.0]])],"derivedFrom":subQ8})])]})})],"blendedInto":[makeQuery(id+"F7.boolean.opBoolean","COPY",FACE,{"derivedFrom":makeQuery(id+"F7.opExtrude","SWEPT_FACE",FACE,{"disambiguationData":[OSD([subQ7,subQ6,subQ5,subQ4,subQ3,subQ2,subQ1,subQ0]),TDD([makeQuery(id+"F6.imprint","IMPRINT",EDGE,{"disambiguationData":[TD([[makeQuery(id+"F6.imprint","INTERSECT",VERTEX,{"derivedFrom":[subQ8,sQuery(id+"F6.wireOp",EDGE,"E9.37.0")]}),-1.0]])],"derivedFrom":subQ8})])]})})]});}
            var Q20;
            {var subQ0=sQuery(id+"F3.wireOp",EDGE,"E6.right");var subQ1=sQuery(id+"F3.wireOp",EDGE,"E6.top");var subQ2=sQuery(id+"F3.wireOp",EDGE,"E6.bottom");var subQ3=sQuery(id+"F3.wireOp",EDGE,"E5.right");var subQ4=sQuery(id+"F3.wireOp",EDGE,"E5.top");var subQ5=sQuery(id+"F3.wireOp",EDGE,"E5.bottom");var subQ6=sQuery(id+"F3.wireOp",EDGE,"E4");var subQ7=sQuery(id+"F3.wireOp",EDGE,"E3");var subQ8=makeQuery(id+"F5.opFillet","BLEND_EDGE",EDGE,{"blendedFrom":[makeQuery(id+"F4.opExtrude","CAP_EDGE",EDGE,{"disambiguationData":[OSD([subQ6])],"isStart":false}),makeQuery(id+"F4.opExtrude","CAP_FACE",FACE,{"disambiguationData":[OSD([subQ7,subQ6,subQ5,subQ4,subQ3,subQ2,subQ1,subQ0])],"isStart":false})],"blendedInto":[makeQuery(id+"F4.opExtrude","CAP_FACE",FACE,{"disambiguationData":[OSD([subQ7,subQ6,subQ5,subQ4,subQ3,subQ2,subQ1,subQ0])],"isStart":false})]});var subQ9=sQuery(id+"F6.wireOp",EDGE,"E9.40.0");Q20=makeQuery(id+"F9.opFillet","BLEND_EDGE",EDGE,{"blendedFrom":[makeQuery(id+"F7.boolean.opBoolean","COPY",EDGE,{"derivedFrom":makeQuery(id+"F7.opExtrude","CAP_EDGE",EDGE,{"disambiguationData":[OSD([subQ9])],"isStart":false})}),makeQuery(id+"F7.boolean.opBoolean","COPY",FACE,{"derivedFrom":makeQuery(id+"F7.opExtrude","SWEPT_FACE",FACE,{"disambiguationData":[OSD([subQ7,subQ6,subQ5,subQ4,subQ3,subQ2,subQ1,subQ0]),TDD([makeQuery(id+"F6.imprint","IMPRINT",EDGE,{"disambiguationData":[TD([[makeQuery(id+"F6.imprint","INTERSECT",VERTEX,{"derivedFrom":[subQ8,sQuery(id+"F6.wireOp",EDGE,"E9.39.0")]}),-1.0]])],"derivedFrom":subQ8})])]})})],"blendedInto":[makeQuery(id+"F7.boolean.opBoolean","COPY",FACE,{"derivedFrom":makeQuery(id+"F7.opExtrude","SWEPT_FACE",FACE,{"disambiguationData":[OSD([subQ7,subQ6,subQ5,subQ4,subQ3,subQ2,subQ1,subQ0]),TDD([makeQuery(id+"F6.imprint","IMPRINT",EDGE,{"disambiguationData":[TD([[makeQuery(id+"F6.imprint","INTERSECT",VERTEX,{"derivedFrom":[subQ8,sQuery(id+"F6.wireOp",EDGE,"E9.39.0")]}),-1.0]])],"derivedFrom":subQ8})])]})})]});}
            var Q21;
            {var subQ0=sQuery(id+"F3.wireOp",EDGE,"E6.right");var subQ1=sQuery(id+"F3.wireOp",EDGE,"E6.top");var subQ2=sQuery(id+"F3.wireOp",EDGE,"E6.bottom");var subQ3=sQuery(id+"F3.wireOp",EDGE,"E5.right");var subQ4=sQuery(id+"F3.wireOp",EDGE,"E5.top");var subQ5=sQuery(id+"F3.wireOp",EDGE,"E5.bottom");var subQ6=sQuery(id+"F3.wireOp",EDGE,"E4");var subQ7=sQuery(id+"F3.wireOp",EDGE,"E3");var subQ8=makeQuery(id+"F5.opFillet","BLEND_EDGE",EDGE,{"blendedFrom":[makeQuery(id+"F4.opExtrude","CAP_EDGE",EDGE,{"disambiguationData":[OSD([subQ6])],"isStart":false}),makeQuery(id+"F4.opExtrude","CAP_FACE",FACE,{"disambiguationData":[OSD([subQ7,subQ6,subQ5,subQ4,subQ3,subQ2,subQ1,subQ0])],"isStart":false})],"blendedInto":[makeQuery(id+"F4.opExtrude","CAP_FACE",FACE,{"disambiguationData":[OSD([subQ7,subQ6,subQ5,subQ4,subQ3,subQ2,subQ1,subQ0])],"isStart":false})]});var subQ9=sQuery(id+"F6.wireOp",EDGE,"E9.42.0");Q21=makeQuery(id+"F9.opFillet","BLEND_EDGE",EDGE,{"blendedFrom":[makeQuery(id+"F7.boolean.opBoolean","COPY",EDGE,{"derivedFrom":makeQuery(id+"F7.opExtrude","CAP_EDGE",EDGE,{"disambiguationData":[OSD([subQ9])],"isStart":false})}),makeQuery(id+"F7.boolean.opBoolean","COPY",FACE,{"derivedFrom":makeQuery(id+"F7.opExtrude","SWEPT_FACE",FACE,{"disambiguationData":[OSD([subQ7,subQ6,subQ5,subQ4,subQ3,subQ2,subQ1,subQ0]),TDD([makeQuery(id+"F6.imprint","IMPRINT",EDGE,{"disambiguationData":[TD([[makeQuery(id+"F6.imprint","INTERSECT",VERTEX,{"derivedFrom":[subQ8,sQuery(id+"F6.wireOp",EDGE,"E9.41.0")]}),-1.0]])],"derivedFrom":subQ8})])]})})],"blendedInto":[makeQuery(id+"F7.boolean.opBoolean","COPY",FACE,{"derivedFrom":makeQuery(id+"F7.opExtrude","SWEPT_FACE",FACE,{"disambiguationData":[OSD([subQ7,subQ6,subQ5,subQ4,subQ3,subQ2,subQ1,subQ0]),TDD([makeQuery(id+"F6.imprint","IMPRINT",EDGE,{"disambiguationData":[TD([[makeQuery(id+"F6.imprint","INTERSECT",VERTEX,{"derivedFrom":[subQ8,sQuery(id+"F6.wireOp",EDGE,"E9.41.0")]}),-1.0]])],"derivedFrom":subQ8})])]})})]});}
            var Q22;
            {var subQ0=sQuery(id+"F3.wireOp",EDGE,"E6.right");var subQ1=sQuery(id+"F3.wireOp",EDGE,"E6.top");var subQ2=sQuery(id+"F3.wireOp",EDGE,"E6.bottom");var subQ3=sQuery(id+"F3.wireOp",EDGE,"E5.right");var subQ4=sQuery(id+"F3.wireOp",EDGE,"E5.top");var subQ5=sQuery(id+"F3.wireOp",EDGE,"E5.bottom");var subQ6=sQuery(id+"F3.wireOp",EDGE,"E4");var subQ7=sQuery(id+"F3.wireOp",EDGE,"E3");var subQ8=makeQuery(id+"F5.opFillet","BLEND_EDGE",EDGE,{"blendedFrom":[makeQuery(id+"F4.opExtrude","CAP_EDGE",EDGE,{"disambiguationData":[OSD([subQ6])],"isStart":false}),makeQuery(id+"F4.opExtrude","CAP_FACE",FACE,{"disambiguationData":[OSD([subQ7,subQ6,subQ5,subQ4,subQ3,subQ2,subQ1,subQ0])],"isStart":false})],"blendedInto":[makeQuery(id+"F4.opExtrude","CAP_FACE",FACE,{"disambiguationData":[OSD([subQ7,subQ6,subQ5,subQ4,subQ3,subQ2,subQ1,subQ0])],"isStart":false})]});var subQ9=sQuery(id+"F6.wireOp",EDGE,"E9.44.0");Q22=makeQuery(id+"F9.opFillet","BLEND_EDGE",EDGE,{"blendedFrom":[makeQuery(id+"F7.boolean.opBoolean","COPY",EDGE,{"derivedFrom":makeQuery(id+"F7.opExtrude","CAP_EDGE",EDGE,{"disambiguationData":[OSD([subQ9])],"isStart":false})}),makeQuery(id+"F7.boolean.opBoolean","COPY",FACE,{"derivedFrom":makeQuery(id+"F7.opExtrude","SWEPT_FACE",FACE,{"disambiguationData":[OSD([subQ7,subQ6,subQ5,subQ4,subQ3,subQ2,subQ1,subQ0]),TDD([makeQuery(id+"F6.imprint","IMPRINT",EDGE,{"disambiguationData":[TD([[makeQuery(id+"F6.imprint","INTERSECT",VERTEX,{"derivedFrom":[subQ8,sQuery(id+"F6.wireOp",EDGE,"E9.43.0")]}),-1.0]])],"derivedFrom":subQ8})])]})})],"blendedInto":[makeQuery(id+"F7.boolean.opBoolean","COPY",FACE,{"derivedFrom":makeQuery(id+"F7.opExtrude","SWEPT_FACE",FACE,{"disambiguationData":[OSD([subQ7,subQ6,subQ5,subQ4,subQ3,subQ2,subQ1,subQ0]),TDD([makeQuery(id+"F6.imprint","IMPRINT",EDGE,{"disambiguationData":[TD([[makeQuery(id+"F6.imprint","INTERSECT",VERTEX,{"derivedFrom":[subQ8,sQuery(id+"F6.wireOp",EDGE,"E9.43.0")]}),-1.0]])],"derivedFrom":subQ8})])]})})]});}
            var Q23;
            {var subQ0=sQuery(id+"F3.wireOp",EDGE,"E6.right");var subQ1=sQuery(id+"F3.wireOp",EDGE,"E6.top");var subQ2=sQuery(id+"F3.wireOp",EDGE,"E6.bottom");var subQ3=sQuery(id+"F3.wireOp",EDGE,"E5.right");var subQ4=sQuery(id+"F3.wireOp",EDGE,"E5.top");var subQ5=sQuery(id+"F3.wireOp",EDGE,"E5.bottom");var subQ6=sQuery(id+"F3.wireOp",EDGE,"E4");var subQ7=sQuery(id+"F3.wireOp",EDGE,"E3");var subQ8=makeQuery(id+"F5.opFillet","BLEND_EDGE",EDGE,{"blendedFrom":[makeQuery(id+"F4.opExtrude","CAP_EDGE",EDGE,{"disambiguationData":[OSD([subQ6])],"isStart":false}),makeQuery(id+"F4.opExtrude","CAP_FACE",FACE,{"disambiguationData":[OSD([subQ7,subQ6,subQ5,subQ4,subQ3,subQ2,subQ1,subQ0])],"isStart":false})],"blendedInto":[makeQuery(id+"F4.opExtrude","CAP_FACE",FACE,{"disambiguationData":[OSD([subQ7,subQ6,subQ5,subQ4,subQ3,subQ2,subQ1,subQ0])],"isStart":false})]});var subQ9=sQuery(id+"F6.wireOp",EDGE,"E9.46.0");Q23=makeQuery(id+"F9.opFillet","BLEND_EDGE",EDGE,{"blendedFrom":[makeQuery(id+"F7.boolean.opBoolean","COPY",EDGE,{"derivedFrom":makeQuery(id+"F7.opExtrude","CAP_EDGE",EDGE,{"disambiguationData":[OSD([subQ9])],"isStart":false})}),makeQuery(id+"F7.boolean.opBoolean","COPY",FACE,{"derivedFrom":makeQuery(id+"F7.opExtrude","SWEPT_FACE",FACE,{"disambiguationData":[OSD([subQ7,subQ6,subQ5,subQ4,subQ3,subQ2,subQ1,subQ0]),TDD([makeQuery(id+"F6.imprint","IMPRINT",EDGE,{"disambiguationData":[TD([[makeQuery(id+"F6.imprint","INTERSECT",VERTEX,{"derivedFrom":[subQ8,sQuery(id+"F6.wireOp",EDGE,"E9.45.0")]}),-1.0]])],"derivedFrom":subQ8})])]})})],"blendedInto":[makeQuery(id+"F7.boolean.opBoolean","COPY",FACE,{"derivedFrom":makeQuery(id+"F7.opExtrude","SWEPT_FACE",FACE,{"disambiguationData":[OSD([subQ7,subQ6,subQ5,subQ4,subQ3,subQ2,subQ1,subQ0]),TDD([makeQuery(id+"F6.imprint","IMPRINT",EDGE,{"disambiguationData":[TD([[makeQuery(id+"F6.imprint","INTERSECT",VERTEX,{"derivedFrom":[subQ8,sQuery(id+"F6.wireOp",EDGE,"E9.45.0")]}),-1.0]])],"derivedFrom":subQ8})])]})})]});}
            var Q24;
            {var subQ0=sQuery(id+"F3.wireOp",EDGE,"E6.right");var subQ1=sQuery(id+"F3.wireOp",EDGE,"E6.top");var subQ2=sQuery(id+"F3.wireOp",EDGE,"E6.bottom");var subQ3=sQuery(id+"F3.wireOp",EDGE,"E5.right");var subQ4=sQuery(id+"F3.wireOp",EDGE,"E5.top");var subQ5=sQuery(id+"F3.wireOp",EDGE,"E5.bottom");var subQ6=sQuery(id+"F3.wireOp",EDGE,"E4");var subQ7=sQuery(id+"F3.wireOp",EDGE,"E3");var subQ8=makeQuery(id+"F5.opFillet","BLEND_EDGE",EDGE,{"blendedFrom":[makeQuery(id+"F4.opExtrude","CAP_EDGE",EDGE,{"disambiguationData":[OSD([subQ6])],"isStart":false}),makeQuery(id+"F4.opExtrude","CAP_FACE",FACE,{"disambiguationData":[OSD([subQ7,subQ6,subQ5,subQ4,subQ3,subQ2,subQ1,subQ0])],"isStart":false})],"blendedInto":[makeQuery(id+"F4.opExtrude","CAP_FACE",FACE,{"disambiguationData":[OSD([subQ7,subQ6,subQ5,subQ4,subQ3,subQ2,subQ1,subQ0])],"isStart":false})]});var subQ9=sQuery(id+"F6.wireOp",EDGE,"E9.48.0");Q24=makeQuery(id+"F9.opFillet","BLEND_EDGE",EDGE,{"blendedFrom":[makeQuery(id+"F7.boolean.opBoolean","COPY",EDGE,{"derivedFrom":makeQuery(id+"F7.opExtrude","CAP_EDGE",EDGE,{"disambiguationData":[OSD([subQ9])],"isStart":false})}),makeQuery(id+"F7.boolean.opBoolean","COPY",FACE,{"derivedFrom":makeQuery(id+"F7.opExtrude","SWEPT_FACE",FACE,{"disambiguationData":[OSD([subQ7,subQ6,subQ5,subQ4,subQ3,subQ2,subQ1,subQ0]),TDD([makeQuery(id+"F6.imprint","IMPRINT",EDGE,{"disambiguationData":[TD([[makeQuery(id+"F6.imprint","INTERSECT",VERTEX,{"derivedFrom":[subQ8,sQuery(id+"F6.wireOp",EDGE,"E9.47.0")]}),-1.0]])],"derivedFrom":subQ8})])]})})],"blendedInto":[makeQuery(id+"F7.boolean.opBoolean","COPY",FACE,{"derivedFrom":makeQuery(id+"F7.opExtrude","SWEPT_FACE",FACE,{"disambiguationData":[OSD([subQ7,subQ6,subQ5,subQ4,subQ3,subQ2,subQ1,subQ0]),TDD([makeQuery(id+"F6.imprint","IMPRINT",EDGE,{"disambiguationData":[TD([[makeQuery(id+"F6.imprint","INTERSECT",VERTEX,{"derivedFrom":[subQ8,sQuery(id+"F6.wireOp",EDGE,"E9.47.0")]}),-1.0]])],"derivedFrom":subQ8})])]})})]});}
            var Q25;
            {var subQ0=sQuery(id+"F3.wireOp",EDGE,"E6.right");var subQ1=sQuery(id+"F3.wireOp",EDGE,"E6.top");var subQ2=sQuery(id+"F3.wireOp",EDGE,"E6.bottom");var subQ3=sQuery(id+"F3.wireOp",EDGE,"E5.right");var subQ4=sQuery(id+"F3.wireOp",EDGE,"E5.top");var subQ5=sQuery(id+"F3.wireOp",EDGE,"E5.bottom");var subQ6=sQuery(id+"F3.wireOp",EDGE,"E4");var subQ7=sQuery(id+"F3.wireOp",EDGE,"E3");var subQ8=makeQuery(id+"F5.opFillet","BLEND_EDGE",EDGE,{"blendedFrom":[makeQuery(id+"F4.opExtrude","CAP_EDGE",EDGE,{"disambiguationData":[OSD([subQ6])],"isStart":false}),makeQuery(id+"F4.opExtrude","CAP_FACE",FACE,{"disambiguationData":[OSD([subQ7,subQ6,subQ5,subQ4,subQ3,subQ2,subQ1,subQ0])],"isStart":false})],"blendedInto":[makeQuery(id+"F4.opExtrude","CAP_FACE",FACE,{"disambiguationData":[OSD([subQ7,subQ6,subQ5,subQ4,subQ3,subQ2,subQ1,subQ0])],"isStart":false})]});var subQ9=sQuery(id+"F6.wireOp",EDGE,"E9.50.0");Q25=makeQuery(id+"F9.opFillet","BLEND_EDGE",EDGE,{"blendedFrom":[makeQuery(id+"F7.boolean.opBoolean","COPY",EDGE,{"derivedFrom":makeQuery(id+"F7.opExtrude","CAP_EDGE",EDGE,{"disambiguationData":[OSD([subQ9])],"isStart":false})}),makeQuery(id+"F7.boolean.opBoolean","COPY",FACE,{"derivedFrom":makeQuery(id+"F7.opExtrude","SWEPT_FACE",FACE,{"disambiguationData":[OSD([subQ7,subQ6,subQ5,subQ4,subQ3,subQ2,subQ1,subQ0]),TDD([makeQuery(id+"F6.imprint","IMPRINT",EDGE,{"disambiguationData":[TD([[makeQuery(id+"F6.imprint","INTERSECT",VERTEX,{"derivedFrom":[subQ8,sQuery(id+"F6.wireOp",EDGE,"E9.49.0")]}),-1.0]])],"derivedFrom":subQ8})])]})})],"blendedInto":[makeQuery(id+"F7.boolean.opBoolean","COPY",FACE,{"derivedFrom":makeQuery(id+"F7.opExtrude","SWEPT_FACE",FACE,{"disambiguationData":[OSD([subQ7,subQ6,subQ5,subQ4,subQ3,subQ2,subQ1,subQ0]),TDD([makeQuery(id+"F6.imprint","IMPRINT",EDGE,{"disambiguationData":[TD([[makeQuery(id+"F6.imprint","INTERSECT",VERTEX,{"derivedFrom":[subQ8,sQuery(id+"F6.wireOp",EDGE,"E9.49.0")]}),-1.0]])],"derivedFrom":subQ8})])]})})]});}
            fillet(context, id + "F11", {"entities" : qUnion([Q0, Q1, Q2, Q3, Q4, Q5, Q6, Q7, Q8, Q9, Q10, Q11, Q12, Q13, Q14, Q15, Q16, Q17, Q18, Q19, Q20, Q21, Q22, Q23, Q24, Q25]), "radius" : 1 * mm, "tangentPropagation" : true, "allowEdgeOverflow" : false});
        }
        {
            var Q0;
            Q0=makeQuery(id+"F4.opExtrude","CAP_FACE",FACE,{"disambiguationData":[OSD([sQuery(id+"F3.wireOp",EDGE,"E3"),sQuery(id+"F3.wireOp",EDGE,"E4"),sQuery(id+"F3.wireOp",EDGE,"E5.bottom"),sQuery(id+"F3.wireOp",EDGE,"E5.top"),sQuery(id+"F3.wireOp",EDGE,"E5.right"),sQuery(id+"F3.wireOp",EDGE,"E6.bottom"),sQuery(id+"F3.wireOp",EDGE,"E6.top"),sQuery(id+"F3.wireOp",EDGE,"E6.right")])],"isStart":true});
            var sketch = newSketch(context, id + "F12", { "sketchPlane" : qUnion([Q0])});
            skLineSegment(sketch, "E10", {"start": v(95.78, 0) * mm, "end": v(85.78, 0) * mm});
            skLineSegment(sketch, "E11", {"start": v(85.78, 0) * mm, "end": v(85.78, 70) * mm});
            skLineSegment(sketch, "E12.bottom", {"start": v(85.78, 70) * mm, "end": v(165.78, 70) * mm});
            skLineSegment(sketch, "E12.top", {"start": v(85.78, 0) * mm, "end": v(165.78, 0) * mm});
            skLineSegment(sketch, "E12.left", {"start": v(85.78, 70) * mm, "end": v(85.78, 0) * mm});
            skLineSegment(sketch, "E12.right", {"start": v(165.78, 70) * mm, "end": v(165.78, 0) * mm});
            skSolve(sketch);
        }
        {
            var Q0;
            Q0 = qSketchRegion(id + "F12", true);
            extrude(context, id + "F13", {"entities" : qUnion([Q0]), "operationType" : NewBodyOperationType.REMOVE, "oppositeDirection" : true, "depth" : 25 * mm});
        }
        {
            var Q0;
            Q0=makeQuery(id+"F4.opExtrude","SWEPT_BODY",BODY,{"disambiguationData":[OSD([sQuery(id+"F3.wireOp",EDGE,"E3"),sQuery(id+"F3.wireOp",EDGE,"E4"),sQuery(id+"F3.wireOp",EDGE,"E5.bottom"),sQuery(id+"F3.wireOp",EDGE,"E5.top"),sQuery(id+"F3.wireOp",EDGE,"E5.right"),sQuery(id+"F3.wireOp",EDGE,"E6.bottom"),sQuery(id+"F3.wireOp",EDGE,"E6.top"),sQuery(id+"F3.wireOp",EDGE,"E6.right")])]});
            var Q1;
            Q1=qCreatedBy(makeId("Front.planeOp"),FACE);
            mirror(context, id + "F14", {"operationType" : NewBodyOperationType.ADD, "entities" : qUnion([Q0]), "mirrorPlane" : qUnion([Q1])});
        }
    });
